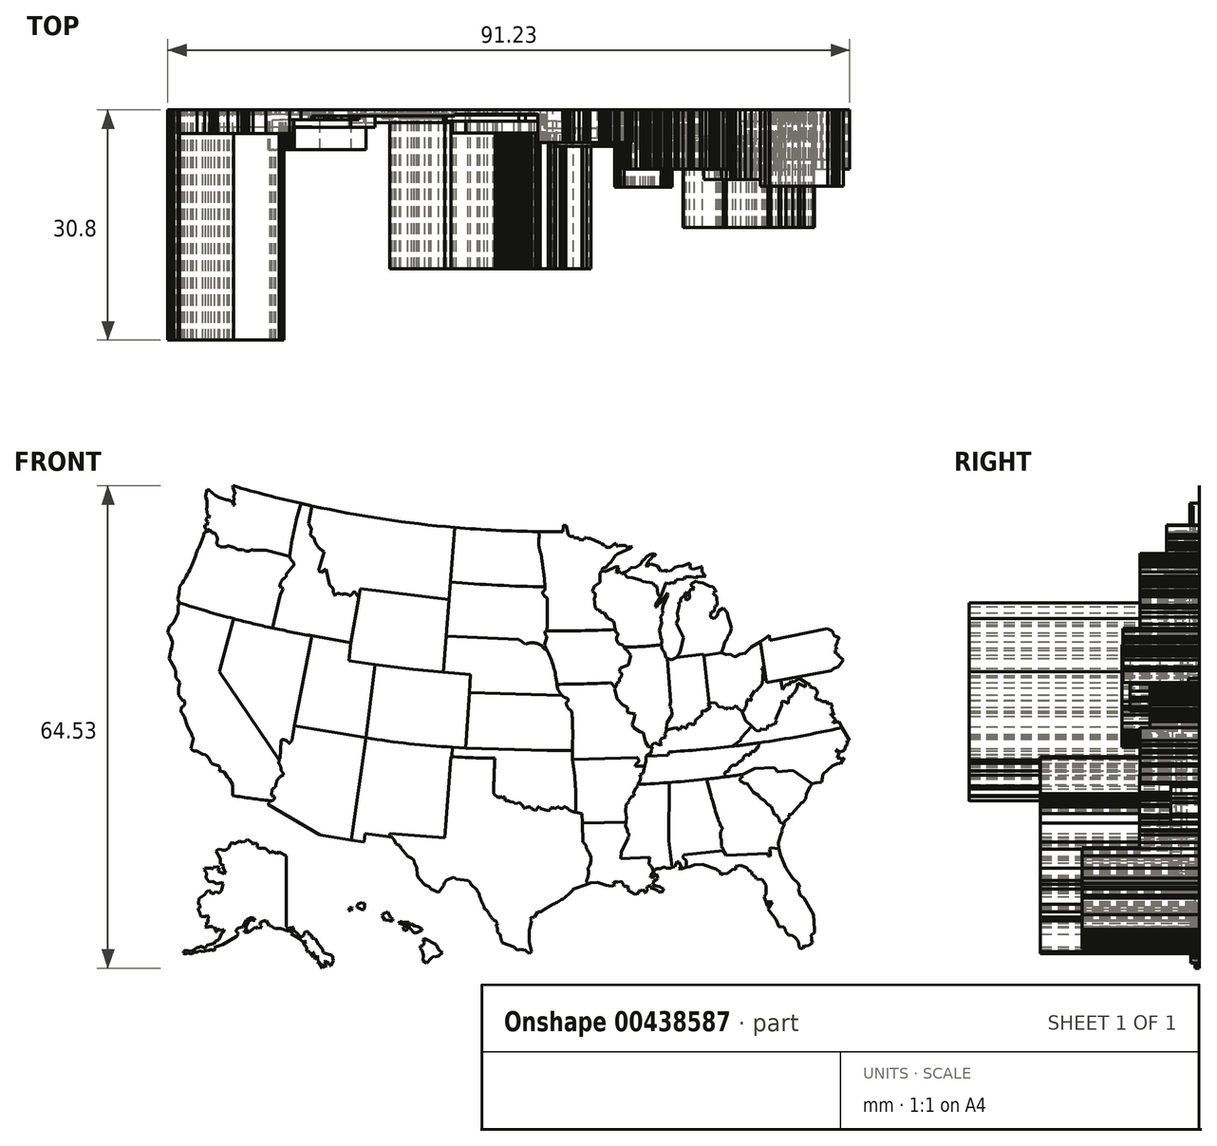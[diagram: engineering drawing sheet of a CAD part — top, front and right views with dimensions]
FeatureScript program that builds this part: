
annotation { "Feature Type Name" : "Feature", "Feature Type Description" : "" }
export const myFeature = defineFeature(function(context is Context, id is Id, definition is map)
    precondition{}
    {
        {
            var Q0;
            Q0=qCreatedBy(makeId("Front.planeOp"),FACE);
            var sketch = newSketch(context, id + "F0", { "sketchPlane" : qUnion([Q0])});
            skLineSegment(sketch, "E0", {"start": v(-20.34, -28.95) * mm, "end": v(-20.54, -28.82) * mm});
            skLineSegment(sketch, "E1", {"start": v(-20.54, -28.82) * mm, "end": v(-20.38, -28.34) * mm});
            skLineSegment(sketch, "E2", {"start": v(-20.62, -28.02) * mm, "end": v(-20.38, -28.34) * mm});
            skLineSegment(sketch, "E3", {"start": v(-20.62, -28.02) * mm, "end": v(-20.94, -27.88) * mm});
            skArc(sketch, "E4", {"start": v(-21.71, -26.67) * mm, "mid": v(-21.36, -27.3) * mm, "end": v(-20.94, -27.88) * mm});
            skArc(sketch, "E5", {"start": v(-22.15, -26.38) * mm, "mid": v(-21.93, -26.53) * mm, "end": v(-21.71, -26.67) * mm});
            skArc(sketch, "E6", {"start": v(-22.15, -26.13) * mm, "mid": v(-22.15, -26.26) * mm, "end": v(-22.15, -26.38) * mm});
            skArc(sketch, "E7", {"start": v(-22.74, -24.8) * mm, "mid": v(-22.46, -25.47) * mm, "end": v(-22.15, -26.13) * mm});
            skArc(sketch, "E8", {"start": v(-22.83, -24.33) * mm, "mid": v(-22.93, -24.22) * mm, "end": v(-23.05, -24.13) * mm});
            skArc(sketch, "E9", {"start": v(-22.83, -24.33) * mm, "mid": v(-22.8, -24.57) * mm, "end": v(-22.74, -24.8) * mm});
            skLineSegment(sketch, "E10", {"start": v(-36.72, 6.23) * mm, "end": v(-37.95, -3.53) * mm});
            skLineSegment(sketch, "E11", {"start": v(-23.98, 4.92) * mm, "end": v(-24.13, 2.5) * mm});
            skLineSegment(sketch, "E12", {"start": v(-45.2, 10.1) * mm, "end": v(-39.98, 9.18) * mm});
            skLineSegment(sketch, "E13", {"start": v(-39.98, 9.18) * mm, "end": v(-40.27, 6.76) * mm});
            skLineSegment(sketch, "E14", {"start": v(-40.27, 6.76) * mm, "end": v(-36.72, 6.23) * mm});
            skLineSegment(sketch, "E15", {"start": v(-47.5, -1.93) * mm, "end": v(-45.2, 10.1) * mm});
            skArc(sketch, "E16", {"start": v(-62.9, 14.51) * mm, "mid": v(-54.12, 12) * mm, "end": v(-45.2, 10.1) * mm});
            skLineSegment(sketch, "E17", {"start": v(-57.58, 5.33) * mm, "end": v(-55.66, 12.39) * mm});
            skLineSegment(sketch, "E18", {"start": v(-57.58, 5.33) * mm, "end": v(-49.6, -6.54) * mm});
            skLineSegment(sketch, "E19", {"start": v(-39.98, 9.18) * mm, "end": v(-38.7, 16.41) * mm});
            skLineSegment(sketch, "E20", {"start": v(-26.84, 14.95) * mm, "end": v(-38.7, 16.41) * mm});
            skLineSegment(sketch, "E21", {"start": v(-39.9, -17.25) * mm, "end": v(-37.95, -3.53) * mm});
            skLineSegment(sketch, "E22", {"start": v(-27.43, -16.92) * mm, "end": v(-26.59, -6.04) * mm});
            skLineSegment(sketch, "E23", {"start": v(-26.59, -6.04) * mm, "end": v(-26.47, -6.05) * mm});
            skLineSegment(sketch, "E24", {"start": v(-26.47, -6.05) * mm, "end": v(-26.38, -4.78) * mm});
            skLineSegment(sketch, "E25", {"start": v(-39.9, -17.25) * mm, "end": v(-38.2, -17.5) * mm});
            skLineSegment(sketch, "E26", {"start": v(-38.2, -17.5) * mm, "end": v(-38.09, -16.35) * mm});
            skLineSegment(sketch, "E27", {"start": v(-38.09, -16.35) * mm, "end": v(-34.78, -16.8) * mm});
            skLineSegment(sketch, "E28", {"start": v(-34.78, -16.8) * mm, "end": v(-34.78, -16.35) * mm});
            skLineSegment(sketch, "E29", {"start": v(-34.78, -16.35) * mm, "end": v(-27.43, -16.92) * mm});
            skLineSegment(sketch, "E30", {"start": v(-51.04, -12.46) * mm, "end": v(-44.1, -16.57) * mm});
            skLineSegment(sketch, "E31", {"start": v(-44.1, -16.57) * mm, "end": v(-39.9, -17.25) * mm});
            skArc(sketch, "E32", {"start": v(-26.47, -6.05) * mm, "mid": v(-23.6, -6.22) * mm, "end": v(-20.7, -6.27) * mm});
            skArc(sketch, "E33", {"start": v(-20.7, -6.27) * mm, "mid": v(-20.81, -8.64) * mm, "end": v(-20.87, -11) * mm});
            skArc(sketch, "E34", {"start": v(-55.68, 30.16) * mm, "mid": v(-33.87, 25.48) * mm, "end": v(-11.6, 24.05) * mm});
            skLineSegment(sketch, "E35", {"start": v(-26.84, 14.95) * mm, "end": v(-26.08, 24.6) * mm});
            skLineSegment(sketch, "E36", {"start": v(-27.22, 10.09) * mm, "end": v(-17.53, 9.6) * mm});
            skLineSegment(sketch, "E37", {"start": v(-24.13, 2.5) * mm, "end": v(-11.72, 2.13) * mm});
            skArc(sketch, "E38", {"start": v(-13.96, 10.74) * mm, "mid": v(-9.3, 10.79) * mm, "end": v(-4.62, 10.94) * mm});
            skArc(sketch, "E39", {"start": v(-12.43, 3.6) * mm, "mid": v(-8.8, 3.68) * mm, "end": v(-5.16, 3.82) * mm});
            skArc(sketch, "E40", {"start": v(-3.38, 8.64) * mm, "mid": v(-0.91, 8.67) * mm, "end": v(1.55, 8.92) * mm});
            skLineSegment(sketch, "E41", {"start": v(3.57, 7.23) * mm, "end": v(7.22, 7.64) * mm});
            skLineSegment(sketch, "E42", {"start": v(7.22, 7.64) * mm, "end": v(7.93, 1.1) * mm});
            skLineSegment(sketch, "E43", {"start": v(7.23, 7.48) * mm, "end": v(9.6, 7.85) * mm});
            skLineSegment(sketch, "E44", {"start": v(16, 10.2) * mm, "end": v(16.07, 9.52) * mm});
            skLineSegment(sketch, "E45", {"start": v(16.07, 9.52) * mm, "end": v(23.83, 11.1) * mm});
            skLineSegment(sketch, "E46", {"start": v(-10.36, -5.27) * mm, "end": v(-10.36, -6.47) * mm});
            skLineSegment(sketch, "E47", {"start": v(-10.36, -6.47) * mm, "end": v(-1.68, -6.17) * mm});
            skArc(sketch, "E48", {"start": v(-10.36, -5.27) * mm, "mid": v(-10.3, -2.61) * mm, "end": v(-10.44, 0.04) * mm});
            skArc(sketch, "E49", {"start": v(-46.68, 27.82) * mm, "mid": v(-47.57, 24.3) * mm, "end": v(-48.17, 20.7) * mm});
            skArc(sketch, "E50", {"start": v(2.53, -5.43) * mm, "mid": v(14.19, -4.28) * mm, "end": v(25.7, -2.2) * mm});
            skLineSegment(sketch, "E51", {"start": v(-0.47, -6.02) * mm, "end": v(2.5, -5.88) * mm});
            skLineSegment(sketch, "E52", {"start": v(2.5, -5.88) * mm, "end": v(2.53, -5.43) * mm});
            skArc(sketch, "E53", {"start": v(-1.64, -9.77) * mm, "mid": v(5.4, -9.3) * mm, "end": v(12.39, -8.45) * mm});
            skLineSegment(sketch, "E54", {"start": v(-9.01, -14.93) * mm, "end": v(-3.14, -14.82) * mm});
            skLineSegment(sketch, "E55", {"start": v(-49.6, -6.54) * mm, "end": v(-49.45, -6.3) * mm});
            skLineSegment(sketch, "E56", {"start": v(-49.45, -6.3) * mm, "end": v(-49.34, -3.91) * mm});
            skArc(sketch, "E57", {"start": v(-48.98, -3.76) * mm, "mid": v(-49.17, -3.8) * mm, "end": v(-49.34, -3.91) * mm});
            skArc(sketch, "E58", {"start": v(-48.71, -3.91) * mm, "mid": v(-48.84, -3.82) * mm, "end": v(-48.98, -3.76) * mm});
            skArc(sketch, "E59", {"start": v(-48.53, -3.91) * mm, "mid": v(-48.62, -3.91) * mm, "end": v(-48.71, -3.91) * mm});
            skArc(sketch, "E60", {"start": v(-47.85, -3.91) * mm, "mid": v(-48.02, -4.06) * mm, "end": v(-48.13, -4.24) * mm});
            skArc(sketch, "E61", {"start": v(-48.37, -4.23) * mm, "mid": v(-48.43, -4.06) * mm, "end": v(-48.53, -3.91) * mm});
            skArc(sketch, "E62", {"start": v(-48.37, -4.23) * mm, "mid": v(-48.25, -4.26) * mm, "end": v(-48.13, -4.24) * mm});
            skLineSegment(sketch, "E63", {"start": v(-47.85, -3.91) * mm, "end": v(-47.5, -1.93) * mm});
            skArc(sketch, "E64", {"start": v(-55.77, -11.27) * mm, "mid": v(-53.27, -11.66) * mm, "end": v(-50.77, -11.97) * mm});
            skArc(sketch, "E65", {"start": v(-50.77, -11.97) * mm, "mid": v(-50.91, -12.21) * mm, "end": v(-51.04, -12.46) * mm});
            skLineSegment(sketch, "E66", {"start": v(-55.82, -9.82) * mm, "end": v(-55.77, -11.27) * mm});
            skLineSegment(sketch, "E67", {"start": v(-55.82, -9.82) * mm, "end": v(-56.25, -9.03) * mm});
            skLineSegment(sketch, "E68", {"start": v(-56.25, -9.03) * mm, "end": v(-56.48, -8.81) * mm});
            skLineSegment(sketch, "E69", {"start": v(-56.48, -8.81) * mm, "end": v(-56.94, -8.11) * mm});
            skLineSegment(sketch, "E70", {"start": v(-56.94, -8.11) * mm, "end": v(-57.6, -8) * mm});
            skLineSegment(sketch, "E71", {"start": v(-57.6, -8) * mm, "end": v(-57.6, -7.87) * mm});
            skLineSegment(sketch, "E72", {"start": v(-57.6, -7.87) * mm, "end": v(-57.5, -7.8) * mm});
            skLineSegment(sketch, "E73", {"start": v(-57.5, -7.8) * mm, "end": v(-57.54, -7.47) * mm});
            skLineSegment(sketch, "E74", {"start": v(-57.54, -7.47) * mm, "end": v(-57.7, -7.24) * mm});
            skLineSegment(sketch, "E75", {"start": v(-57.7, -7.24) * mm, "end": v(-58.23, -7.14) * mm});
            skLineSegment(sketch, "E76", {"start": v(-58.23, -7.14) * mm, "end": v(-58.63, -6.93) * mm});
            skLineSegment(sketch, "E77", {"start": v(-58.63, -6.93) * mm, "end": v(-59.05, -6.18) * mm});
            skLineSegment(sketch, "E78", {"start": v(-59.05, -6.18) * mm, "end": v(-59.4, -5.8) * mm});
            skLineSegment(sketch, "E79", {"start": v(-59.4, -5.8) * mm, "end": v(-59.79, -5.74) * mm});
            skLineSegment(sketch, "E80", {"start": v(-59.79, -5.74) * mm, "end": v(-60.65, -5.32) * mm});
            skLineSegment(sketch, "E81", {"start": v(-60.65, -5.32) * mm, "end": v(-61.08, -5.27) * mm});
            skLineSegment(sketch, "E82", {"start": v(-61.08, -5.27) * mm, "end": v(-61.38, -4.98) * mm});
            skLineSegment(sketch, "E83", {"start": v(-61.38, -4.98) * mm, "end": v(-61.08, -3.74) * mm});
            skLineSegment(sketch, "E84", {"start": v(-61.08, -3.74) * mm, "end": v(-61.08, -3.5) * mm});
            skLineSegment(sketch, "E85", {"start": v(-61.08, -3.5) * mm, "end": v(-61.25, -3.34) * mm});
            skLineSegment(sketch, "E86", {"start": v(-61.25, -3.34) * mm, "end": v(-61.25, -3.08) * mm});
            skLineSegment(sketch, "E87", {"start": v(-61.25, -3.08) * mm, "end": v(-61.83, -2.09) * mm});
            skLineSegment(sketch, "E88", {"start": v(-61.83, -2.09) * mm, "end": v(-62.29, -0.7) * mm});
            skLineSegment(sketch, "E89", {"start": v(-62.29, -0.7) * mm, "end": v(-62.6, -0.23) * mm});
            skLineSegment(sketch, "E90", {"start": v(-62.6, -0.23) * mm, "end": v(-62.7, 0.06) * mm});
            skLineSegment(sketch, "E91", {"start": v(-62.7, 0.06) * mm, "end": v(-62.64, 0.56) * mm});
            skArc(sketch, "E92", {"start": v(-62.64, 0.56) * mm, "mid": v(-62.23, 0.9) * mm, "end": v(-62.26, 1.43) * mm});
            skLineSegment(sketch, "E93", {"start": v(-62.26, 1.43) * mm, "end": v(-62.53, 1.5) * mm});
            skLineSegment(sketch, "E94", {"start": v(-62.53, 1.5) * mm, "end": v(-63.01, 2.17) * mm});
            skLineSegment(sketch, "E95", {"start": v(-63.01, 2.17) * mm, "end": v(-63.01, 3.14) * mm});
            skLineSegment(sketch, "E96", {"start": v(-63.01, 3.14) * mm, "end": v(-62.84, 3.85) * mm});
            skLineSegment(sketch, "E97", {"start": v(-62.84, 3.85) * mm, "end": v(-63.44, 4.55) * mm});
            skLineSegment(sketch, "E98", {"start": v(-63.44, 4.55) * mm, "end": v(-63.44, 4.8) * mm});
            skArc(sketch, "E99", {"start": v(-63.44, 4.8) * mm, "mid": v(-63.42, 5.28) * mm, "end": v(-63.57, 5.73) * mm});
            skLineSegment(sketch, "E100", {"start": v(-64.28, 7.1) * mm, "end": v(-63.57, 5.73) * mm});
            skLineSegment(sketch, "E101", {"start": v(-64.28, 7.1) * mm, "end": v(-64.16, 7.52) * mm});
            skLineSegment(sketch, "E102", {"start": v(-64.16, 7.52) * mm, "end": v(-64.1, 8.17) * mm});
            skLineSegment(sketch, "E103", {"start": v(-64.1, 8.17) * mm, "end": v(-63.9, 8.5) * mm});
            skLineSegment(sketch, "E104", {"start": v(-63.9, 8.5) * mm, "end": v(-63.88, 9.29) * mm});
            skLineSegment(sketch, "E105", {"start": v(-63.88, 9.29) * mm, "end": v(-64.16, 10.12) * mm});
            skLineSegment(sketch, "E106", {"start": v(-64.16, 10.12) * mm, "end": v(-64.47, 10.53) * mm});
            skLineSegment(sketch, "E107", {"start": v(-64.47, 10.53) * mm, "end": v(-64.22, 11.4) * mm});
            skLineSegment(sketch, "E108", {"start": v(-64.22, 11.4) * mm, "end": v(-64.03, 11.46) * mm});
            skLineSegment(sketch, "E109", {"start": v(-64.03, 11.46) * mm, "end": v(-63.99, 11.62) * mm});
            skLineSegment(sketch, "E110", {"start": v(-63.99, 11.62) * mm, "end": v(-63.66, 11.91) * mm});
            skLineSegment(sketch, "E111", {"start": v(-63.66, 11.91) * mm, "end": v(-63.07, 13.2) * mm});
            skLineSegment(sketch, "E112", {"start": v(-63.07, 13.2) * mm, "end": v(-63.07, 14.03) * mm});
            skLineSegment(sketch, "E113", {"start": v(-63.07, 14.03) * mm, "end": v(-62.9, 14.51) * mm});
            skArc(sketch, "E114", {"start": v(-49.29, -7.95) * mm, "mid": v(-49.38, -7.41) * mm, "end": v(-49.65, -6.93) * mm});
            skLineSegment(sketch, "E115", {"start": v(-49.6, -6.54) * mm, "end": v(-49.65, -6.93) * mm});
            skArc(sketch, "E116", {"start": v(-50.77, -11.97) * mm, "mid": v(-50.32, -11.84) * mm, "end": v(-50.21, -11.38) * mm});
            skLineSegment(sketch, "E117", {"start": v(-50.21, -11.38) * mm, "end": v(-50.57, -11.3) * mm});
            skLineSegment(sketch, "E118", {"start": v(-50.57, -11.3) * mm, "end": v(-50.53, -10.41) * mm});
            skArc(sketch, "E119", {"start": v(-50.53, -10.41) * mm, "mid": v(-50.24, -10.25) * mm, "end": v(-50, -10) * mm});
            skArc(sketch, "E120", {"start": v(-48.97, -8.52) * mm, "mid": v(-49.74, -9.08) * mm, "end": v(-50, -10) * mm});
            skArc(sketch, "E121", {"start": v(-48.97, -8.52) * mm, "mid": v(-49.08, -8.2) * mm, "end": v(-49.29, -7.95) * mm});
            skLineSegment(sketch, "E122", {"start": v(-50.47, 11.14) * mm, "end": v(-49.45, 15.52) * mm});
            skLineSegment(sketch, "E123", {"start": v(-49.45, 15.52) * mm, "end": v(-49.06, 16.34) * mm});
            skLineSegment(sketch, "E124", {"start": v(-49.06, 16.34) * mm, "end": v(-49.18, 16.6) * mm});
            skLineSegment(sketch, "E125", {"start": v(-49.18, 16.6) * mm, "end": v(-49.49, 16.67) * mm});
            skLineSegment(sketch, "E126", {"start": v(-48.17, 20.7) * mm, "end": v(-51.36, 21.55) * mm});
            skLineSegment(sketch, "E127", {"start": v(-51.36, 21.55) * mm, "end": v(-53.04, 21.55) * mm});
            skLineSegment(sketch, "E128", {"start": v(-53.04, 21.55) * mm, "end": v(-53.04, 21.67) * mm});
            skLineSegment(sketch, "E129", {"start": v(-53.04, 21.67) * mm, "end": v(-53.6, 21.46) * mm});
            skLineSegment(sketch, "E130", {"start": v(-53.6, 21.46) * mm, "end": v(-54.1, 21.46) * mm});
            skLineSegment(sketch, "E131", {"start": v(-54.1, 21.46) * mm, "end": v(-54.43, 21.7) * mm});
            skLineSegment(sketch, "E132", {"start": v(-54.43, 21.7) * mm, "end": v(-54.57, 21.61) * mm});
            skLineSegment(sketch, "E133", {"start": v(-54.57, 21.61) * mm, "end": v(-55.07, 21.61) * mm});
            skArc(sketch, "E134", {"start": v(-55.07, 21.61) * mm, "mid": v(-55.72, 21.94) * mm, "end": v(-56.43, 22.14) * mm});
            skArc(sketch, "E135", {"start": v(-57.98, 22.44) * mm, "mid": v(-57.26, 21.99) * mm, "end": v(-56.43, 22.14) * mm});
            skArc(sketch, "E136", {"start": v(-57.98, 22.44) * mm, "mid": v(-57.86, 23.17) * mm, "end": v(-58.17, 23.85) * mm});
            skLineSegment(sketch, "E137", {"start": v(-58.17, 23.85) * mm, "end": v(-58.58, 23.85) * mm});
            skLineSegment(sketch, "E138", {"start": v(-58.58, 23.85) * mm, "end": v(-58.58, 24.15) * mm});
            skLineSegment(sketch, "E139", {"start": v(-58.58, 24.15) * mm, "end": v(-58.83, 24.15) * mm});
            skLineSegment(sketch, "E140", {"start": v(-58.83, 24.15) * mm, "end": v(-59.13, 24.38) * mm});
            skLineSegment(sketch, "E141", {"start": v(-59.13, 24.38) * mm, "end": v(-59.31, 24.3) * mm});
            skLineSegment(sketch, "E142", {"start": v(-59.31, 24.3) * mm, "end": v(-59.57, 24.6) * mm});
            skLineSegment(sketch, "E143", {"start": v(-59.57, 24.6) * mm, "end": v(-59.53, 24.93) * mm});
            skLineSegment(sketch, "E144", {"start": v(-59.53, 24.93) * mm, "end": v(-59.25, 24.93) * mm});
            skLineSegment(sketch, "E145", {"start": v(-59.25, 24.93) * mm, "end": v(-59.07, 25.4) * mm});
            skLineSegment(sketch, "E146", {"start": v(-59.07, 25.4) * mm, "end": v(-59.34, 25.55) * mm});
            skLineSegment(sketch, "E147", {"start": v(-59.34, 25.55) * mm, "end": v(-59.3, 25.94) * mm});
            skLineSegment(sketch, "E148", {"start": v(-59.3, 25.94) * mm, "end": v(-58.8, 26) * mm});
            skLineSegment(sketch, "E149", {"start": v(-58.8, 26) * mm, "end": v(-59.16, 26.34) * mm});
            skLineSegment(sketch, "E150", {"start": v(-59.16, 26.34) * mm, "end": v(-59.3, 27.1) * mm});
            skLineSegment(sketch, "E151", {"start": v(-59.3, 27.1) * mm, "end": v(-59.23, 27.36) * mm});
            skLineSegment(sketch, "E152", {"start": v(-59.23, 27.36) * mm, "end": v(-59.23, 28.3) * mm});
            skLineSegment(sketch, "E153", {"start": v(-59.23, 28.3) * mm, "end": v(-59.41, 28.62) * mm});
            skLineSegment(sketch, "E154", {"start": v(-59.41, 28.62) * mm, "end": v(-59.41, 28.8) * mm});
            skLineSegment(sketch, "E155", {"start": v(-59.41, 28.8) * mm, "end": v(-59.2, 29.68) * mm});
            skLineSegment(sketch, "E156", {"start": v(-59.2, 29.68) * mm, "end": v(-58.95, 29.65) * mm});
            skArc(sketch, "E157", {"start": v(-58.95, 29.65) * mm, "mid": v(-57.74, 28.7) * mm, "end": v(-56.25, 28.25) * mm});
            skArc(sketch, "E158", {"start": v(-55.7, 27.58) * mm, "mid": v(-55.87, 28) * mm, "end": v(-56.25, 28.25) * mm});
            skArc(sketch, "E159", {"start": v(-55.58, 28.4) * mm, "mid": v(-55.67, 28.07) * mm, "end": v(-55.51, 27.76) * mm});
            skArc(sketch, "E160", {"start": v(-55.47, 29.18) * mm, "mid": v(-55.64, 28.8) * mm, "end": v(-55.58, 28.4) * mm});
            skLineSegment(sketch, "E161", {"start": v(-55.51, 27.76) * mm, "end": v(-55.51, 27.57) * mm});
            skLineSegment(sketch, "E162", {"start": v(-55.51, 27.57) * mm, "end": v(-55.7, 27.58) * mm});
            skLineSegment(sketch, "E163", {"start": v(-55.47, 29.18) * mm, "end": v(-55.8, 30) * mm});
            skLineSegment(sketch, "E164", {"start": v(-55.8, 30) * mm, "end": v(-55.75, 30.17) * mm});
            skLineSegment(sketch, "E165", {"start": v(-55.75, 30.17) * mm, "end": v(-55.68, 30.16) * mm});
            skArc(sketch, "E166", {"start": v(-48.73, 17.9) * mm, "mid": v(-49.28, 17.39) * mm, "end": v(-49.49, 16.67) * mm});
            skArc(sketch, "E167", {"start": v(-48.73, 17.9) * mm, "mid": v(-48.63, 18.1) * mm, "end": v(-48.6, 18.34) * mm});
            skArc(sketch, "E168", {"start": v(-47.6, 19.56) * mm, "mid": v(-48.13, 18.97) * mm, "end": v(-48.6, 18.34) * mm});
            skArc(sketch, "E169", {"start": v(-48.17, 20.7) * mm, "mid": v(-48, 20.3) * mm, "end": v(-47.67, 20.02) * mm});
            skLineSegment(sketch, "E170", {"start": v(-47.67, 20.02) * mm, "end": v(-47.6, 19.56) * mm});
            skArc(sketch, "E171", {"start": v(16, 10.2) * mm, "mid": v(16.73, 10.91) * mm, "end": v(17.3, 11.76) * mm});
            skArc(sketch, "E172", {"start": v(16.77, 12.86) * mm, "mid": v(16.87, 12.6) * mm, "end": v(16.97, 12.33) * mm});
            skArc(sketch, "E173", {"start": v(17.3, 11.76) * mm, "mid": v(17.23, 12.1) * mm, "end": v(16.97, 12.33) * mm});
            skArc(sketch, "E174", {"start": v(19.11, 13.4) * mm, "mid": v(17.9, 13.32) * mm, "end": v(16.77, 12.86) * mm});
            skArc(sketch, "E175", {"start": v(19.11, 13.4) * mm, "mid": v(19.38, 13.28) * mm, "end": v(19.64, 13.4) * mm});
            skArc(sketch, "E176", {"start": v(20.53, 13.56) * mm, "mid": v(20.07, 13.56) * mm, "end": v(19.64, 13.4) * mm});
            skArc(sketch, "E177", {"start": v(20.53, 13.56) * mm, "mid": v(20.87, 13.94) * mm, "end": v(21.18, 14.34) * mm});
            skArc(sketch, "E178", {"start": v(21.18, 14.34) * mm, "mid": v(21.6, 14.5) * mm, "end": v(21.45, 14.92) * mm});
            skArc(sketch, "E179", {"start": v(21.58, 15.51) * mm, "mid": v(21.47, 15.23) * mm, "end": v(21.45, 14.92) * mm});
            skArc(sketch, "E180", {"start": v(21.38, 16.32) * mm, "mid": v(21.08, 15.82) * mm, "end": v(21.58, 15.51) * mm});
            skArc(sketch, "E181", {"start": v(21.38, 16.32) * mm, "mid": v(21.56, 16.5) * mm, "end": v(21.73, 16.7) * mm});
            skArc(sketch, "E182", {"start": v(23.04, 18.39) * mm, "mid": v(22.3, 17.61) * mm, "end": v(21.73, 16.7) * mm});
            skArc(sketch, "E183", {"start": v(23.83, 11.1) * mm, "mid": v(24.11, 10.88) * mm, "end": v(24.45, 10.78) * mm});
            skArc(sketch, "E184", {"start": v(24.45, 10.78) * mm, "mid": v(24.6, 10.34) * mm, "end": v(24.89, 9.98) * mm});
            skArc(sketch, "E185", {"start": v(25.37, 9.77) * mm, "mid": v(25.17, 9.96) * mm, "end": v(24.89, 9.98) * mm});
            skLineSegment(sketch, "E186", {"start": v(25.37, 9.77) * mm, "end": v(27, 9.26) * mm});
            skLineSegment(sketch, "E187", {"start": v(27, 9.26) * mm, "end": v(27, 8.37) * mm});
            skArc(sketch, "E188", {"start": v(27, 8.37) * mm, "mid": v(28.7, 8.93) * mm, "end": v(30.08, 10.05) * mm});
            skLineSegment(sketch, "E189", {"start": v(30.08, 10.05) * mm, "end": v(29.67, 10.23) * mm});
            skArc(sketch, "E190", {"start": v(28.36, 9.39) * mm, "mid": v(29.08, 9.7) * mm, "end": v(29.67, 10.23) * mm});
            skArc(sketch, "E191", {"start": v(27.92, 9.39) * mm, "mid": v(28.14, 9.35) * mm, "end": v(28.36, 9.39) * mm});
            skLineSegment(sketch, "E192", {"start": v(27.92, 9.39) * mm, "end": v(27.42, 8.95) * mm});
            skLineSegment(sketch, "E193", {"start": v(27.42, 8.95) * mm, "end": v(27.23, 8.9) * mm});
            skLineSegment(sketch, "E194", {"start": v(27.23, 8.9) * mm, "end": v(27.23, 9.05) * mm});
            skLineSegment(sketch, "E195", {"start": v(27.23, 9.05) * mm, "end": v(27.42, 9.26) * mm});
            skLineSegment(sketch, "E196", {"start": v(27.42, 9.26) * mm, "end": v(27.42, 9.44) * mm});
            skLineSegment(sketch, "E197", {"start": v(27.42, 9.44) * mm, "end": v(27.22, 9.63) * mm});
            skLineSegment(sketch, "E198", {"start": v(27.22, 9.63) * mm, "end": v(27.35, 9.77) * mm});
            skLineSegment(sketch, "E199", {"start": v(27.35, 9.77) * mm, "end": v(27.35, 10.79) * mm});
            skLineSegment(sketch, "E200", {"start": v(27.35, 10.79) * mm, "end": v(27.06, 11.96) * mm});
            skLineSegment(sketch, "E201", {"start": v(27.06, 11.96) * mm, "end": v(27.06, 13.72) * mm});
            skLineSegment(sketch, "E202", {"start": v(27.06, 13.72) * mm, "end": v(26.66, 15.58) * mm});
            skArc(sketch, "E203", {"start": v(26.66, 15.58) * mm, "mid": v(26.51, 15.72) * mm, "end": v(26.32, 15.64) * mm});
            skArc(sketch, "E204", {"start": v(24.37, 18.62) * mm, "mid": v(23.7, 18.56) * mm, "end": v(23.04, 18.39) * mm});
            skLineSegment(sketch, "E205", {"start": v(24.37, 18.62) * mm, "end": v(25.7, 18.98) * mm});
            skLineSegment(sketch, "E206", {"start": v(25.7, 18.98) * mm, "end": v(26.12, 17.45) * mm});
            skArc(sketch, "E207", {"start": v(25.98, 16.83) * mm, "mid": v(26.13, 17.12) * mm, "end": v(26.12, 17.45) * mm});
            skLineSegment(sketch, "E208", {"start": v(25.98, 16.83) * mm, "end": v(26.36, 16.1) * mm});
            skLineSegment(sketch, "E209", {"start": v(26.36, 16.1) * mm, "end": v(26.32, 15.64) * mm});
            skLineSegment(sketch, "E210", {"start": v(-62.9, 14.51) * mm, "end": v(-63.14, 15.01) * mm});
            skLineSegment(sketch, "E211", {"start": v(-63.14, 15.01) * mm, "end": v(-62.97, 15.69) * mm});
            skLineSegment(sketch, "E212", {"start": v(-62.97, 15.69) * mm, "end": v(-62.9, 16.65) * mm});
            skArc(sketch, "E213", {"start": v(-62.9, 16.65) * mm, "mid": v(-61.53, 18.95) * mm, "end": v(-60.56, 21.44) * mm});
            skLineSegment(sketch, "E214", {"start": v(-58.83, 24.15) * mm, "end": v(-59.54, 24) * mm});
            skArc(sketch, "E215", {"start": v(-60.56, 21.44) * mm, "mid": v(-60, 22.7) * mm, "end": v(-59.54, 24) * mm});
            skLineSegment(sketch, "E216", {"start": v(-17.53, 9.6) * mm, "end": v(-16.6, 8.98) * mm});
            skArc(sketch, "E217", {"start": v(-14.3, 8.68) * mm, "mid": v(-15.4, 9.16) * mm, "end": v(-16.6, 8.98) * mm});
            skArc(sketch, "E218", {"start": v(-14.3, 8.68) * mm, "mid": v(-14.11, 8.35) * mm, "end": v(-13.74, 8.25) * mm});
            skArc(sketch, "E219", {"start": v(-12.43, 3.6) * mm, "mid": v(-12.86, 6) * mm, "end": v(-13.74, 8.25) * mm});
            skArc(sketch, "E220", {"start": v(-12.43, 3.6) * mm, "mid": v(-12.19, 2.81) * mm, "end": v(-11.72, 2.13) * mm});
            skArc(sketch, "E221", {"start": v(-11.72, 2.13) * mm, "mid": v(-11.4, 1.88) * mm, "end": v(-11, 1.75) * mm});
            skArc(sketch, "E222", {"start": v(-11.16, 1.2) * mm, "mid": v(-10.92, 1.43) * mm, "end": v(-11, 1.75) * mm});
            skArc(sketch, "E223", {"start": v(-11.16, 1.2) * mm, "mid": v(-10.97, 0.52) * mm, "end": v(-10.44, 0.04) * mm});
            skLineSegment(sketch, "E224", {"start": v(-45.17, 27.48) * mm, "end": v(-45.64, 25.13) * mm});
            skLineSegment(sketch, "E225", {"start": v(-45.64, 25.13) * mm, "end": v(-45.28, 24.39) * mm});
            skLineSegment(sketch, "E226", {"start": v(-45.28, 24.39) * mm, "end": v(-45.4, 23.67) * mm});
            skArc(sketch, "E227", {"start": v(-45.4, 23.67) * mm, "mid": v(-45.18, 23.38) * mm, "end": v(-44.88, 23.2) * mm});
            skArc(sketch, "E228", {"start": v(-44.88, 23.2) * mm, "mid": v(-44.45, 22.11) * mm, "end": v(-43.56, 21.37) * mm});
            skLineSegment(sketch, "E229", {"start": v(-44.33, 18.83) * mm, "end": v(-43.56, 21.37) * mm});
            skLineSegment(sketch, "E230", {"start": v(-44, 18.55) * mm, "end": v(-44.33, 18.83) * mm});
            skLineSegment(sketch, "E231", {"start": v(-42.33, 16.4) * mm, "end": v(-42.87, 16.94) * mm});
            skLineSegment(sketch, "E232", {"start": v(-42.87, 16.94) * mm, "end": v(-43.29, 19) * mm});
            skLineSegment(sketch, "E233", {"start": v(-43.29, 19) * mm, "end": v(-44, 18.55) * mm});
            skArc(sketch, "E234", {"start": v(-42.33, 16.4) * mm, "mid": v(-42.3, 15.92) * mm, "end": v(-42.11, 15.49) * mm});
            skArc(sketch, "E235", {"start": v(-41.24, 15.6) * mm, "mid": v(-41.7, 15.77) * mm, "end": v(-42.11, 15.49) * mm});
            skArc(sketch, "E236", {"start": v(-40.14, 15.49) * mm, "mid": v(-40.68, 15.7) * mm, "end": v(-41.24, 15.6) * mm});
            skArc(sketch, "E237", {"start": v(-40.14, 15.49) * mm, "mid": v(-39.86, 15.6) * mm, "end": v(-39.74, 15.9) * mm});
            skArc(sketch, "E238", {"start": v(-39.32, 15.88) * mm, "mid": v(-39.17, 15.53) * mm, "end": v(-38.91, 15.26) * mm});
            skArc(sketch, "E239", {"start": v(-39.32, 15.88) * mm, "mid": v(-39.53, 15.94) * mm, "end": v(-39.74, 15.9) * mm});
            skArc(sketch, "E240", {"start": v(-9.92, -13.52) * mm, "mid": v(-9.92, -9.98) * mm, "end": v(-10.36, -6.47) * mm});
            skLineSegment(sketch, "E241", {"start": v(-9.92, -13.52) * mm, "end": v(-9.07, -13.67) * mm});
            skLineSegment(sketch, "E242", {"start": v(-9.07, -13.67) * mm, "end": v(-9.01, -14.93) * mm});
            skLineSegment(sketch, "E243", {"start": v(-9.01, -14.93) * mm, "end": v(-8.96, -17.48) * mm});
            skLineSegment(sketch, "E244", {"start": v(-20.34, -28.95) * mm, "end": v(-20.34, -29.39) * mm});
            skArc(sketch, "E245", {"start": v(-20.34, -29.39) * mm, "mid": v(-20.25, -29.66) * mm, "end": v(-20.01, -29.82) * mm});
            skArc(sketch, "E246", {"start": v(-20.01, -29.82) * mm, "mid": v(-19.9, -30.4) * mm, "end": v(-19.71, -30.96) * mm});
            skLineSegment(sketch, "E247", {"start": v(-15.8, -32.15) * mm, "end": v(-16.1, -32.38) * mm});
            skLineSegment(sketch, "E248", {"start": v(-16.1, -32.38) * mm, "end": v(-16.63, -31.97) * mm});
            skLineSegment(sketch, "E249", {"start": v(-16.63, -31.97) * mm, "end": v(-17.25, -31.87) * mm});
            skLineSegment(sketch, "E250", {"start": v(-17.25, -31.87) * mm, "end": v(-17.48, -31.94) * mm});
            skLineSegment(sketch, "E251", {"start": v(-17.48, -31.94) * mm, "end": v(-17.68, -31.95) * mm});
            skLineSegment(sketch, "E252", {"start": v(-17.68, -31.95) * mm, "end": v(-18.14, -31.52) * mm});
            skLineSegment(sketch, "E253", {"start": v(-18.14, -31.52) * mm, "end": v(-19.71, -30.96) * mm});
            skLineSegment(sketch, "E254", {"start": v(-0.7, -7.34) * mm, "end": v(-1.95, -7.34) * mm});
            skArc(sketch, "E255", {"start": v(-1.47, -6.76) * mm, "mid": v(-1.76, -7) * mm, "end": v(-1.95, -7.34) * mm});
            skArc(sketch, "E256", {"start": v(-1.47, -6.76) * mm, "mid": v(-1.5, -6.44) * mm, "end": v(-1.68, -6.17) * mm});
            skLineSegment(sketch, "E257", {"start": v(-13.74, 8.25) * mm, "end": v(-14.05, 8.84) * mm});
            skLineSegment(sketch, "E258", {"start": v(-14.05, 8.84) * mm, "end": v(-13.74, 9.96) * mm});
            skArc(sketch, "E259", {"start": v(-13.96, 10.74) * mm, "mid": v(-13.97, 10.32) * mm, "end": v(-13.74, 9.96) * mm});
            skArc(sketch, "E260", {"start": v(-26.65, 17.32) * mm, "mid": v(-20.33, 16.87) * mm, "end": v(-14, 16.64) * mm});
            skArc(sketch, "E261", {"start": v(-13.74, 10.74) * mm, "mid": v(-13.68, 12.95) * mm, "end": v(-13.72, 15.15) * mm});
            skArc(sketch, "E262", {"start": v(-14.34, 16) * mm, "mid": v(-14.04, 16.25) * mm, "end": v(-14, 16.64) * mm});
            skArc(sketch, "E263", {"start": v(-14.34, 16) * mm, "mid": v(-14.13, 15.5) * mm, "end": v(-13.72, 15.15) * mm});
            skArc(sketch, "E264", {"start": v(-14.8, 23.25) * mm, "mid": v(-14.78, 23.67) * mm, "end": v(-14.96, 24.05) * mm});
            skArc(sketch, "E265", {"start": v(-14.8, 23.25) * mm, "mid": v(-14.82, 22.12) * mm, "end": v(-14.52, 21.03) * mm});
            skLineSegment(sketch, "E266", {"start": v(-14.52, 21.03) * mm, "end": v(-14.07, 17.77) * mm});
            skLineSegment(sketch, "E267", {"start": v(-14.07, 17.77) * mm, "end": v(-14, 16.64) * mm});
            skArc(sketch, "E268", {"start": v(-8.45, -18.47) * mm, "mid": v(-8.57, -17.9) * mm, "end": v(-8.96, -17.48) * mm});
            skArc(sketch, "E269", {"start": v(-8.25, -21) * mm, "mid": v(-7.86, -19.7) * mm, "end": v(-8.45, -18.47) * mm});
            skArc(sketch, "E270", {"start": v(-8.45, -22.63) * mm, "mid": v(-8.2, -21.83) * mm, "end": v(-8.25, -21) * mm});
            skLineSegment(sketch, "E271", {"start": v(-8.45, -22.63) * mm, "end": v(-8.35, -23.12) * mm});
            skLineSegment(sketch, "E272", {"start": v(-8.35, -23.12) * mm, "end": v(-10.19, -23.78) * mm});
            skArc(sketch, "E273", {"start": v(-12.92, -25.8) * mm, "mid": v(-11.43, -24.96) * mm, "end": v(-10.19, -23.78) * mm});
            skArc(sketch, "E274", {"start": v(-12.92, -25.8) * mm, "mid": v(-13.78, -26.3) * mm, "end": v(-14.58, -26.86) * mm});
            skArc(sketch, "E275", {"start": v(-15.8, -28) * mm, "mid": v(-16.13, -30.08) * mm, "end": v(-15.8, -32.15) * mm});
            skLineSegment(sketch, "E276", {"start": v(-14.58, -26.86) * mm, "end": v(-14.95, -26.86) * mm});
            skLineSegment(sketch, "E277", {"start": v(-14.95, -26.86) * mm, "end": v(-15.4, -27.54) * mm});
            skLineSegment(sketch, "E278", {"start": v(-15.4, -27.54) * mm, "end": v(-15.85, -27.58) * mm});
            skLineSegment(sketch, "E279", {"start": v(-15.85, -27.58) * mm, "end": v(-15.97, -27.8) * mm});
            skLineSegment(sketch, "E280", {"start": v(-15.97, -27.8) * mm, "end": v(-15.8, -28) * mm});
            skLineSegment(sketch, "E281", {"start": v(-23.05, -24.13) * mm, "end": v(-23.05, -23.97) * mm});
            skLineSegment(sketch, "E282", {"start": v(-23.05, -23.97) * mm, "end": v(-23.96, -23.07) * mm});
            skLineSegment(sketch, "E283", {"start": v(-23.96, -23.07) * mm, "end": v(-23.97, -22.9) * mm});
            skLineSegment(sketch, "E284", {"start": v(-23.97, -22.9) * mm, "end": v(-24.28, -22.66) * mm});
            skLineSegment(sketch, "E285", {"start": v(-24.28, -22.66) * mm, "end": v(-25.9, -22.47) * mm});
            skLineSegment(sketch, "E286", {"start": v(-25.9, -22.47) * mm, "end": v(-26.24, -22.2) * mm});
            skLineSegment(sketch, "E287", {"start": v(-26.24, -22.2) * mm, "end": v(-27.17, -22.56) * mm});
            skLineSegment(sketch, "E288", {"start": v(-27.17, -22.56) * mm, "end": v(-27.5, -22.96) * mm});
            skLineSegment(sketch, "E289", {"start": v(-27.5, -22.96) * mm, "end": v(-27.53, -23.27) * mm});
            skLineSegment(sketch, "E290", {"start": v(-27.53, -23.27) * mm, "end": v(-28.22, -24.21) * mm});
            skLineSegment(sketch, "E291", {"start": v(-28.22, -24.21) * mm, "end": v(-29.26, -23.8) * mm});
            skLineSegment(sketch, "E292", {"start": v(-29.26, -23.8) * mm, "end": v(-29.5, -23.46) * mm});
            skLineSegment(sketch, "E293", {"start": v(-29.5, -23.46) * mm, "end": v(-30.1, -23.2) * mm});
            skLineSegment(sketch, "E294", {"start": v(-30.1, -23.2) * mm, "end": v(-30.85, -22.4) * mm});
            skLineSegment(sketch, "E295", {"start": v(-30.85, -22.4) * mm, "end": v(-31.1, -21.96) * mm});
            skLineSegment(sketch, "E296", {"start": v(-31.1, -21.96) * mm, "end": v(-31.13, -20.93) * mm});
            skLineSegment(sketch, "E297", {"start": v(-31.13, -20.93) * mm, "end": v(-31.47, -20.31) * mm});
            skLineSegment(sketch, "E298", {"start": v(-31.47, -20.31) * mm, "end": v(-31.54, -19.94) * mm});
            skLineSegment(sketch, "E299", {"start": v(-31.54, -19.94) * mm, "end": v(-31.83, -19.65) * mm});
            skLineSegment(sketch, "E300", {"start": v(-31.83, -19.65) * mm, "end": v(-32.35, -19.38) * mm});
            skLineSegment(sketch, "E301", {"start": v(-32.35, -19.38) * mm, "end": v(-33.33, -18.26) * mm});
            skLineSegment(sketch, "E302", {"start": v(-33.33, -18.26) * mm, "end": v(-33.46, -17.94) * mm});
            skLineSegment(sketch, "E303", {"start": v(-33.46, -17.94) * mm, "end": v(-33.93, -17.72) * mm});
            skLineSegment(sketch, "E304", {"start": v(-33.93, -17.72) * mm, "end": v(-34.11, -17.25) * mm});
            skLineSegment(sketch, "E305", {"start": v(-34.11, -17.25) * mm, "end": v(-34.48, -16.88) * mm});
            skLineSegment(sketch, "E306", {"start": v(-34.48, -16.88) * mm, "end": v(-34.78, -16.8) * mm});
            skArc(sketch, "E307", {"start": v(7.64, -9.07) * mm, "mid": v(8.4, -11.92) * mm, "end": v(9.25, -14.75) * mm});
            skLineSegment(sketch, "E308", {"start": v(2.65, -9.53) * mm, "end": v(2.54, -17.3) * mm});
            skLineSegment(sketch, "E309", {"start": v(2.54, -17.3) * mm, "end": v(2.98, -20.86) * mm});
            skLineSegment(sketch, "E310", {"start": v(2.98, -20.86) * mm, "end": v(3.36, -20.82) * mm});
            skLineSegment(sketch, "E311", {"start": v(3.36, -20.82) * mm, "end": v(3.66, -20.08) * mm});
            skLineSegment(sketch, "E312", {"start": v(3.66, -20.08) * mm, "end": v(3.88, -20.17) * mm});
            skLineSegment(sketch, "E313", {"start": v(3.88, -20.17) * mm, "end": v(4.25, -20.85) * mm});
            skLineSegment(sketch, "E314", {"start": v(4.25, -20.85) * mm, "end": v(3.91, -21.07) * mm});
            skLineSegment(sketch, "E315", {"start": v(3.91, -21.07) * mm, "end": v(4.17, -21.13) * mm});
            skLineSegment(sketch, "E316", {"start": v(4.17, -21.13) * mm, "end": v(4.94, -20.84) * mm});
            skLineSegment(sketch, "E317", {"start": v(4.94, -20.84) * mm, "end": v(5.36, -20.77) * mm});
            skLineSegment(sketch, "E318", {"start": v(5.36, -20.77) * mm, "end": v(5.98, -20.57) * mm});
            skLineSegment(sketch, "E319", {"start": v(5.98, -20.57) * mm, "end": v(7.07, -20.46) * mm});
            skLineSegment(sketch, "E320", {"start": v(7.07, -20.46) * mm, "end": v(8.89, -21.1) * mm});
            skLineSegment(sketch, "E321", {"start": v(8.89, -21.1) * mm, "end": v(9.08, -21.33) * mm});
            skLineSegment(sketch, "E322", {"start": v(9.08, -21.33) * mm, "end": v(9.21, -21.33) * mm});
            skLineSegment(sketch, "E323", {"start": v(9.21, -21.33) * mm, "end": v(9.45, -21.52) * mm});
            skLineSegment(sketch, "E324", {"start": v(9.45, -21.52) * mm, "end": v(9.56, -21.9) * mm});
            skLineSegment(sketch, "E325", {"start": v(9.56, -21.9) * mm, "end": v(9.83, -21.73) * mm});
            skLineSegment(sketch, "E326", {"start": v(9.83, -21.73) * mm, "end": v(10.42, -21.7) * mm});
            skLineSegment(sketch, "E327", {"start": v(10.42, -21.7) * mm, "end": v(11.14, -21.1) * mm});
            skLineSegment(sketch, "E328", {"start": v(11.14, -21.1) * mm, "end": v(11.53, -21.16) * mm});
            skLineSegment(sketch, "E329", {"start": v(11.53, -21.16) * mm, "end": v(11.5, -20.72) * mm});
            skLineSegment(sketch, "E330", {"start": v(11.5, -20.72) * mm, "end": v(12.22, -20.61) * mm});
            skLineSegment(sketch, "E331", {"start": v(12.22, -20.61) * mm, "end": v(12.98, -20.9) * mm});
            skLineSegment(sketch, "E332", {"start": v(12.98, -20.9) * mm, "end": v(13.29, -21.3) * mm});
            skLineSegment(sketch, "E333", {"start": v(13.29, -21.3) * mm, "end": v(13.6, -21.45) * mm});
            skLineSegment(sketch, "E334", {"start": v(13.6, -21.45) * mm, "end": v(13.72, -21.9) * mm});
            skLineSegment(sketch, "E335", {"start": v(13.72, -21.9) * mm, "end": v(14.07, -21.99) * mm});
            skLineSegment(sketch, "E336", {"start": v(14.07, -21.99) * mm, "end": v(14.3, -22.42) * mm});
            skLineSegment(sketch, "E337", {"start": v(14.3, -22.42) * mm, "end": v(15.04, -22.5) * mm});
            skLineSegment(sketch, "E338", {"start": v(10.26, -19.28) * mm, "end": v(15.82, -19) * mm});
            skLineSegment(sketch, "E339", {"start": v(4.5, -19.22) * mm, "end": v(9.89, -18.66) * mm});
            skLineSegment(sketch, "E340", {"start": v(9.89, -18.66) * mm, "end": v(10.26, -19.28) * mm});
            skLineSegment(sketch, "E341", {"start": v(4.5, -19.22) * mm, "end": v(4.46, -19.57) * mm});
            skLineSegment(sketch, "E342", {"start": v(4.46, -19.57) * mm, "end": v(4.93, -19.98) * mm});
            skLineSegment(sketch, "E343", {"start": v(4.93, -19.98) * mm, "end": v(4.94, -20.84) * mm});
            skArc(sketch, "E344", {"start": v(9.44, -15.32) * mm, "mid": v(9.42, -15) * mm, "end": v(9.25, -14.75) * mm});
            skArc(sketch, "E345", {"start": v(9.72, -15.71) * mm, "mid": v(9.65, -15.47) * mm, "end": v(9.44, -15.32) * mm});
            skArc(sketch, "E346", {"start": v(9.72, -15.71) * mm, "mid": v(9.47, -16.38) * mm, "end": v(9.57, -17.08) * mm});
            skArc(sketch, "E347", {"start": v(9.57, -18.09) * mm, "mid": v(9.63, -17.58) * mm, "end": v(9.57, -17.08) * mm});
            skArc(sketch, "E348", {"start": v(9.89, -18.66) * mm, "mid": v(9.8, -18.34) * mm, "end": v(9.57, -18.09) * mm});
            skLineSegment(sketch, "E349", {"start": v(0.03, -19.55) * mm, "end": v(-3.86, -19.74) * mm});
            skLineSegment(sketch, "E350", {"start": v(-3.86, -19.74) * mm, "end": v(-3.8, -18.8) * mm});
            skLineSegment(sketch, "E351", {"start": v(-3.8, -18.8) * mm, "end": v(-2.84, -16.95) * mm});
            skLineSegment(sketch, "E352", {"start": v(0.03, -19.55) * mm, "end": v(-0.1, -20.44) * mm});
            skLineSegment(sketch, "E353", {"start": v(-0.1, -20.44) * mm, "end": v(0.29, -20.83) * mm});
            skLineSegment(sketch, "E354", {"start": v(0.29, -20.83) * mm, "end": v(0.53, -21.46) * mm});
            skLineSegment(sketch, "E355", {"start": v(0.53, -21.46) * mm, "end": v(0.96, -21.02) * mm});
            skArc(sketch, "E356", {"start": v(0.96, -21.02) * mm, "mid": v(1.25, -21.07) * mm, "end": v(1.55, -21.02) * mm});
            skArc(sketch, "E357", {"start": v(2.3, -21.02) * mm, "mid": v(1.92, -20.86) * mm, "end": v(1.55, -21.02) * mm});
            skLineSegment(sketch, "E358", {"start": v(2.98, -20.86) * mm, "end": v(2.87, -20.99) * mm});
            skLineSegment(sketch, "E359", {"start": v(2.87, -20.99) * mm, "end": v(2.3, -21.02) * mm});
            skArc(sketch, "E360", {"start": v(-11.19, -12.81) * mm, "mid": v(-10.61, -13.27) * mm, "end": v(-9.92, -13.52) * mm});
            skArc(sketch, "E361", {"start": v(-11.19, -12.81) * mm, "mid": v(-11.43, -12.8) * mm, "end": v(-11.59, -12.98) * mm});
            skArc(sketch, "E362", {"start": v(-12, -12.96) * mm, "mid": v(-12.3, -12.82) * mm, "end": v(-12.54, -13.02) * mm});
            skLineSegment(sketch, "E363", {"start": v(-11.59, -12.98) * mm, "end": v(-12, -12.96) * mm});
            skLineSegment(sketch, "E364", {"start": v(-12.54, -13.02) * mm, "end": v(-12.75, -12.92) * mm});
            skLineSegment(sketch, "E365", {"start": v(-12.75, -12.92) * mm, "end": v(-13.22, -12.93) * mm});
            skLineSegment(sketch, "E366", {"start": v(-13.22, -12.93) * mm, "end": v(-13.29, -13.16) * mm});
            skLineSegment(sketch, "E367", {"start": v(-13.29, -13.16) * mm, "end": v(-13.54, -13.28) * mm});
            skLineSegment(sketch, "E368", {"start": v(-13.54, -13.28) * mm, "end": v(-14.66, -12.96) * mm});
            skLineSegment(sketch, "E369", {"start": v(-14.66, -12.96) * mm, "end": v(-14.8, -12.76) * mm});
            skLineSegment(sketch, "E370", {"start": v(-14.8, -12.76) * mm, "end": v(-14.93, -12.77) * mm});
            skLineSegment(sketch, "E371", {"start": v(-14.93, -12.77) * mm, "end": v(-15.16, -13.2) * mm});
            skLineSegment(sketch, "E372", {"start": v(-15.16, -13.2) * mm, "end": v(-15.31, -13.26) * mm});
            skLineSegment(sketch, "E373", {"start": v(-15.31, -13.26) * mm, "end": v(-15.82, -13.07) * mm});
            skLineSegment(sketch, "E374", {"start": v(-15.82, -13.07) * mm, "end": v(-15.89, -12.81) * mm});
            skLineSegment(sketch, "E375", {"start": v(-15.89, -12.81) * mm, "end": v(-16.24, -12.8) * mm});
            skLineSegment(sketch, "E376", {"start": v(-16.24, -12.8) * mm, "end": v(-16.35, -12.73) * mm});
            skLineSegment(sketch, "E377", {"start": v(-16.35, -12.73) * mm, "end": v(-16.63, -13) * mm});
            skLineSegment(sketch, "E378", {"start": v(-16.63, -13) * mm, "end": v(-16.9, -12.9) * mm});
            skLineSegment(sketch, "E379", {"start": v(-16.9, -12.9) * mm, "end": v(-16.93, -12.67) * mm});
            skLineSegment(sketch, "E380", {"start": v(-16.93, -12.67) * mm, "end": v(-17.29, -12.27) * mm});
            skLineSegment(sketch, "E381", {"start": v(-17.29, -12.27) * mm, "end": v(-17.66, -12.2) * mm});
            skLineSegment(sketch, "E382", {"start": v(-17.66, -12.2) * mm, "end": v(-17.88, -12.4) * mm});
            skLineSegment(sketch, "E383", {"start": v(-17.88, -12.4) * mm, "end": v(-18.23, -12.16) * mm});
            skLineSegment(sketch, "E384", {"start": v(-18.23, -12.16) * mm, "end": v(-18.62, -12.12) * mm});
            skLineSegment(sketch, "E385", {"start": v(-18.62, -12.12) * mm, "end": v(-18.9, -12) * mm});
            skLineSegment(sketch, "E386", {"start": v(-18.9, -12) * mm, "end": v(-19.35, -11.96) * mm});
            skLineSegment(sketch, "E387", {"start": v(-19.35, -11.96) * mm, "end": v(-19.36, -11.53) * mm});
            skLineSegment(sketch, "E388", {"start": v(-19.36, -11.53) * mm, "end": v(-19.6, -11.42) * mm});
            skLineSegment(sketch, "E389", {"start": v(-19.6, -11.42) * mm, "end": v(-19.64, -11.56) * mm});
            skLineSegment(sketch, "E390", {"start": v(-19.64, -11.56) * mm, "end": v(-19.82, -11.57) * mm});
            skLineSegment(sketch, "E391", {"start": v(-19.82, -11.57) * mm, "end": v(-20.01, -11.34) * mm});
            skLineSegment(sketch, "E392", {"start": v(-20.01, -11.34) * mm, "end": v(-20.1, -11.56) * mm});
            skLineSegment(sketch, "E393", {"start": v(-20.1, -11.56) * mm, "end": v(-20.24, -11.57) * mm});
            skLineSegment(sketch, "E394", {"start": v(-20.24, -11.57) * mm, "end": v(-20.87, -11) * mm});
            skLineSegment(sketch, "E395", {"start": v(-8.35, -23.12) * mm, "end": v(-7.92, -22.97) * mm});
            skLineSegment(sketch, "E396", {"start": v(-7.92, -22.97) * mm, "end": v(-6.97, -22.9) * mm});
            skLineSegment(sketch, "E397", {"start": v(-6.97, -22.9) * mm, "end": v(-5.83, -23.3) * mm});
            skLineSegment(sketch, "E398", {"start": v(-5.83, -23.3) * mm, "end": v(-5.15, -23.42) * mm});
            skLineSegment(sketch, "E399", {"start": v(-5.15, -23.42) * mm, "end": v(-4.63, -23.18) * mm});
            skLineSegment(sketch, "E400", {"start": v(-4.63, -23.18) * mm, "end": v(-4.86, -23.05) * mm});
            skLineSegment(sketch, "E401", {"start": v(-4.86, -23.05) * mm, "end": v(-4.8, -22.87) * mm});
            skLineSegment(sketch, "E402", {"start": v(-4.8, -22.87) * mm, "end": v(-4.46, -22.75) * mm});
            skLineSegment(sketch, "E403", {"start": v(-4.46, -22.75) * mm, "end": v(-4.26, -22.9) * mm});
            skLineSegment(sketch, "E404", {"start": v(-4.26, -22.9) * mm, "end": v(-4.03, -22.78) * mm});
            skLineSegment(sketch, "E405", {"start": v(-4.03, -22.78) * mm, "end": v(-3.7, -22.86) * mm});
            skLineSegment(sketch, "E406", {"start": v(-3.7, -22.86) * mm, "end": v(-3.5, -23.18) * mm});
            skLineSegment(sketch, "E407", {"start": v(-3.5, -23.18) * mm, "end": v(-3.5, -23.41) * mm});
            skLineSegment(sketch, "E408", {"start": v(-3.5, -23.41) * mm, "end": v(-3, -23.42) * mm});
            skLineSegment(sketch, "E409", {"start": v(-3, -23.42) * mm, "end": v(-2.8, -23.6) * mm});
            skLineSegment(sketch, "E410", {"start": v(-2.8, -23.6) * mm, "end": v(-2.98, -23.89) * mm});
            skLineSegment(sketch, "E411", {"start": v(-2.98, -23.89) * mm, "end": v(-1.92, -24.48) * mm});
            skLineSegment(sketch, "E412", {"start": v(-1.92, -24.48) * mm, "end": v(-1.5, -24.32) * mm});
            skLineSegment(sketch, "E413", {"start": v(-1.5, -24.32) * mm, "end": v(-1.42, -24.06) * mm});
            skLineSegment(sketch, "E414", {"start": v(-1.42, -24.06) * mm, "end": v(-1.1, -24) * mm});
            skLineSegment(sketch, "E415", {"start": v(-1.1, -24) * mm, "end": v(-0.96, -23.82) * mm});
            skLineSegment(sketch, "E416", {"start": v(-0.96, -23.82) * mm, "end": v(-0.77, -23.94) * mm});
            skLineSegment(sketch, "E417", {"start": v(-0.77, -23.94) * mm, "end": v(-0.7, -24.24) * mm});
            skLineSegment(sketch, "E418", {"start": v(-0.7, -24.24) * mm, "end": v(-0.57, -24.3) * mm});
            skLineSegment(sketch, "E419", {"start": v(-0.57, -24.3) * mm, "end": v(-0.29, -23.92) * mm});
            skLineSegment(sketch, "E420", {"start": v(-0.29, -23.92) * mm, "end": v(-0.29, -23.84) * mm});
            skLineSegment(sketch, "E421", {"start": v(-0.29, -23.84) * mm, "end": v(-0.42, -23.8) * mm});
            skLineSegment(sketch, "E422", {"start": v(-0.42, -23.8) * mm, "end": v(-0.35, -23.68) * mm});
            skLineSegment(sketch, "E423", {"start": v(-0.35, -23.68) * mm, "end": v(-0.31, -23.44) * mm});
            skLineSegment(sketch, "E424", {"start": v(-0.31, -23.44) * mm, "end": v(-0.1, -23.41) * mm});
            skLineSegment(sketch, "E425", {"start": v(-0.1, -23.41) * mm, "end": v(0.03, -23.26) * mm});
            skLineSegment(sketch, "E426", {"start": v(0.03, -23.26) * mm, "end": v(0.13, -23.35) * mm});
            skLineSegment(sketch, "E427", {"start": v(0.13, -23.35) * mm, "end": v(0.1, -23.65) * mm});
            skLineSegment(sketch, "E428", {"start": v(0.1, -23.65) * mm, "end": v(0.46, -23.72) * mm});
            skLineSegment(sketch, "E429", {"start": v(0.46, -23.72) * mm, "end": v(1.08, -24) * mm});
            skLineSegment(sketch, "E430", {"start": v(1.08, -24) * mm, "end": v(1.16, -24.14) * mm});
            skLineSegment(sketch, "E431", {"start": v(1.16, -24.14) * mm, "end": v(1.5, -24.14) * mm});
            skLineSegment(sketch, "E432", {"start": v(1.5, -24.14) * mm, "end": v(1.63, -24.24) * mm});
            skLineSegment(sketch, "E433", {"start": v(1.63, -24.24) * mm, "end": v(1.88, -23.92) * mm});
            skLineSegment(sketch, "E434", {"start": v(1.88, -23.92) * mm, "end": v(1.87, -23.78) * mm});
            skLineSegment(sketch, "E435", {"start": v(1.87, -23.78) * mm, "end": v(1.72, -23.75) * mm});
            skLineSegment(sketch, "E436", {"start": v(1.72, -23.75) * mm, "end": v(1.37, -23.45) * mm});
            skLineSegment(sketch, "E437", {"start": v(1.37, -23.45) * mm, "end": v(0.7, -23.33) * mm});
            skLineSegment(sketch, "E438", {"start": v(0.7, -23.33) * mm, "end": v(0.37, -23.13) * mm});
            skLineSegment(sketch, "E439", {"start": v(0.37, -23.13) * mm, "end": v(0.6, -22.75) * mm});
            skLineSegment(sketch, "E440", {"start": v(0.6, -22.75) * mm, "end": v(0.56, -22.6) * mm});
            skLineSegment(sketch, "E441", {"start": v(0.56, -22.6) * mm, "end": v(0.9, -22.6) * mm});
            skLineSegment(sketch, "E442", {"start": v(0.9, -22.6) * mm, "end": v(1.1, -22.32) * mm});
            skLineSegment(sketch, "E443", {"start": v(1.1, -22.32) * mm, "end": v(0.92, -21.77) * mm});
            skLineSegment(sketch, "E444", {"start": v(0.92, -21.77) * mm, "end": v(0.58, -21.94) * mm});
            skLineSegment(sketch, "E445", {"start": v(0.58, -21.94) * mm, "end": v(0.54, -22.28) * mm});
            skLineSegment(sketch, "E446", {"start": v(0.54, -22.28) * mm, "end": v(0.18, -22.22) * mm});
            skLineSegment(sketch, "E447", {"start": v(0.18, -22.22) * mm, "end": v(0.07, -22) * mm});
            skLineSegment(sketch, "E448", {"start": v(0.07, -22) * mm, "end": v(0.53, -21.46) * mm});
            skLineSegment(sketch, "E449", {"start": v(-2.84, -16.95) * mm, "end": v(-2.93, -16.7) * mm});
            skLineSegment(sketch, "E450", {"start": v(-2.93, -16.7) * mm, "end": v(-2.77, -16.68) * mm});
            skLineSegment(sketch, "E451", {"start": v(-2.77, -16.68) * mm, "end": v(-2.79, -16.37) * mm});
            skLineSegment(sketch, "E452", {"start": v(-2.79, -16.37) * mm, "end": v(-2.97, -16.2) * mm});
            skLineSegment(sketch, "E453", {"start": v(-2.97, -16.2) * mm, "end": v(-2.98, -15.9) * mm});
            skLineSegment(sketch, "E454", {"start": v(-2.98, -15.9) * mm, "end": v(-3.19, -15.36) * mm});
            skLineSegment(sketch, "E455", {"start": v(-3.19, -15.36) * mm, "end": v(-3.14, -14.82) * mm});
            skLineSegment(sketch, "E456", {"start": v(-3.14, -14.82) * mm, "end": v(-3.1, -14.19) * mm});
            skLineSegment(sketch, "E457", {"start": v(-3.1, -14.19) * mm, "end": v(-3.24, -13.4) * mm});
            skLineSegment(sketch, "E458", {"start": v(-3.24, -13.4) * mm, "end": v(-3.17, -12.49) * mm});
            skLineSegment(sketch, "E459", {"start": v(-3.17, -12.49) * mm, "end": v(-2.77, -12.18) * mm});
            skLineSegment(sketch, "E460", {"start": v(-2.77, -12.18) * mm, "end": v(-2.81, -11.98) * mm});
            skLineSegment(sketch, "E461", {"start": v(-2.81, -11.98) * mm, "end": v(-2.48, -11.43) * mm});
            skLineSegment(sketch, "E462", {"start": v(-2.48, -11.43) * mm, "end": v(-2.1, -11.3) * mm});
            skLineSegment(sketch, "E463", {"start": v(-2.1, -11.3) * mm, "end": v(-2.17, -10.8) * mm});
            skLineSegment(sketch, "E464", {"start": v(-2.17, -10.8) * mm, "end": v(-1.85, -10.23) * mm});
            skLineSegment(sketch, "E465", {"start": v(-1.85, -10.23) * mm, "end": v(-1.7, -10.15) * mm});
            skLineSegment(sketch, "E466", {"start": v(-1.7, -10.15) * mm, "end": v(-1.58, -9.98) * mm});
            skLineSegment(sketch, "E467", {"start": v(-1.58, -9.98) * mm, "end": v(-1.64, -9.77) * mm});
            skLineSegment(sketch, "E468", {"start": v(-1.64, -9.77) * mm, "end": v(-1.3, -9.38) * mm});
            skLineSegment(sketch, "E469", {"start": v(-1.3, -9.38) * mm, "end": v(-1.2, -8.88) * mm});
            skLineSegment(sketch, "E470", {"start": v(-1.2, -8.88) * mm, "end": v(-1.33, -8.5) * mm});
            skLineSegment(sketch, "E471", {"start": v(-1.33, -8.5) * mm, "end": v(-0.88, -8.3) * mm});
            skLineSegment(sketch, "E472", {"start": v(-0.88, -8.3) * mm, "end": v(-0.7, -7.34) * mm});
            skLineSegment(sketch, "E473", {"start": v(-0.47, -6.02) * mm, "end": v(-0.47, -6.7) * mm});
            skLineSegment(sketch, "E474", {"start": v(-0.47, -6.7) * mm, "end": v(-0.7, -7.34) * mm});
            skLineSegment(sketch, "E475", {"start": v(-0.47, -6.02) * mm, "end": v(0.2, -5.56) * mm});
            skLineSegment(sketch, "E476", {"start": v(0.2, -5.56) * mm, "end": v(0.24, -5.16) * mm});
            skLineSegment(sketch, "E477", {"start": v(0.24, -5.16) * mm, "end": v(0.32, -4.98) * mm});
            skLineSegment(sketch, "E478", {"start": v(0.32, -4.98) * mm, "end": v(0.31, -4.82) * mm});
            skLineSegment(sketch, "E479", {"start": v(0.31, -4.82) * mm, "end": v(0.14, -4.77) * mm});
            skLineSegment(sketch, "E480", {"start": v(0.14, -4.77) * mm, "end": v(-0.15, -4.76) * mm});
            skLineSegment(sketch, "E481", {"start": v(-0.15, -4.76) * mm, "end": v(-0.54, -4.1) * mm});
            skLineSegment(sketch, "E482", {"start": v(-0.54, -4.1) * mm, "end": v(-0.86, -2.83) * mm});
            skLineSegment(sketch, "E483", {"start": v(-0.86, -2.83) * mm, "end": v(-1.27, -2.79) * mm});
            skLineSegment(sketch, "E484", {"start": v(-1.27, -2.79) * mm, "end": v(-2.14, -2.16) * mm});
            skLineSegment(sketch, "E485", {"start": v(-2.14, -2.16) * mm, "end": v(-2.32, -1.76) * mm});
            skLineSegment(sketch, "E486", {"start": v(-2.32, -1.76) * mm, "end": v(-2.08, -0.98) * mm});
            skLineSegment(sketch, "E487", {"start": v(-2.08, -0.98) * mm, "end": v(-1.93, -0.37) * mm});
            skLineSegment(sketch, "E488", {"start": v(-1.93, -0.37) * mm, "end": v(-2.94, -0.13) * mm});
            skLineSegment(sketch, "E489", {"start": v(-2.94, -0.13) * mm, "end": v(-2.97, 0.53) * mm});
            skLineSegment(sketch, "E490", {"start": v(-2.97, 0.53) * mm, "end": v(-3.57, 0.87) * mm});
            skLineSegment(sketch, "E491", {"start": v(-3.57, 0.87) * mm, "end": v(-4.37, 1.7) * mm});
            skLineSegment(sketch, "E492", {"start": v(-4.37, 1.7) * mm, "end": v(-4.69, 3.02) * mm});
            skLineSegment(sketch, "E493", {"start": v(-4.69, 3.02) * mm, "end": v(-4.6, 3.23) * mm});
            skLineSegment(sketch, "E494", {"start": v(-4.6, 3.23) * mm, "end": v(-4.44, 3.42) * mm});
            skLineSegment(sketch, "E495", {"start": v(-4.44, 3.42) * mm, "end": v(-4.45, 3.79) * mm});
            skLineSegment(sketch, "E496", {"start": v(-4.45, 3.79) * mm, "end": v(-4.05, 4) * mm});
            skLineSegment(sketch, "E497", {"start": v(-5.16, 3.82) * mm, "end": v(-4.6, 3.23) * mm});
            skLineSegment(sketch, "E498", {"start": v(-4.05, 4) * mm, "end": v(-4.05, 4.4) * mm});
            skLineSegment(sketch, "E499", {"start": v(-4.05, 4.4) * mm, "end": v(-3.78, 4.59) * mm});
            skLineSegment(sketch, "E500", {"start": v(-3.78, 4.59) * mm, "end": v(-3.71, 5.07) * mm});
            skLineSegment(sketch, "E501", {"start": v(-3.71, 5.07) * mm, "end": v(-4.03, 5.32) * mm});
            skLineSegment(sketch, "E502", {"start": v(-4.03, 5.32) * mm, "end": v(-3.9, 5.8) * mm});
            skLineSegment(sketch, "E503", {"start": v(-3.9, 5.8) * mm, "end": v(-2.85, 6.22) * mm});
            skLineSegment(sketch, "E504", {"start": v(-2.85, 6.22) * mm, "end": v(-2.51, 7.51) * mm});
            skLineSegment(sketch, "E505", {"start": v(-2.51, 7.51) * mm, "end": v(-2.97, 8.03) * mm});
            skLineSegment(sketch, "E506", {"start": v(-2.97, 8.03) * mm, "end": v(-3, 8.2) * mm});
            skLineSegment(sketch, "E507", {"start": v(-3, 8.2) * mm, "end": v(-3.4, 8.42) * mm});
            skLineSegment(sketch, "E508", {"start": v(-3.4, 8.42) * mm, "end": v(-3.38, 8.64) * mm});
            skLineSegment(sketch, "E509", {"start": v(-3.52, 8.87) * mm, "end": v(-4.14, 9.08) * mm});
            skLineSegment(sketch, "E510", {"start": v(-3.52, 8.87) * mm, "end": v(-3.38, 8.64) * mm});
            skLineSegment(sketch, "E511", {"start": v(-4.14, 9.08) * mm, "end": v(-4.4, 9.53) * mm});
            skLineSegment(sketch, "E512", {"start": v(-4.4, 9.53) * mm, "end": v(-4.42, 9.87) * mm});
            skLineSegment(sketch, "E513", {"start": v(-4.42, 9.87) * mm, "end": v(-4.22, 10.23) * mm});
            skLineSegment(sketch, "E514", {"start": v(-4.22, 10.23) * mm, "end": v(-4.23, 10.4) * mm});
            skLineSegment(sketch, "E515", {"start": v(-4.23, 10.4) * mm, "end": v(-4.5, 10.58) * mm});
            skLineSegment(sketch, "E516", {"start": v(-4.5, 10.58) * mm, "end": v(-4.62, 10.94) * mm});
            skLineSegment(sketch, "E517", {"start": v(2.82, 1.31) * mm, "end": v(2.34, 7.08) * mm});
            skLineSegment(sketch, "E518", {"start": v(2.34, 7.08) * mm, "end": v(2.93, 6.89) * mm});
            skLineSegment(sketch, "E519", {"start": v(2.93, 6.89) * mm, "end": v(3.57, 7.23) * mm});
            skLineSegment(sketch, "E520", {"start": v(1.55, 8.92) * mm, "end": v(1.7, 8.3) * mm});
            skLineSegment(sketch, "E521", {"start": v(1.7, 8.3) * mm, "end": v(1.98, 7.88) * mm});
            skLineSegment(sketch, "E522", {"start": v(1.98, 7.88) * mm, "end": v(2.19, 7.18) * mm});
            skLineSegment(sketch, "E523", {"start": v(2.19, 7.18) * mm, "end": v(2.34, 7.08) * mm});
            skLineSegment(sketch, "E524", {"start": v(-11.6, 24.05) * mm, "end": v(-11.53, 24.95) * mm});
            skLineSegment(sketch, "E525", {"start": v(-11.53, 24.95) * mm, "end": v(-11.14, 24.87) * mm});
            skLineSegment(sketch, "E526", {"start": v(-11.14, 24.87) * mm, "end": v(-10.9, 23.64) * mm});
            skLineSegment(sketch, "E527", {"start": v(-10.9, 23.64) * mm, "end": v(-10.66, 23.37) * mm});
            skLineSegment(sketch, "E528", {"start": v(-10.66, 23.37) * mm, "end": v(-10.13, 23.38) * mm});
            skLineSegment(sketch, "E529", {"start": v(-10.13, 23.38) * mm, "end": v(-10.12, 23.23) * mm});
            skLineSegment(sketch, "E530", {"start": v(-10.12, 23.23) * mm, "end": v(-9.44, 23.18) * mm});
            skLineSegment(sketch, "E531", {"start": v(-9.44, 23.18) * mm, "end": v(-9.45, 22.93) * mm});
            skLineSegment(sketch, "E532", {"start": v(-9.45, 22.93) * mm, "end": v(-8.8, 22.95) * mm});
            skLineSegment(sketch, "E533", {"start": v(-8.8, 22.95) * mm, "end": v(-8.68, 23.2) * mm});
            skLineSegment(sketch, "E534", {"start": v(-8.68, 23.2) * mm, "end": v(-8.46, 23.28) * mm});
            skLineSegment(sketch, "E535", {"start": v(-8.46, 23.28) * mm, "end": v(-8.3, 23.17) * mm});
            skLineSegment(sketch, "E536", {"start": v(-8.3, 23.17) * mm, "end": v(-7.99, 23.17) * mm});
            skLineSegment(sketch, "E537", {"start": v(-7.99, 23.17) * mm, "end": v(-6.73, 22.55) * mm});
            skLineSegment(sketch, "E538", {"start": v(-6.73, 22.55) * mm, "end": v(-6.5, 22.6) * mm});
            skLineSegment(sketch, "E539", {"start": v(-6.5, 22.6) * mm, "end": v(-6.47, 22.43) * mm});
            skLineSegment(sketch, "E540", {"start": v(-6.47, 22.43) * mm, "end": v(-6.15, 22.28) * mm});
            skLineSegment(sketch, "E541", {"start": v(-6.15, 22.28) * mm, "end": v(-6.02, 22.27) * mm});
            skLineSegment(sketch, "E542", {"start": v(-6.02, 22.27) * mm, "end": v(-5.98, 22.08) * mm});
            skLineSegment(sketch, "E543", {"start": v(-5.98, 22.08) * mm, "end": v(-5.69, 21.96) * mm});
            skLineSegment(sketch, "E544", {"start": v(-5.69, 21.96) * mm, "end": v(-5.44, 21.92) * mm});
            skLineSegment(sketch, "E545", {"start": v(-5.44, 21.92) * mm, "end": v(-5.23, 21.97) * mm});
            skLineSegment(sketch, "E546", {"start": v(-5.23, 21.97) * mm, "end": v(-4.7, 22.42) * mm});
            skLineSegment(sketch, "E547", {"start": v(-4.7, 22.42) * mm, "end": v(-4.51, 22.43) * mm});
            skLineSegment(sketch, "E548", {"start": v(-4.51, 22.43) * mm, "end": v(-4.4, 22.15) * mm});
            skLineSegment(sketch, "E549", {"start": v(-4.4, 22.15) * mm, "end": v(-4.24, 22.08) * mm});
            skLineSegment(sketch, "E550", {"start": v(-4.24, 22.08) * mm, "end": v(-4.1, 22.2) * mm});
            skLineSegment(sketch, "E551", {"start": v(-4.1, 22.2) * mm, "end": v(-3.2, 22.21) * mm});
            skLineSegment(sketch, "E552", {"start": v(-3.2, 22.21) * mm, "end": v(-3, 21.93) * mm});
            skLineSegment(sketch, "E553", {"start": v(-3, 21.93) * mm, "end": v(-2.83, 21.9) * mm});
            skLineSegment(sketch, "E554", {"start": v(-2.83, 21.9) * mm, "end": v(-2.74, 22) * mm});
            skLineSegment(sketch, "E555", {"start": v(-2.74, 22) * mm, "end": v(-2.33, 22.04) * mm});
            skLineSegment(sketch, "E556", {"start": v(-2.33, 22.04) * mm, "end": v(-2.55, 21.8) * mm});
            skLineSegment(sketch, "E557", {"start": v(-2.55, 21.8) * mm, "end": v(-3.02, 21.62) * mm});
            skLineSegment(sketch, "E558", {"start": v(-3.02, 21.62) * mm, "end": v(-4.26, 21.05) * mm});
            skLineSegment(sketch, "E559", {"start": v(-4.26, 21.05) * mm, "end": v(-4.63, 20.8) * mm});
            skLineSegment(sketch, "E560", {"start": v(-4.63, 20.8) * mm, "end": v(-4.87, 20.44) * mm});
            skLineSegment(sketch, "E561", {"start": v(-4.87, 20.44) * mm, "end": v(-5.24, 19.86) * mm});
            skLineSegment(sketch, "E562", {"start": v(-5.24, 19.86) * mm, "end": v(-5.4, 19.82) * mm});
            skLineSegment(sketch, "E563", {"start": v(-5.4, 19.82) * mm, "end": v(-5.9, 19.2) * mm});
            skLineSegment(sketch, "E564", {"start": v(-5.9, 19.2) * mm, "end": v(-6.22, 19.22) * mm});
            skLineSegment(sketch, "E565", {"start": v(-6.22, 19.22) * mm, "end": v(-6.47, 18.92) * mm});
            skLineSegment(sketch, "E566", {"start": v(-6.47, 18.92) * mm, "end": v(-6.4, 18.77) * mm});
            skLineSegment(sketch, "E567", {"start": v(-6.4, 18.77) * mm, "end": v(-5.94, 18.73) * mm});
            skLineSegment(sketch, "E568", {"start": v(-5.94, 18.73) * mm, "end": v(-4.34, 19.42) * mm});
            skLineSegment(sketch, "E569", {"start": v(-4.34, 19.42) * mm, "end": v(-4.12, 19.25) * mm});
            skLineSegment(sketch, "E570", {"start": v(-4.12, 19.25) * mm, "end": v(-4.48, 18.67) * mm});
            skLineSegment(sketch, "E571", {"start": v(-4.48, 18.67) * mm, "end": v(-4.44, 18.48) * mm});
            skLineSegment(sketch, "E572", {"start": v(-4.44, 18.48) * mm, "end": v(-4.17, 18.63) * mm});
            skLineSegment(sketch, "E573", {"start": v(-4.17, 18.63) * mm, "end": v(-3.84, 18.63) * mm});
            skLineSegment(sketch, "E574", {"start": v(-3.84, 18.63) * mm, "end": v(-3.7, 18.39) * mm});
            skLineSegment(sketch, "E575", {"start": v(-3.7, 18.39) * mm, "end": v(-3.63, 18.39) * mm});
            skLineSegment(sketch, "E576", {"start": v(-3.63, 18.39) * mm, "end": v(-3.45, 18.6) * mm});
            skLineSegment(sketch, "E577", {"start": v(-3.45, 18.6) * mm, "end": v(-3.11, 18.73) * mm});
            skLineSegment(sketch, "E578", {"start": v(-3.11, 18.73) * mm, "end": v(-2.62, 19) * mm});
            skLineSegment(sketch, "E579", {"start": v(-2.62, 19) * mm, "end": v(-2.65, 19.1) * mm});
            skLineSegment(sketch, "E580", {"start": v(-2.65, 19.1) * mm, "end": v(-2.55, 19.2) * mm});
            skLineSegment(sketch, "E581", {"start": v(-2.55, 19.2) * mm, "end": v(-1.85, 19.3) * mm});
            skLineSegment(sketch, "E582", {"start": v(-1.85, 19.3) * mm, "end": v(-1.2, 19.73) * mm});
            skLineSegment(sketch, "E583", {"start": v(-1.2, 19.73) * mm, "end": v(-0.93, 20.22) * mm});
            skLineSegment(sketch, "E584", {"start": v(-0.93, 20.22) * mm, "end": v(-0.73, 20.28) * mm});
            skLineSegment(sketch, "E585", {"start": v(-0.73, 20.28) * mm, "end": v(-0.35, 20.74) * mm});
            skLineSegment(sketch, "E586", {"start": v(-0.35, 20.74) * mm, "end": v(0.07, 21.01) * mm});
            skLineSegment(sketch, "E587", {"start": v(0.07, 21.01) * mm, "end": v(0.61, 21.09) * mm});
            skLineSegment(sketch, "E588", {"start": v(0.61, 21.09) * mm, "end": v(0.8, 20.97) * mm});
            skLineSegment(sketch, "E589", {"start": v(0.8, 20.97) * mm, "end": v(0.76, 20.84) * mm});
            skLineSegment(sketch, "E590", {"start": v(0.76, 20.84) * mm, "end": v(0.37, 20.74) * mm});
            skLineSegment(sketch, "E591", {"start": v(0.37, 20.74) * mm, "end": v(0.17, 20.38) * mm});
            skLineSegment(sketch, "E592", {"start": v(0.17, 20.38) * mm, "end": v(-0.07, 20.25) * mm});
            skLineSegment(sketch, "E593", {"start": v(-0.07, 20.25) * mm, "end": v(-0.11, 20.08) * mm});
            skLineSegment(sketch, "E594", {"start": v(-0.11, 20.08) * mm, "end": v(-0.42, 19.63) * mm});
            skLineSegment(sketch, "E595", {"start": v(-0.42, 19.63) * mm, "end": v(-0.4, 19.37) * mm});
            skLineSegment(sketch, "E596", {"start": v(-0.4, 19.37) * mm, "end": v(-0.33, 19.31) * mm});
            skLineSegment(sketch, "E597", {"start": v(-0.33, 19.31) * mm, "end": v(0.17, 19.78) * mm});
            skLineSegment(sketch, "E598", {"start": v(0.17, 19.78) * mm, "end": v(0.31, 19.63) * mm});
            skLineSegment(sketch, "E599", {"start": v(0.31, 19.63) * mm, "end": v(1.04, 19.46) * mm});
            skLineSegment(sketch, "E600", {"start": v(1.04, 19.46) * mm, "end": v(1.5, 18.8) * mm});
            skLineSegment(sketch, "E601", {"start": v(1.5, 18.8) * mm, "end": v(2, 18.8) * mm});
            skLineSegment(sketch, "E602", {"start": v(16, 10.2) * mm, "end": v(15.46, 9.72) * mm});
            skLineSegment(sketch, "E603", {"start": v(15.46, 9.72) * mm, "end": v(14.8, 9.28) * mm});
            skLineSegment(sketch, "E604", {"start": v(14.8, 9.28) * mm, "end": v(15.65, 3.84) * mm});
            skLineSegment(sketch, "E605", {"start": v(15.65, 3.84) * mm, "end": v(24.25, 5.44) * mm});
            skLineSegment(sketch, "E606", {"start": v(24.25, 5.44) * mm, "end": v(25.1, 2.45) * mm});
            skLineSegment(sketch, "E607", {"start": v(25.1, 2.45) * mm, "end": v(26.28, 2.67) * mm});
            skLineSegment(sketch, "E608", {"start": v(30.42, 11.06) * mm, "end": v(30.1, 12.57) * mm});
            skLineSegment(sketch, "E609", {"start": v(30.1, 12.57) * mm, "end": v(30.75, 12.75) * mm});
            skLineSegment(sketch, "E610", {"start": v(30.75, 12.75) * mm, "end": v(31.56, 11.72) * mm});
            skLineSegment(sketch, "E611", {"start": v(31.56, 11.72) * mm, "end": v(31.1, 11.43) * mm});
            skLineSegment(sketch, "E612", {"start": v(31.1, 11.43) * mm, "end": v(31, 11.26) * mm});
            skLineSegment(sketch, "E613", {"start": v(31, 11.26) * mm, "end": v(30.42, 11.06) * mm});
            skLineSegment(sketch, "E614", {"start": v(30.42, 11.06) * mm, "end": v(30.35, 10.91) * mm});
            skLineSegment(sketch, "E615", {"start": v(30.35, 10.91) * mm, "end": v(28.66, 10.3) * mm});
            skLineSegment(sketch, "E616", {"start": v(28.66, 10.3) * mm, "end": v(28.6, 10.36) * mm});
            skLineSegment(sketch, "E617", {"start": v(28.6, 10.36) * mm, "end": v(28, 9.79) * mm});
            skLineSegment(sketch, "E618", {"start": v(28, 9.79) * mm, "end": v(27.42, 9.44) * mm});
            skLineSegment(sketch, "E619", {"start": v(30.1, 12.57) * mm, "end": v(27.06, 11.96) * mm});
            skLineSegment(sketch, "E620", {"start": v(27.06, 13.72) * mm, "end": v(30.57, 14.55) * mm});
            skLineSegment(sketch, "E621", {"start": v(30.57, 14.55) * mm, "end": v(30.82, 14.9) * mm});
            skLineSegment(sketch, "E622", {"start": v(30.82, 14.9) * mm, "end": v(31.22, 15.05) * mm});
            skLineSegment(sketch, "E623", {"start": v(31.22, 15.05) * mm, "end": v(31.5, 14.62) * mm});
            skLineSegment(sketch, "E624", {"start": v(31.5, 14.62) * mm, "end": v(31.26, 13.9) * mm});
            skLineSegment(sketch, "E625", {"start": v(31.26, 13.9) * mm, "end": v(31.46, 13.6) * mm});
            skLineSegment(sketch, "E626", {"start": v(31.46, 13.6) * mm, "end": v(31.57, 13.68) * mm});
            skLineSegment(sketch, "E627", {"start": v(31.57, 13.68) * mm, "end": v(31.8, 13.63) * mm});
            skLineSegment(sketch, "E628", {"start": v(31.8, 13.63) * mm, "end": v(32.42, 12.72) * mm});
            skLineSegment(sketch, "E629", {"start": v(32.42, 12.72) * mm, "end": v(32.89, 12.67) * mm});
            skLineSegment(sketch, "E630", {"start": v(32.89, 12.67) * mm, "end": v(33.14, 12.8) * mm});
            skLineSegment(sketch, "E631", {"start": v(33.14, 12.8) * mm, "end": v(33.26, 12.93) * mm});
            skLineSegment(sketch, "E632", {"start": v(31.56, 11.72) * mm, "end": v(31.87, 11.84) * mm});
            skLineSegment(sketch, "E633", {"start": v(31.87, 11.84) * mm, "end": v(31.84, 12.11) * mm});
            skLineSegment(sketch, "E634", {"start": v(31.84, 12.11) * mm, "end": v(32.24, 12.39) * mm});
            skLineSegment(sketch, "E635", {"start": v(32.24, 12.39) * mm, "end": v(32.36, 11.91) * mm});
            skLineSegment(sketch, "E636", {"start": v(32.36, 11.91) * mm, "end": v(32.6, 12.19) * mm});
            skLineSegment(sketch, "E637", {"start": v(32.6, 12.19) * mm, "end": v(32.93, 12.39) * mm});
            skLineSegment(sketch, "E638", {"start": v(32.93, 12.39) * mm, "end": v(33.31, 12.53) * mm});
            skLineSegment(sketch, "E639", {"start": v(33.31, 12.53) * mm, "end": v(33.54, 12.6) * mm});
            skLineSegment(sketch, "E640", {"start": v(33.54, 12.6) * mm, "end": v(33.5, 13) * mm});
            skLineSegment(sketch, "E641", {"start": v(33.5, 13) * mm, "end": v(33.31, 13.25) * mm});
            skLineSegment(sketch, "E642", {"start": v(33.26, 12.93) * mm, "end": v(33.31, 13.25) * mm});
            skLineSegment(sketch, "E643", {"start": v(25.7, 18.98) * mm, "end": v(28.63, 19.8) * mm});
            skLineSegment(sketch, "E644", {"start": v(28.63, 19.8) * mm, "end": v(28.76, 19.52) * mm});
            skLineSegment(sketch, "E645", {"start": v(28.76, 19.52) * mm, "end": v(28.66, 19.11) * mm});
            skLineSegment(sketch, "E646", {"start": v(28.66, 19.11) * mm, "end": v(28.93, 18.8) * mm});
            skLineSegment(sketch, "E647", {"start": v(28.93, 18.8) * mm, "end": v(28.87, 18.71) * mm});
            skLineSegment(sketch, "E648", {"start": v(28.87, 18.71) * mm, "end": v(28.94, 18.56) * mm});
            skLineSegment(sketch, "E649", {"start": v(28.94, 18.56) * mm, "end": v(28.47, 18.03) * mm});
            skLineSegment(sketch, "E650", {"start": v(28.47, 18.03) * mm, "end": v(28.22, 17.92) * mm});
            skLineSegment(sketch, "E651", {"start": v(28.22, 17.92) * mm, "end": v(28.22, 17.72) * mm});
            skLineSegment(sketch, "E652", {"start": v(28.22, 17.72) * mm, "end": v(28.33, 17.6) * mm});
            skLineSegment(sketch, "E653", {"start": v(28.33, 17.6) * mm, "end": v(28.22, 15.03) * mm});
            skLineSegment(sketch, "E654", {"start": v(28.22, 15.03) * mm, "end": v(28.33, 14.99) * mm});
            skLineSegment(sketch, "E655", {"start": v(28.33, 14.99) * mm, "end": v(28.31, 14.46) * mm});
            skLineSegment(sketch, "E656", {"start": v(28.31, 14.46) * mm, "end": v(28.31, 14.23) * mm});
            skLineSegment(sketch, "E657", {"start": v(28.31, 14.23) * mm, "end": v(28.5, 14.06) * mm});
            skLineSegment(sketch, "E658", {"start": v(0.14, -4.77) * mm, "end": v(0.38, -4.41) * mm});
            skLineSegment(sketch, "E659", {"start": v(0.38, -4.41) * mm, "end": v(0.68, -4.22) * mm});
            skLineSegment(sketch, "E660", {"start": v(0.68, -4.22) * mm, "end": v(1.5, -4.52) * mm});
            skLineSegment(sketch, "E661", {"start": v(1.5, -4.52) * mm, "end": v(1.6, -4.35) * mm});
            skLineSegment(sketch, "E662", {"start": v(1.6, -4.35) * mm, "end": v(1.44, -4.1) * mm});
            skLineSegment(sketch, "E663", {"start": v(1.44, -4.1) * mm, "end": v(1.48, -3.72) * mm});
            skLineSegment(sketch, "E664", {"start": v(1.48, -3.72) * mm, "end": v(1.86, -3.53) * mm});
            skLineSegment(sketch, "E665", {"start": v(1.86, -3.53) * mm, "end": v(2.17, -3.37) * mm});
            skLineSegment(sketch, "E666", {"start": v(2.17, -3.37) * mm, "end": v(1.96, -3) * mm});
            skLineSegment(sketch, "E667", {"start": v(1.96, -3) * mm, "end": v(2.17, -2.8) * mm});
            skLineSegment(sketch, "E668", {"start": v(2.17, -2.8) * mm, "end": v(2.24, -2.52) * mm});
            skLineSegment(sketch, "E669", {"start": v(2.24, -2.52) * mm, "end": v(2.3, -1.55) * mm});
            skLineSegment(sketch, "E670", {"start": v(2.3, -1.55) * mm, "end": v(3, -0.48) * mm});
            skLineSegment(sketch, "E671", {"start": v(3, -0.48) * mm, "end": v(2.95, 0.27) * mm});
            skLineSegment(sketch, "E672", {"start": v(2.95, 0.27) * mm, "end": v(2.7, 0.65) * mm});
            skLineSegment(sketch, "E673", {"start": v(2.7, 0.65) * mm, "end": v(2.82, 1.31) * mm});
            skLineSegment(sketch, "E674", {"start": v(2.24, -2.52) * mm, "end": v(3.54, -2.2) * mm});
            skLineSegment(sketch, "E675", {"start": v(3.54, -2.2) * mm, "end": v(3.99, -2.54) * mm});
            skLineSegment(sketch, "E676", {"start": v(3.99, -2.54) * mm, "end": v(4.13, -2.17) * mm});
            skLineSegment(sketch, "E677", {"start": v(4.13, -2.17) * mm, "end": v(4.5, -2) * mm});
            skLineSegment(sketch, "E678", {"start": v(4.5, -2) * mm, "end": v(4.81, -2.27) * mm});
            skLineSegment(sketch, "E679", {"start": v(4.81, -2.27) * mm, "end": v(4.98, -2.24) * mm});
            skLineSegment(sketch, "E680", {"start": v(4.98, -2.24) * mm, "end": v(5.05, -1.82) * mm});
            skLineSegment(sketch, "E681", {"start": v(5.05, -1.82) * mm, "end": v(5.43, -1.57) * mm});
            skLineSegment(sketch, "E682", {"start": v(5.43, -1.57) * mm, "end": v(5.57, -1.74) * mm});
            skLineSegment(sketch, "E683", {"start": v(5.57, -1.74) * mm, "end": v(6.07, -1.77) * mm});
            skLineSegment(sketch, "E684", {"start": v(6.07, -1.77) * mm, "end": v(6.11, -1.2) * mm});
            skLineSegment(sketch, "E685", {"start": v(6.11, -1.2) * mm, "end": v(7, -0.45) * mm});
            skLineSegment(sketch, "E686", {"start": v(7, -0.45) * mm, "end": v(7, 0.08) * mm});
            skLineSegment(sketch, "E687", {"start": v(7, 0.08) * mm, "end": v(7.37, 0.06) * mm});
            skLineSegment(sketch, "E688", {"start": v(7.37, 0.06) * mm, "end": v(8.07, 0.47) * mm});
            skLineSegment(sketch, "E689", {"start": v(8.07, 0.47) * mm, "end": v(8.06, 0.7) * mm});
            skLineSegment(sketch, "E690", {"start": v(8.06, 0.7) * mm, "end": v(7.8, 0.9) * mm});
            skLineSegment(sketch, "E691", {"start": v(7.8, 0.9) * mm, "end": v(7.93, 1.1) * mm});
            skLineSegment(sketch, "E692", {"start": v(10.12, -8.77) * mm, "end": v(10.05, -8.16) * mm});
            skLineSegment(sketch, "E693", {"start": v(10.05, -8.16) * mm, "end": v(10.62, -7.98) * mm});
            skLineSegment(sketch, "E694", {"start": v(10.62, -7.98) * mm, "end": v(10.6, -7.65) * mm});
            skLineSegment(sketch, "E695", {"start": v(10.6, -7.65) * mm, "end": v(11.1, -7.23) * mm});
            skLineSegment(sketch, "E696", {"start": v(11.1, -7.23) * mm, "end": v(11.6, -7.2) * mm});
            skLineSegment(sketch, "E697", {"start": v(11.6, -7.2) * mm, "end": v(11.97, -6.75) * mm});
            skLineSegment(sketch, "E698", {"start": v(11.97, -6.75) * mm, "end": v(12.52, -6.48) * mm});
            skLineSegment(sketch, "E699", {"start": v(12.52, -6.48) * mm, "end": v(12.55, -6.14) * mm});
            skLineSegment(sketch, "E700", {"start": v(12.55, -6.14) * mm, "end": v(13.06, -5.7) * mm});
            skLineSegment(sketch, "E701", {"start": v(13.06, -5.7) * mm, "end": v(13.17, -5.86) * mm});
            skLineSegment(sketch, "E702", {"start": v(13.17, -5.86) * mm, "end": v(13.4, -5.89) * mm});
            skLineSegment(sketch, "E703", {"start": v(13.4, -5.89) * mm, "end": v(13.61, -5.39) * mm});
            skLineSegment(sketch, "E704", {"start": v(13.61, -5.39) * mm, "end": v(14.09, -5.39) * mm});
            skLineSegment(sketch, "E705", {"start": v(14.09, -5.39) * mm, "end": v(14.26, -5) * mm});
            skLineSegment(sketch, "E706", {"start": v(14.26, -5) * mm, "end": v(14.6, -4.77) * mm});
            skLineSegment(sketch, "E707", {"start": v(14.6, -4.77) * mm, "end": v(14.63, -4.22) * mm});
            skLineSegment(sketch, "E708", {"start": v(11.04, -4.69) * mm, "end": v(12.23, -3.87) * mm});
            skLineSegment(sketch, "E709", {"start": v(12.23, -3.87) * mm, "end": v(12.2, -3.6) * mm});
            skLineSegment(sketch, "E710", {"start": v(12.2, -3.6) * mm, "end": v(13.7, -2.01) * mm});
            skLineSegment(sketch, "E711", {"start": v(13.7, -2.01) * mm, "end": v(12.76, -1.18) * mm});
            skLineSegment(sketch, "E712", {"start": v(12.76, -1.18) * mm, "end": v(12.7, -0.9) * mm});
            skLineSegment(sketch, "E713", {"start": v(12.7, -0.9) * mm, "end": v(12.37, 0.02) * mm});
            skLineSegment(sketch, "E714", {"start": v(12.37, 0.02) * mm, "end": v(11.76, 0.4) * mm});
            skLineSegment(sketch, "E715", {"start": v(11.76, 0.4) * mm, "end": v(11.6, 0.77) * mm});
            skLineSegment(sketch, "E716", {"start": v(11.6, 0.77) * mm, "end": v(10.98, 0.28) * mm});
            skLineSegment(sketch, "E717", {"start": v(10.98, 0.28) * mm, "end": v(10.83, 0.44) * mm});
            skLineSegment(sketch, "E718", {"start": v(10.83, 0.44) * mm, "end": v(10.51, 0.5) * mm});
            skLineSegment(sketch, "E719", {"start": v(10.51, 0.5) * mm, "end": v(10.15, 0.28) * mm});
            skLineSegment(sketch, "E720", {"start": v(10.15, 0.28) * mm, "end": v(9.86, 0.56) * mm});
            skLineSegment(sketch, "E721", {"start": v(9.86, 0.56) * mm, "end": v(9.23, 0.58) * mm});
            skLineSegment(sketch, "E722", {"start": v(9.23, 0.58) * mm, "end": v(8.93, 1.07) * mm});
            skLineSegment(sketch, "E723", {"start": v(8.93, 1.07) * mm, "end": v(8.7, 1.19) * mm});
            skLineSegment(sketch, "E724", {"start": v(8.7, 1.19) * mm, "end": v(7.93, 1.1) * mm});
            skLineSegment(sketch, "E725", {"start": v(24.25, 5.44) * mm, "end": v(24.68, 5.73) * mm});
            skLineSegment(sketch, "E726", {"start": v(24.68, 5.73) * mm, "end": v(25.24, 5.95) * mm});
            skLineSegment(sketch, "E727", {"start": v(25.24, 5.95) * mm, "end": v(25.92, 6.88) * mm});
            skLineSegment(sketch, "E728", {"start": v(25.92, 6.88) * mm, "end": v(25.3, 7.41) * mm});
            skLineSegment(sketch, "E729", {"start": v(25.3, 7.41) * mm, "end": v(25.17, 7.73) * mm});
            skLineSegment(sketch, "E730", {"start": v(25.17, 7.73) * mm, "end": v(24.9, 7.7) * mm});
            skLineSegment(sketch, "E731", {"start": v(24.9, 7.7) * mm, "end": v(24.78, 8.18) * mm});
            skLineSegment(sketch, "E732", {"start": v(24.78, 8.18) * mm, "end": v(25.02, 8.27) * mm});
            skLineSegment(sketch, "E733", {"start": v(25.02, 8.27) * mm, "end": v(25, 8.54) * mm});
            skLineSegment(sketch, "E734", {"start": v(25, 8.54) * mm, "end": v(24.82, 8.67) * mm});
            skLineSegment(sketch, "E735", {"start": v(24.82, 8.67) * mm, "end": v(25.1, 9.16) * mm});
            skLineSegment(sketch, "E736", {"start": v(25.1, 9.16) * mm, "end": v(25.16, 9.55) * mm});
            skLineSegment(sketch, "E737", {"start": v(25.16, 9.55) * mm, "end": v(25.37, 9.77) * mm});
            skLineSegment(sketch, "E738", {"start": v(24.88, 5.81) * mm, "end": v(24.8, 5.23) * mm});
            skLineSegment(sketch, "E739", {"start": v(24.8, 5.23) * mm, "end": v(25.11, 4.85) * mm});
            skLineSegment(sketch, "E740", {"start": v(25.11, 4.85) * mm, "end": v(25.76, 4.5) * mm});
            skLineSegment(sketch, "E741", {"start": v(25.76, 4.5) * mm, "end": v(26.24, 4.44) * mm});
            skLineSegment(sketch, "E742", {"start": v(26.24, 4.44) * mm, "end": v(26.23, 4.23) * mm});
            skLineSegment(sketch, "E743", {"start": v(26.23, 4.23) * mm, "end": v(26.16, 4.17) * mm});
            skLineSegment(sketch, "E744", {"start": v(26.16, 4.17) * mm, "end": v(26.17, 3.85) * mm});
            skLineSegment(sketch, "E745", {"start": v(26.17, 3.85) * mm, "end": v(26.5, 4.09) * mm});
            skLineSegment(sketch, "E746", {"start": v(26.5, 4.09) * mm, "end": v(26.59, 4.58) * mm});
            skLineSegment(sketch, "E747", {"start": v(26.59, 4.58) * mm, "end": v(27.01, 5.29) * mm});
            skLineSegment(sketch, "E748", {"start": v(27.01, 5.29) * mm, "end": v(27.32, 6.03) * mm});
            skLineSegment(sketch, "E749", {"start": v(27.32, 6.03) * mm, "end": v(27.28, 6.6) * mm});
            skLineSegment(sketch, "E750", {"start": v(27.28, 6.6) * mm, "end": v(27.28, 7.67) * mm});
            skLineSegment(sketch, "E751", {"start": v(27.28, 7.67) * mm, "end": v(27.11, 7.96) * mm});
            skLineSegment(sketch, "E752", {"start": v(27.11, 7.96) * mm, "end": v(26.71, 7.83) * mm});
            skLineSegment(sketch, "E753", {"start": v(26.71, 7.83) * mm, "end": v(26.64, 7.93) * mm});
            skLineSegment(sketch, "E754", {"start": v(26.64, 7.93) * mm, "end": v(26.96, 8.19) * mm});
            skLineSegment(sketch, "E755", {"start": v(26.96, 8.19) * mm, "end": v(27, 8.37) * mm});
            skLineSegment(sketch, "E756", {"start": v(12.37, 0.02) * mm, "end": v(12.7, 0.15) * mm});
            skLineSegment(sketch, "E757", {"start": v(12.7, 0.15) * mm, "end": v(12.78, 0.52) * mm});
            skLineSegment(sketch, "E758", {"start": v(12.78, 0.52) * mm, "end": v(12.93, 0.58) * mm});
            skLineSegment(sketch, "E759", {"start": v(12.93, 0.58) * mm, "end": v(13.02, 1.57) * mm});
            skLineSegment(sketch, "E760", {"start": v(13.02, 1.57) * mm, "end": v(13.24, 1.62) * mm});
            skLineSegment(sketch, "E761", {"start": v(13.24, 1.62) * mm, "end": v(13.42, 1.37) * mm});
            skLineSegment(sketch, "E762", {"start": v(13.42, 1.37) * mm, "end": v(13.62, 1.47) * mm});
            skLineSegment(sketch, "E763", {"start": v(13.62, 1.47) * mm, "end": v(13.63, 1.61) * mm});
            skLineSegment(sketch, "E764", {"start": v(13.63, 1.61) * mm, "end": v(13.46, 1.89) * mm});
            skLineSegment(sketch, "E765", {"start": v(13.46, 1.89) * mm, "end": v(14.06, 2.77) * mm});
            skLineSegment(sketch, "E766", {"start": v(14.06, 2.77) * mm, "end": v(14.23, 2.69) * mm});
            skLineSegment(sketch, "E767", {"start": v(14.23, 2.69) * mm, "end": v(15.1, 3.62) * mm});
            skLineSegment(sketch, "E768", {"start": v(15.1, 3.62) * mm, "end": v(15.18, 5.37) * mm});
            skLineSegment(sketch, "E769", {"start": v(15.18, 5.37) * mm, "end": v(15.02, 5.8) * mm});
            skLineSegment(sketch, "E770", {"start": v(15.02, 5.8) * mm, "end": v(15.32, 5.97) * mm});
            skLineSegment(sketch, "E771", {"start": v(9.6, 7.85) * mm, "end": v(10.25, 7.6) * mm});
            skLineSegment(sketch, "E772", {"start": v(10.25, 7.6) * mm, "end": v(10.84, 7.63) * mm});
            skLineSegment(sketch, "E773", {"start": v(10.84, 7.63) * mm, "end": v(11.26, 7.3) * mm});
            skLineSegment(sketch, "E774", {"start": v(11.26, 7.3) * mm, "end": v(11.49, 7.36) * mm});
            skLineSegment(sketch, "E775", {"start": v(11.49, 7.36) * mm, "end": v(12.1, 7.64) * mm});
            skLineSegment(sketch, "E776", {"start": v(12.1, 7.64) * mm, "end": v(12.8, 7.75) * mm});
            skLineSegment(sketch, "E777", {"start": v(12.8, 7.75) * mm, "end": v(13.6, 8.59) * mm});
            skLineSegment(sketch, "E778", {"start": v(13.6, 8.59) * mm, "end": v(14.8, 9.28) * mm});
            skLineSegment(sketch, "E779", {"start": v(-4.62, 10.94) * mm, "end": v(-4.75, 11.77) * mm});
            skLineSegment(sketch, "E780", {"start": v(-4.75, 11.77) * mm, "end": v(-4.88, 12.07) * mm});
            skLineSegment(sketch, "E781", {"start": v(-4.88, 12.07) * mm, "end": v(-5.65, 12.47) * mm});
            skLineSegment(sketch, "E782", {"start": v(-5.65, 12.47) * mm, "end": v(-6.08, 13.16) * mm});
            skLineSegment(sketch, "E783", {"start": v(-6.08, 13.16) * mm, "end": v(-6.6, 13.21) * mm});
            skLineSegment(sketch, "E784", {"start": v(-6.6, 13.21) * mm, "end": v(-6.73, 13.6) * mm});
            skLineSegment(sketch, "E785", {"start": v(-6.73, 13.6) * mm, "end": v(-7, 13.58) * mm});
            skLineSegment(sketch, "E786", {"start": v(-7, 13.58) * mm, "end": v(-7.3, 13.85) * mm});
            skLineSegment(sketch, "E787", {"start": v(-7.3, 13.85) * mm, "end": v(-7.43, 15.1) * mm});
            skLineSegment(sketch, "E788", {"start": v(-7.43, 15.1) * mm, "end": v(-7.26, 15.36) * mm});
            skLineSegment(sketch, "E789", {"start": v(-7.26, 15.36) * mm, "end": v(-7.3, 15.79) * mm});
            skLineSegment(sketch, "E790", {"start": v(-7.3, 15.79) * mm, "end": v(-7.66, 16) * mm});
            skLineSegment(sketch, "E791", {"start": v(-7.66, 16) * mm, "end": v(-7.4, 16.72) * mm});
            skLineSegment(sketch, "E792", {"start": v(-7.4, 16.72) * mm, "end": v(-6.68, 17.24) * mm});
            skLineSegment(sketch, "E793", {"start": v(-6.68, 17.24) * mm, "end": v(-6.68, 18.53) * mm});
            skLineSegment(sketch, "E794", {"start": v(-6.68, 18.53) * mm, "end": v(-6.4, 18.77) * mm});
            skLineSegment(sketch, "E795", {"start": v(-3.45, 18.6) * mm, "end": v(-3.04, 17.94) * mm});
            skLineSegment(sketch, "E796", {"start": v(-3.04, 17.94) * mm, "end": v(-2.34, 17.87) * mm});
            skLineSegment(sketch, "E797", {"start": v(-2.34, 17.87) * mm, "end": v(-1.19, 17.57) * mm});
            skLineSegment(sketch, "E798", {"start": v(-1.19, 17.57) * mm, "end": v(-0.92, 17.39) * mm});
            skLineSegment(sketch, "E799", {"start": v(-0.92, 17.39) * mm, "end": v(0.5, 17.15) * mm});
            skLineSegment(sketch, "E800", {"start": v(0.5, 17.15) * mm, "end": v(0.58, 16.87) * mm});
            skLineSegment(sketch, "E801", {"start": v(0.58, 16.87) * mm, "end": v(1, 16.75) * mm});
            skLineSegment(sketch, "E802", {"start": v(1, 16.75) * mm, "end": v(1.12, 15.67) * mm});
            skLineSegment(sketch, "E803", {"start": v(1.12, 15.67) * mm, "end": v(1.47, 15.34) * mm});
            skLineSegment(sketch, "E804", {"start": v(2, 18.8) * mm, "end": v(2.13, 18.9) * mm});
            skLineSegment(sketch, "E805", {"start": v(2.13, 18.9) * mm, "end": v(2.42, 18.68) * mm});
            skLineSegment(sketch, "E806", {"start": v(2.42, 18.68) * mm, "end": v(2.65, 18.83) * mm});
            skLineSegment(sketch, "E807", {"start": v(2.65, 18.83) * mm, "end": v(2.8, 18.76) * mm});
            skLineSegment(sketch, "E808", {"start": v(2.8, 18.76) * mm, "end": v(3.42, 19.3) * mm});
            skLineSegment(sketch, "E809", {"start": v(3.42, 19.3) * mm, "end": v(3.83, 19.41) * mm});
            skLineSegment(sketch, "E810", {"start": v(3.83, 19.41) * mm, "end": v(4.45, 19.46) * mm});
            skLineSegment(sketch, "E811", {"start": v(4.45, 19.46) * mm, "end": v(5.24, 19.79) * mm});
            skLineSegment(sketch, "E812", {"start": v(5.24, 19.79) * mm, "end": v(5.43, 19.75) * mm});
            skLineSegment(sketch, "E813", {"start": v(5.43, 19.75) * mm, "end": v(5.4, 19.17) * mm});
            skLineSegment(sketch, "E814", {"start": v(5.4, 19.17) * mm, "end": v(5.86, 19.03) * mm});
            skLineSegment(sketch, "E815", {"start": v(5.86, 19.03) * mm, "end": v(6.73, 19.28) * mm});
            skLineSegment(sketch, "E816", {"start": v(6.73, 19.28) * mm, "end": v(6.82, 19.4) * mm});
            skLineSegment(sketch, "E817", {"start": v(6.82, 19.4) * mm, "end": v(6.98, 19.34) * mm});
            skLineSegment(sketch, "E818", {"start": v(6.98, 19.34) * mm, "end": v(6.98, 18.62) * mm});
            skLineSegment(sketch, "E819", {"start": v(6.98, 18.62) * mm, "end": v(7.51, 18.06) * mm});
            skLineSegment(sketch, "E820", {"start": v(7.51, 18.06) * mm, "end": v(7.05, 18.08) * mm});
            skLineSegment(sketch, "E821", {"start": v(7.05, 18.08) * mm, "end": v(6.85, 18) * mm});
            skLineSegment(sketch, "E822", {"start": v(6.85, 18) * mm, "end": v(6.51, 18.04) * mm});
            skLineSegment(sketch, "E823", {"start": v(6.51, 18.04) * mm, "end": v(6.2, 17.86) * mm});
            skLineSegment(sketch, "E824", {"start": v(6.2, 17.86) * mm, "end": v(5.48, 17.99) * mm});
            skLineSegment(sketch, "E825", {"start": v(5.48, 17.99) * mm, "end": v(4.77, 17.99) * mm});
            skLineSegment(sketch, "E826", {"start": v(4.77, 17.99) * mm, "end": v(4.58, 17.7) * mm});
            skLineSegment(sketch, "E827", {"start": v(4.58, 17.7) * mm, "end": v(3.55, 17.6) * mm});
            skLineSegment(sketch, "E828", {"start": v(3.55, 17.6) * mm, "end": v(3.34, 17.16) * mm});
            skLineSegment(sketch, "E829", {"start": v(3.34, 17.16) * mm, "end": v(3.25, 17.1) * mm});
            skLineSegment(sketch, "E830", {"start": v(3.25, 17.1) * mm, "end": v(2.99, 17.27) * mm});
            skLineSegment(sketch, "E831", {"start": v(2.99, 17.27) * mm, "end": v(2.48, 17.03) * mm});
            skLineSegment(sketch, "E832", {"start": v(2.48, 17.03) * mm, "end": v(2.26, 17.2) * mm});
            skLineSegment(sketch, "E833", {"start": v(2.26, 17.2) * mm, "end": v(2.2, 17.2) * mm});
            skLineSegment(sketch, "E834", {"start": v(2.2, 17.2) * mm, "end": v(1.47, 15.34) * mm});
            skLineSegment(sketch, "E835", {"start": v(1.47, 15.34) * mm, "end": v(0.77, 14.22) * mm});
            skLineSegment(sketch, "E836", {"start": v(0.77, 14.22) * mm, "end": v(0.8, 13.98) * mm});
            skLineSegment(sketch, "E837", {"start": v(0.8, 13.98) * mm, "end": v(0.99, 13.92) * mm});
            skLineSegment(sketch, "E838", {"start": v(0.99, 13.92) * mm, "end": v(1.05, 14.2) * mm});
            skLineSegment(sketch, "E839", {"start": v(1.05, 14.2) * mm, "end": v(1.56, 14.62) * mm});
            skLineSegment(sketch, "E840", {"start": v(1.56, 14.62) * mm, "end": v(2.37, 15.84) * mm});
            skLineSegment(sketch, "E841", {"start": v(2.37, 15.84) * mm, "end": v(2.46, 15.54) * mm});
            skLineSegment(sketch, "E842", {"start": v(2.46, 15.54) * mm, "end": v(1.79, 14.16) * mm});
            skLineSegment(sketch, "E843", {"start": v(1.79, 14.16) * mm, "end": v(1.67, 13.5) * mm});
            skLineSegment(sketch, "E844", {"start": v(1.67, 13.5) * mm, "end": v(1.76, 13.4) * mm});
            skLineSegment(sketch, "E845", {"start": v(1.76, 13.4) * mm, "end": v(1.8, 13.14) * mm});
            skLineSegment(sketch, "E846", {"start": v(1.8, 13.14) * mm, "end": v(1.47, 12.69) * mm});
            skLineSegment(sketch, "E847", {"start": v(1.47, 12.69) * mm, "end": v(1.63, 11.8) * mm});
            skLineSegment(sketch, "E848", {"start": v(1.63, 11.8) * mm, "end": v(1.28, 10.84) * mm});
            skLineSegment(sketch, "E849", {"start": v(1.28, 10.84) * mm, "end": v(1.41, 10.44) * mm});
            skLineSegment(sketch, "E850", {"start": v(1.41, 10.44) * mm, "end": v(1.46, 9.85) * mm});
            skLineSegment(sketch, "E851", {"start": v(1.46, 9.85) * mm, "end": v(1.66, 9.42) * mm});
            skLineSegment(sketch, "E852", {"start": v(1.66, 9.42) * mm, "end": v(1.55, 8.92) * mm});
            skLineSegment(sketch, "E853", {"start": v(31.22, 15.05) * mm, "end": v(31.38, 15.61) * mm});
            skLineSegment(sketch, "E854", {"start": v(31.38, 15.61) * mm, "end": v(31.08, 15.73) * mm});
            skLineSegment(sketch, "E855", {"start": v(31.08, 15.73) * mm, "end": v(31.07, 16.07) * mm});
            skLineSegment(sketch, "E856", {"start": v(31.07, 16.07) * mm, "end": v(30.67, 16.18) * mm});
            skLineSegment(sketch, "E857", {"start": v(30.67, 16.18) * mm, "end": v(29.22, 20.64) * mm});
            skLineSegment(sketch, "E858", {"start": v(29.22, 20.64) * mm, "end": v(29.16, 20.4) * mm});
            skLineSegment(sketch, "E859", {"start": v(29.16, 20.4) * mm, "end": v(28.96, 20.56) * mm});
            skLineSegment(sketch, "E860", {"start": v(28.96, 20.56) * mm, "end": v(28.84, 20.52) * mm});
            skLineSegment(sketch, "E861", {"start": v(28.84, 20.52) * mm, "end": v(28.63, 19.8) * mm});
            skLineSegment(sketch, "E862", {"start": v(29.22, 20.64) * mm, "end": v(29.37, 20.7) * mm});
            skLineSegment(sketch, "E863", {"start": v(29.37, 20.7) * mm, "end": v(29.74, 20.63) * mm});
            skLineSegment(sketch, "E864", {"start": v(29.74, 20.63) * mm, "end": v(29.83, 21.58) * mm});
            skLineSegment(sketch, "E865", {"start": v(29.83, 21.58) * mm, "end": v(30.28, 22.6) * mm});
            skLineSegment(sketch, "E866", {"start": v(30.28, 22.6) * mm, "end": v(30.06, 22.84) * mm});
            skLineSegment(sketch, "E867", {"start": v(30.06, 22.84) * mm, "end": v(30.06, 23.5) * mm});
            skLineSegment(sketch, "E868", {"start": v(30.06, 23.5) * mm, "end": v(30.25, 23.82) * mm});
            skLineSegment(sketch, "E869", {"start": v(30.25, 23.82) * mm, "end": v(30.25, 24.68) * mm});
            skLineSegment(sketch, "E870", {"start": v(30.25, 24.68) * mm, "end": v(30.91, 26.51) * mm});
            skLineSegment(sketch, "E871", {"start": v(30.91, 26.51) * mm, "end": v(31.08, 26.53) * mm});
            skLineSegment(sketch, "E872", {"start": v(31.08, 26.53) * mm, "end": v(31.29, 26.12) * mm});
            skLineSegment(sketch, "E873", {"start": v(31.29, 26.12) * mm, "end": v(31.64, 26.05) * mm});
            skLineSegment(sketch, "E874", {"start": v(31.64, 26.05) * mm, "end": v(31.79, 26.18) * mm});
            skLineSegment(sketch, "E875", {"start": v(31.79, 26.18) * mm, "end": v(31.76, 26.35) * mm});
            skLineSegment(sketch, "E876", {"start": v(31.76, 26.35) * mm, "end": v(32.39, 26.78) * mm});
            skLineSegment(sketch, "E877", {"start": v(32.39, 26.78) * mm, "end": v(33.34, 26.44) * mm});
            skLineSegment(sketch, "E878", {"start": v(33.34, 26.44) * mm, "end": v(34.35, 23.1) * mm});
            skLineSegment(sketch, "E879", {"start": v(34.35, 23.1) * mm, "end": v(34.96, 23.1) * mm});
            skLineSegment(sketch, "E880", {"start": v(34.96, 23.1) * mm, "end": v(35.08, 22.98) * mm});
            skLineSegment(sketch, "E881", {"start": v(35.08, 22.98) * mm, "end": v(35.05, 22.39) * mm});
            skLineSegment(sketch, "E882", {"start": v(35.05, 22.39) * mm, "end": v(35.4, 22.1) * mm});
            skLineSegment(sketch, "E883", {"start": v(35.4, 22.1) * mm, "end": v(35.6, 22.08) * mm});
            skLineSegment(sketch, "E884", {"start": v(35.6, 22.08) * mm, "end": v(35.63, 22.27) * mm});
            skLineSegment(sketch, "E885", {"start": v(35.63, 22.27) * mm, "end": v(35.89, 22.3) * mm});
            skLineSegment(sketch, "E886", {"start": v(35.89, 22.3) * mm, "end": v(36.34, 21.64) * mm});
            skLineSegment(sketch, "E887", {"start": v(36.34, 21.64) * mm, "end": v(36.08, 20.94) * mm});
            skLineSegment(sketch, "E888", {"start": v(36.08, 20.94) * mm, "end": v(35.9, 20.94) * mm});
            skLineSegment(sketch, "E889", {"start": v(35.9, 20.94) * mm, "end": v(34.95, 19.9) * mm});
            skLineSegment(sketch, "E890", {"start": v(34.95, 19.9) * mm, "end": v(34.78, 20.02) * mm});
            skLineSegment(sketch, "E891", {"start": v(34.78, 20.02) * mm, "end": v(34.7, 20.18) * mm});
            skLineSegment(sketch, "E892", {"start": v(34.7, 20.18) * mm, "end": v(34.46, 20.17) * mm});
            skLineSegment(sketch, "E893", {"start": v(34.46, 20.17) * mm, "end": v(34.4, 20) * mm});
            skLineSegment(sketch, "E894", {"start": v(34.4, 20) * mm, "end": v(34.1, 19.67) * mm});
            skLineSegment(sketch, "E895", {"start": v(34.1, 19.67) * mm, "end": v(34.15, 19.5) * mm});
            skLineSegment(sketch, "E896", {"start": v(34.15, 19.5) * mm, "end": v(34.14, 19.16) * mm});
            skLineSegment(sketch, "E897", {"start": v(34.14, 19.16) * mm, "end": v(33.93, 19.18) * mm});
            skLineSegment(sketch, "E898", {"start": v(33.93, 19.18) * mm, "end": v(33.87, 19.43) * mm});
            skLineSegment(sketch, "E899", {"start": v(33.68, 19.44) * mm, "end": v(33.47, 19.79) * mm});
            skLineSegment(sketch, "E900", {"start": v(33.47, 19.79) * mm, "end": v(33.28, 19.69) * mm});
            skLineSegment(sketch, "E901", {"start": v(33.28, 19.69) * mm, "end": v(33.4, 19.5) * mm});
            skLineSegment(sketch, "E902", {"start": v(33.4, 19.5) * mm, "end": v(33.36, 19.06) * mm});
            skLineSegment(sketch, "E903", {"start": v(33.36, 19.06) * mm, "end": v(33.38, 18.73) * mm});
            skLineSegment(sketch, "E904", {"start": v(33.38, 18.73) * mm, "end": v(33.21, 18.44) * mm});
            skLineSegment(sketch, "E905", {"start": v(33.21, 18.44) * mm, "end": v(33, 18.42) * mm});
            skLineSegment(sketch, "E906", {"start": v(33, 18.42) * mm, "end": v(32.9, 18.4) * mm});
            skLineSegment(sketch, "E907", {"start": v(32.9, 18.4) * mm, "end": v(32.9, 18.08) * mm});
            skLineSegment(sketch, "E908", {"start": v(32.9, 18.08) * mm, "end": v(32.14, 17.68) * mm});
            skLineSegment(sketch, "E909", {"start": v(32.14, 17.68) * mm, "end": v(31.91, 17.8) * mm});
            skLineSegment(sketch, "E910", {"start": v(31.91, 17.8) * mm, "end": v(31.6, 17.44) * mm});
            skLineSegment(sketch, "E911", {"start": v(31.6, 17.44) * mm, "end": v(31.7, 17.06) * mm});
            skLineSegment(sketch, "E912", {"start": v(31.7, 17.06) * mm, "end": v(31.58, 16.96) * mm});
            skLineSegment(sketch, "E913", {"start": v(31.58, 16.96) * mm, "end": v(31.38, 15.61) * mm});
            skLineSegment(sketch, "E914", {"start": v(33.68, 19.44) * mm, "end": v(33.87, 19.43) * mm});
            skLineSegment(sketch, "E915", {"start": v(17.54, 4.19) * mm, "end": v(17.78, 2.91) * mm});
            skLineSegment(sketch, "E916", {"start": v(17.78, 2.91) * mm, "end": v(18.3, 3.62) * mm});
            skLineSegment(sketch, "E917", {"start": v(18.3, 3.62) * mm, "end": v(18.64, 3.55) * mm});
            skLineSegment(sketch, "E918", {"start": v(18.64, 3.55) * mm, "end": v(18.97, 4.02) * mm});
            skLineSegment(sketch, "E919", {"start": v(18.97, 4.02) * mm, "end": v(19.2, 3.94) * mm});
            skLineSegment(sketch, "E920", {"start": v(19.2, 3.94) * mm, "end": v(19.4, 4) * mm});
            skLineSegment(sketch, "E921", {"start": v(9.6, 7.85) * mm, "end": v(9.95, 8.72) * mm});
            skLineSegment(sketch, "E922", {"start": v(9.95, 8.72) * mm, "end": v(10.03, 9.32) * mm});
            skLineSegment(sketch, "E923", {"start": v(10.03, 9.32) * mm, "end": v(10.34, 9.62) * mm});
            skLineSegment(sketch, "E924", {"start": v(10.34, 9.62) * mm, "end": v(10.46, 10.03) * mm});
            skLineSegment(sketch, "E925", {"start": v(10.46, 10.03) * mm, "end": v(10.76, 10.45) * mm});
            skLineSegment(sketch, "E926", {"start": v(10.76, 10.45) * mm, "end": v(10.92, 11.08) * mm});
            skLineSegment(sketch, "E927", {"start": v(10.92, 11.08) * mm, "end": v(10.82, 11.67) * mm});
            skLineSegment(sketch, "E928", {"start": v(10.82, 11.67) * mm, "end": v(10.52, 12.6) * mm});
            skLineSegment(sketch, "E929", {"start": v(10.52, 12.6) * mm, "end": v(10.36, 13.25) * mm});
            skLineSegment(sketch, "E930", {"start": v(10.36, 13.25) * mm, "end": v(9.85, 13.79) * mm});
            skLineSegment(sketch, "E931", {"start": v(9.85, 13.79) * mm, "end": v(9.26, 13.45) * mm});
            skLineSegment(sketch, "E932", {"start": v(9.26, 13.45) * mm, "end": v(9.04, 12.8) * mm});
            skLineSegment(sketch, "E933", {"start": v(9.04, 12.8) * mm, "end": v(8.66, 12.42) * mm});
            skLineSegment(sketch, "E934", {"start": v(8.66, 12.42) * mm, "end": v(8.13, 12.62) * mm});
            skLineSegment(sketch, "E935", {"start": v(8.13, 12.62) * mm, "end": v(8.23, 13.27) * mm});
            skLineSegment(sketch, "E936", {"start": v(8.23, 13.27) * mm, "end": v(8.64, 13.4) * mm});
            skLineSegment(sketch, "E937", {"start": v(8.64, 13.4) * mm, "end": v(8.72, 14.06) * mm});
            skLineSegment(sketch, "E938", {"start": v(8.72, 14.06) * mm, "end": v(9.02, 14.2) * mm});
            skLineSegment(sketch, "E939", {"start": v(9.02, 14.2) * mm, "end": v(8.98, 15.3) * mm});
            skLineSegment(sketch, "E940", {"start": v(8.98, 15.3) * mm, "end": v(8.59, 15.68) * mm});
            skLineSegment(sketch, "E941", {"start": v(8.59, 15.68) * mm, "end": v(8.55, 15.86) * mm});
            skLineSegment(sketch, "E942", {"start": v(8.55, 15.86) * mm, "end": v(8.64, 16.04) * mm});
            skLineSegment(sketch, "E943", {"start": v(8.64, 16.04) * mm, "end": v(8.82, 16) * mm});
            skLineSegment(sketch, "E944", {"start": v(8.82, 16) * mm, "end": v(8.86, 16.14) * mm});
            skLineSegment(sketch, "E945", {"start": v(8.86, 16.14) * mm, "end": v(8.45, 16.7) * mm});
            skLineSegment(sketch, "E946", {"start": v(8.45, 16.7) * mm, "end": v(8, 16.73) * mm});
            skLineSegment(sketch, "E947", {"start": v(8, 16.73) * mm, "end": v(7.12, 17.2) * mm});
            skLineSegment(sketch, "E948", {"start": v(7.12, 17.2) * mm, "end": v(6.77, 17.25) * mm});
            skLineSegment(sketch, "E949", {"start": v(6.77, 17.25) * mm, "end": v(6.6, 17.15) * mm});
            skLineSegment(sketch, "E950", {"start": v(6.6, 17.15) * mm, "end": v(6.25, 17.44) * mm});
            skLineSegment(sketch, "E951", {"start": v(6.25, 17.44) * mm, "end": v(5.56, 17.07) * mm});
            skLineSegment(sketch, "E952", {"start": v(5.56, 17.07) * mm, "end": v(5.6, 16.65) * mm});
            skLineSegment(sketch, "E953", {"start": v(5.6, 16.65) * mm, "end": v(5.86, 16.6) * mm});
            skLineSegment(sketch, "E954", {"start": v(5.86, 16.6) * mm, "end": v(6.02, 16.42) * mm});
            skLineSegment(sketch, "E955", {"start": v(6.02, 16.42) * mm, "end": v(5.76, 16.3) * mm});
            skLineSegment(sketch, "E956", {"start": v(5.76, 16.3) * mm, "end": v(5.54, 16.34) * mm});
            skLineSegment(sketch, "E957", {"start": v(5.54, 16.34) * mm, "end": v(5.3, 16.06) * mm});
            skLineSegment(sketch, "E958", {"start": v(5.3, 16.06) * mm, "end": v(5.36, 15.13) * mm});
            skLineSegment(sketch, "E959", {"start": v(5.36, 15.13) * mm, "end": v(4.89, 14.81) * mm});
            skLineSegment(sketch, "E960", {"start": v(4.89, 14.81) * mm, "end": v(4.8, 15.3) * mm});
            skLineSegment(sketch, "E961", {"start": v(4.8, 15.3) * mm, "end": v(5.09, 15.82) * mm});
            skLineSegment(sketch, "E962", {"start": v(5.09, 15.82) * mm, "end": v(4.97, 15.94) * mm});
            skLineSegment(sketch, "E963", {"start": v(4.97, 15.94) * mm, "end": v(4.75, 15.86) * mm});
            skLineSegment(sketch, "E964", {"start": v(4.75, 15.86) * mm, "end": v(4.63, 15.47) * mm});
            skLineSegment(sketch, "E965", {"start": v(4.63, 15.47) * mm, "end": v(4.16, 15.1) * mm});
            skLineSegment(sketch, "E966", {"start": v(4.16, 15.1) * mm, "end": v(4.18, 14.93) * mm});
            skLineSegment(sketch, "E967", {"start": v(4.18, 14.93) * mm, "end": v(4.16, 14.6) * mm});
            skLineSegment(sketch, "E968", {"start": v(4.16, 14.6) * mm, "end": v(3.88, 14.58) * mm});
            skLineSegment(sketch, "E969", {"start": v(3.88, 14.58) * mm, "end": v(3.98, 14.12) * mm});
            skLineSegment(sketch, "E970", {"start": v(3.98, 14.12) * mm, "end": v(3.68, 13.12) * mm});
            skLineSegment(sketch, "E971", {"start": v(3.68, 13.12) * mm, "end": v(3.8, 12.34) * mm});
            skLineSegment(sketch, "E972", {"start": v(3.8, 12.34) * mm, "end": v(3.57, 11.77) * mm});
            skLineSegment(sketch, "E973", {"start": v(3.57, 11.77) * mm, "end": v(4.51, 9.87) * mm});
            skLineSegment(sketch, "E974", {"start": v(4.51, 9.87) * mm, "end": v(4.14, 8.2) * mm});
            skLineSegment(sketch, "E975", {"start": v(4.14, 8.2) * mm, "end": v(3.98, 7.72) * mm});
            skLineSegment(sketch, "E976", {"start": v(3.98, 7.72) * mm, "end": v(3.57, 7.23) * mm});
            skLineSegment(sketch, "E977", {"start": v(19.4, 4) * mm, "end": v(20, 4.44) * mm});
            skLineSegment(sketch, "E978", {"start": v(20, 4.44) * mm, "end": v(20.94, 3.85) * mm});
            skLineSegment(sketch, "E979", {"start": v(20.94, 3.85) * mm, "end": v(20.88, 3.28) * mm});
            skLineSegment(sketch, "E980", {"start": v(20.88, 3.28) * mm, "end": v(19.82, 3.76) * mm});
            skLineSegment(sketch, "E981", {"start": v(19.82, 3.76) * mm, "end": v(19.72, 3.1) * mm});
            skLineSegment(sketch, "E982", {"start": v(19.72, 3.1) * mm, "end": v(19.38, 2.48) * mm});
            skLineSegment(sketch, "E983", {"start": v(19.38, 2.48) * mm, "end": v(19.08, 2.25) * mm});
            skLineSegment(sketch, "E984", {"start": v(19.08, 2.25) * mm, "end": v(19.05, 2) * mm});
            skLineSegment(sketch, "E985", {"start": v(19.05, 2) * mm, "end": v(18.63, 1.91) * mm});
            skLineSegment(sketch, "E986", {"start": v(18.63, 1.91) * mm, "end": v(18.55, 1.03) * mm});
            skLineSegment(sketch, "E987", {"start": v(18.55, 1.03) * mm, "end": v(17.9, 1.34) * mm});
            skLineSegment(sketch, "E988", {"start": v(17.9, 1.34) * mm, "end": v(17.67, 1.33) * mm});
            skLineSegment(sketch, "E989", {"start": v(13.7, -2.01) * mm, "end": v(14.26, -2.54) * mm});
            skLineSegment(sketch, "E990", {"start": v(14.26, -2.54) * mm, "end": v(14.7, -2.64) * mm});
            skLineSegment(sketch, "E991", {"start": v(14.7, -2.64) * mm, "end": v(14.98, -2.28) * mm});
            skLineSegment(sketch, "E992", {"start": v(14.98, -2.28) * mm, "end": v(15.1, -2.47) * mm});
            skLineSegment(sketch, "E993", {"start": v(15.1, -2.47) * mm, "end": v(15.72, -2.38) * mm});
            skLineSegment(sketch, "E994", {"start": v(15.72, -2.38) * mm, "end": v(15.86, -1.84) * mm});
            skLineSegment(sketch, "E995", {"start": v(15.86, -1.84) * mm, "end": v(16.2, -1.91) * mm});
            skLineSegment(sketch, "E996", {"start": v(16.2, -1.91) * mm, "end": v(16.54, -1.69) * mm});
            skLineSegment(sketch, "E997", {"start": v(16.54, -1.69) * mm, "end": v(16.76, -1.72) * mm});
            skLineSegment(sketch, "E998", {"start": v(16.76, -1.72) * mm, "end": v(16.97, -1.25) * mm});
            skLineSegment(sketch, "E999", {"start": v(16.97, -1.25) * mm, "end": v(16.82, -1.08) * mm});
            skLineSegment(sketch, "E1000", {"start": v(16.82, -1.08) * mm, "end": v(17.68, 0.81) * mm});
            skLineSegment(sketch, "E1001", {"start": v(17.68, 0.81) * mm, "end": v(17.67, 1.33) * mm});
            skLineSegment(sketch, "E1002", {"start": v(24.8, 5.23) * mm, "end": v(24.67, 5.3) * mm});
            skLineSegment(sketch, "E1003", {"start": v(24.67, 5.3) * mm, "end": v(24.62, 5.12) * mm});
            skLineSegment(sketch, "E1004", {"start": v(24.62, 5.12) * mm, "end": v(24.9, 4.74) * mm});
            skLineSegment(sketch, "E1005", {"start": v(24.9, 4.74) * mm, "end": v(25.11, 4.66) * mm});
            skLineSegment(sketch, "E1006", {"start": v(25.11, 4.66) * mm, "end": v(25.54, 3.72) * mm});
            skLineSegment(sketch, "E1007", {"start": v(25.54, 3.72) * mm, "end": v(25.93, 3.44) * mm});
            skLineSegment(sketch, "E1008", {"start": v(25.93, 3.44) * mm, "end": v(26.06, 3.5) * mm});
            skLineSegment(sketch, "E1009", {"start": v(26.06, 3.5) * mm, "end": v(26.27, 2.74) * mm});
            skLineSegment(sketch, "E1010", {"start": v(26.27, 2.74) * mm, "end": v(26.28, 2.05) * mm});
            skLineSegment(sketch, "E1011", {"start": v(26.28, 2.05) * mm, "end": v(26.04, 1.22) * mm});
            skLineSegment(sketch, "E1012", {"start": v(26.04, 1.22) * mm, "end": v(25.72, 0.77) * mm});
            skLineSegment(sketch, "E1013", {"start": v(25.72, 0.77) * mm, "end": v(25.7, -0.11) * mm});
            skLineSegment(sketch, "E1014", {"start": v(25.7, -0.11) * mm, "end": v(25.42, -0.88) * mm});
            skLineSegment(sketch, "E1015", {"start": v(25.42, -0.88) * mm, "end": v(25.26, -0.88) * mm});
            skLineSegment(sketch, "E1016", {"start": v(25.26, -0.88) * mm, "end": v(25.12, -0.61) * mm});
            skLineSegment(sketch, "E1017", {"start": v(25.12, -0.61) * mm, "end": v(25.1, 0.24) * mm});
            skLineSegment(sketch, "E1018", {"start": v(25.1, 0.24) * mm, "end": v(25.4, 0.75) * mm});
            skLineSegment(sketch, "E1019", {"start": v(25.4, 0.75) * mm, "end": v(25.41, 1.27) * mm});
            skLineSegment(sketch, "E1020", {"start": v(25.41, 1.27) * mm, "end": v(25.21, 1.24) * mm});
            skLineSegment(sketch, "E1021", {"start": v(25.21, 1.24) * mm, "end": v(24.84, 1.9) * mm});
            skLineSegment(sketch, "E1022", {"start": v(24.84, 1.9) * mm, "end": v(24.75, 1.79) * mm});
            skLineSegment(sketch, "E1023", {"start": v(24.75, 1.79) * mm, "end": v(24.17, 1.8) * mm});
            skLineSegment(sketch, "E1024", {"start": v(24.17, 1.8) * mm, "end": v(23.97, 2.17) * mm});
            skLineSegment(sketch, "E1025", {"start": v(23.97, 2.17) * mm, "end": v(23.93, 2.54) * mm});
            skLineSegment(sketch, "E1026", {"start": v(23.93, 2.54) * mm, "end": v(24.17, 2.68) * mm});
            skLineSegment(sketch, "E1027", {"start": v(24.17, 2.68) * mm, "end": v(23.96, 2.96) * mm});
            skLineSegment(sketch, "E1028", {"start": v(23.96, 2.96) * mm, "end": v(23.82, 2.73) * mm});
            skLineSegment(sketch, "E1029", {"start": v(23.82, 2.73) * mm, "end": v(23.75, 3.06) * mm});
            skLineSegment(sketch, "E1030", {"start": v(23.75, 3.06) * mm, "end": v(24.01, 3.26) * mm});
            skLineSegment(sketch, "E1031", {"start": v(24.01, 3.26) * mm, "end": v(23.97, 3.8) * mm});
            skLineSegment(sketch, "E1032", {"start": v(23.97, 3.8) * mm, "end": v(23.73, 3.79) * mm});
            skLineSegment(sketch, "E1033", {"start": v(23.73, 3.79) * mm, "end": v(23.78, 4.18) * mm});
            skLineSegment(sketch, "E1034", {"start": v(23.78, 4.18) * mm, "end": v(24.08, 4.5) * mm});
            skLineSegment(sketch, "E1035", {"start": v(24.08, 4.5) * mm, "end": v(23.96, 4.67) * mm});
            skLineSegment(sketch, "E1036", {"start": v(23.96, 4.67) * mm, "end": v(23.57, 4.33) * mm});
            skLineSegment(sketch, "E1037", {"start": v(23.57, 4.33) * mm, "end": v(23.31, 3.83) * mm});
            skLineSegment(sketch, "E1038", {"start": v(23.31, 3.83) * mm, "end": v(23.54, 3.48) * mm});
            skLineSegment(sketch, "E1039", {"start": v(23.54, 3.48) * mm, "end": v(23.36, 2.92) * mm});
            skLineSegment(sketch, "E1040", {"start": v(23.36, 2.92) * mm, "end": v(23.6, 2.26) * mm});
            skLineSegment(sketch, "E1041", {"start": v(23.6, 2.26) * mm, "end": v(23.83, 2.07) * mm});
            skLineSegment(sketch, "E1042", {"start": v(23.83, 2.07) * mm, "end": v(23.8, 1.89) * mm});
            skLineSegment(sketch, "E1043", {"start": v(23.8, 1.89) * mm, "end": v(23.94, 1.44) * mm});
            skLineSegment(sketch, "E1044", {"start": v(23.94, 1.44) * mm, "end": v(23.34, 1.5) * mm});
            skLineSegment(sketch, "E1045", {"start": v(23.34, 1.5) * mm, "end": v(22.88, 1.52) * mm});
            skLineSegment(sketch, "E1046", {"start": v(22.88, 1.52) * mm, "end": v(22.28, 1.63) * mm});
            skLineSegment(sketch, "E1047", {"start": v(22.28, 1.63) * mm, "end": v(22.2, 2.07) * mm});
            skLineSegment(sketch, "E1048", {"start": v(22.2, 2.07) * mm, "end": v(22.4, 2.33) * mm});
            skLineSegment(sketch, "E1049", {"start": v(22.4, 2.33) * mm, "end": v(22.43, 2.68) * mm});
            skLineSegment(sketch, "E1050", {"start": v(22.43, 2.68) * mm, "end": v(22.1, 3.1) * mm});
            skLineSegment(sketch, "E1051", {"start": v(22.1, 3.1) * mm, "end": v(21.43, 3.27) * mm});
            skLineSegment(sketch, "E1052", {"start": v(21.43, 3.27) * mm, "end": v(21.46, 3.6) * mm});
            skLineSegment(sketch, "E1053", {"start": v(21.46, 3.6) * mm, "end": v(20.94, 3.85) * mm});
            skLineSegment(sketch, "E1054", {"start": v(22.88, 1.52) * mm, "end": v(23.06, 1.33) * mm});
            skLineSegment(sketch, "E1055", {"start": v(23.06, 1.33) * mm, "end": v(23.7, 1.28) * mm});
            skLineSegment(sketch, "E1056", {"start": v(23.7, 1.28) * mm, "end": v(23.9, 1.01) * mm});
            skLineSegment(sketch, "E1057", {"start": v(23.9, 1.01) * mm, "end": v(24.26, 1.03) * mm});
            skLineSegment(sketch, "E1058", {"start": v(24.26, 1.03) * mm, "end": v(24.4, 0.85) * mm});
            skLineSegment(sketch, "E1059", {"start": v(24.4, 0.85) * mm, "end": v(24.37, 0.33) * mm});
            skLineSegment(sketch, "E1060", {"start": v(24.37, 0.33) * mm, "end": v(24.47, 0.27) * mm});
            skLineSegment(sketch, "E1061", {"start": v(24.47, 0.27) * mm, "end": v(24.47, -0.01) * mm});
            skLineSegment(sketch, "E1062", {"start": v(24.47, -0.01) * mm, "end": v(24.67, -0.27) * mm});
            skLineSegment(sketch, "E1063", {"start": v(24.67, -0.27) * mm, "end": v(24.65, -0.45) * mm});
            skLineSegment(sketch, "E1064", {"start": v(24.65, -0.45) * mm, "end": v(24.24, -0.32) * mm});
            skLineSegment(sketch, "E1065", {"start": v(24.24, -0.32) * mm, "end": v(24.24, -0.42) * mm});
            skLineSegment(sketch, "E1066", {"start": v(24.24, -0.42) * mm, "end": v(24.46, -0.58) * mm});
            skLineSegment(sketch, "E1067", {"start": v(24.46, -0.58) * mm, "end": v(24.46, -0.7) * mm});
            skLineSegment(sketch, "E1068", {"start": v(24.46, -0.7) * mm, "end": v(24.77, -0.97) * mm});
            skLineSegment(sketch, "E1069", {"start": v(24.77, -0.97) * mm, "end": v(24.83, -1.33) * mm});
            skLineSegment(sketch, "E1070", {"start": v(24.83, -1.33) * mm, "end": v(24.54, -1.44) * mm});
            skLineSegment(sketch, "E1071", {"start": v(24.54, -1.44) * mm, "end": v(24.54, -1.55) * mm});
            skLineSegment(sketch, "E1072", {"start": v(24.54, -1.55) * mm, "end": v(25.36, -1.37) * mm});
            skLineSegment(sketch, "E1073", {"start": v(25.36, -1.37) * mm, "end": v(25.7, -2.2) * mm});
            skLineSegment(sketch, "E1074", {"start": v(25.7, -2.2) * mm, "end": v(26.76, -3.9) * mm});
            skLineSegment(sketch, "E1075", {"start": v(26.76, -3.9) * mm, "end": v(26.36, -3.9) * mm});
            skLineSegment(sketch, "E1076", {"start": v(12.39, -8.45) * mm, "end": v(14.07, -7.68) * mm});
            skLineSegment(sketch, "E1077", {"start": v(14.07, -7.68) * mm, "end": v(16.67, -7.52) * mm});
            skLineSegment(sketch, "E1078", {"start": v(16.67, -7.52) * mm, "end": v(16.96, -7.84) * mm});
            skLineSegment(sketch, "E1079", {"start": v(16.96, -7.84) * mm, "end": v(17.04, -8.1) * mm});
            skLineSegment(sketch, "E1080", {"start": v(17.04, -8.1) * mm, "end": v(19.18, -7.92) * mm});
            skLineSegment(sketch, "E1081", {"start": v(19.18, -7.92) * mm, "end": v(21.75, -9.69) * mm});
            skLineSegment(sketch, "E1082", {"start": v(21.75, -9.69) * mm, "end": v(22.32, -9.53) * mm});
            skLineSegment(sketch, "E1083", {"start": v(22.32, -9.53) * mm, "end": v(23.04, -9.47) * mm});
            skLineSegment(sketch, "E1084", {"start": v(23.04, -9.47) * mm, "end": v(23.23, -8.43) * mm});
            skLineSegment(sketch, "E1085", {"start": v(23.23, -8.43) * mm, "end": v(24.4, -7.3) * mm});
            skLineSegment(sketch, "E1086", {"start": v(24.4, -7.3) * mm, "end": v(25.23, -6.96) * mm});
            skLineSegment(sketch, "E1087", {"start": v(25.23, -6.96) * mm, "end": v(25.53, -7.04) * mm});
            skLineSegment(sketch, "E1088", {"start": v(25.53, -7.04) * mm, "end": v(26.04, -6.2) * mm});
            skLineSegment(sketch, "E1089", {"start": v(26.04, -6.2) * mm, "end": v(25.69, -6.42) * mm});
            skLineSegment(sketch, "E1090", {"start": v(25.69, -6.42) * mm, "end": v(25.55, -6.23) * mm});
            skLineSegment(sketch, "E1091", {"start": v(25.55, -6.23) * mm, "end": v(25.1, -6.26) * mm});
            skLineSegment(sketch, "E1092", {"start": v(25.1, -6.26) * mm, "end": v(25.37, -5.54) * mm});
            skLineSegment(sketch, "E1093", {"start": v(25.37, -5.54) * mm, "end": v(25.07, -5.43) * mm});
            skLineSegment(sketch, "E1094", {"start": v(25.07, -5.43) * mm, "end": v(24.94, -5.14) * mm});
            skLineSegment(sketch, "E1095", {"start": v(24.94, -5.14) * mm, "end": v(25.5, -5.4) * mm});
            skLineSegment(sketch, "E1096", {"start": v(25.5, -5.4) * mm, "end": v(26.04, -5.24) * mm});
            skLineSegment(sketch, "E1097", {"start": v(26.04, -5.24) * mm, "end": v(26.25, -4.58) * mm});
            skLineSegment(sketch, "E1098", {"start": v(26.25, -4.58) * mm, "end": v(26.52, -4.44) * mm});
            skLineSegment(sketch, "E1099", {"start": v(26.52, -4.44) * mm, "end": v(26.36, -3.9) * mm});
            skLineSegment(sketch, "E1100", {"start": v(12.39, -8.45) * mm, "end": v(12.5, -8.7) * mm});
            skLineSegment(sketch, "E1101", {"start": v(12.5, -8.7) * mm, "end": v(12.18, -8.88) * mm});
            skLineSegment(sketch, "E1102", {"start": v(12.18, -8.88) * mm, "end": v(12.09, -9.27) * mm});
            skLineSegment(sketch, "E1103", {"start": v(12.09, -9.27) * mm, "end": v(12.77, -9.68) * mm});
            skLineSegment(sketch, "E1104", {"start": v(12.77, -9.68) * mm, "end": v(13.07, -9.62) * mm});
            skLineSegment(sketch, "E1105", {"start": v(13.07, -9.62) * mm, "end": v(13.84, -10.83) * mm});
            skLineSegment(sketch, "E1106", {"start": v(13.84, -10.83) * mm, "end": v(14.6, -11.27) * mm});
            skLineSegment(sketch, "E1107", {"start": v(14.6, -11.27) * mm, "end": v(14.75, -11.56) * mm});
            skLineSegment(sketch, "E1108", {"start": v(14.75, -11.56) * mm, "end": v(15.34, -11.89) * mm});
            skLineSegment(sketch, "E1109", {"start": v(15.34, -11.89) * mm, "end": v(15.8, -12.47) * mm});
            skLineSegment(sketch, "E1110", {"start": v(15.8, -12.47) * mm, "end": v(16.26, -12.7) * mm});
            skLineSegment(sketch, "E1111", {"start": v(16.26, -12.7) * mm, "end": v(16.73, -13.9) * mm});
            skLineSegment(sketch, "E1112", {"start": v(16.73, -13.9) * mm, "end": v(16.96, -13.9) * mm});
            skLineSegment(sketch, "E1113", {"start": v(16.96, -13.9) * mm, "end": v(17.32, -14.34) * mm});
            skLineSegment(sketch, "E1114", {"start": v(17.32, -14.34) * mm, "end": v(17.43, -14.8) * mm});
            skLineSegment(sketch, "E1115", {"start": v(17.43, -14.8) * mm, "end": v(18.03, -15.06) * mm});
            skLineSegment(sketch, "E1116", {"start": v(18.03, -15.06) * mm, "end": v(17.97, -14.83) * mm});
            skLineSegment(sketch, "E1117", {"start": v(17.97, -14.83) * mm, "end": v(18.75, -14.15) * mm});
            skLineSegment(sketch, "E1118", {"start": v(18.75, -14.15) * mm, "end": v(18.58, -13.79) * mm});
            skLineSegment(sketch, "E1119", {"start": v(18.58, -13.79) * mm, "end": v(19, -13.77) * mm});
            skLineSegment(sketch, "E1120", {"start": v(19, -13.77) * mm, "end": v(20.32, -12.25) * mm});
            skLineSegment(sketch, "E1121", {"start": v(20.32, -12.25) * mm, "end": v(20.52, -12.16) * mm});
            skLineSegment(sketch, "E1122", {"start": v(20.52, -12.16) * mm, "end": v(20.94, -11.68) * mm});
            skLineSegment(sketch, "E1123", {"start": v(20.94, -11.68) * mm, "end": v(20.97, -11.01) * mm});
            skLineSegment(sketch, "E1124", {"start": v(20.97, -11.01) * mm, "end": v(21.47, -10.09) * mm});
            skLineSegment(sketch, "E1125", {"start": v(21.47, -10.09) * mm, "end": v(21.75, -9.69) * mm});
            skLineSegment(sketch, "E1126", {"start": v(18.03, -15.06) * mm, "end": v(17.69, -15.85) * mm});
            skLineSegment(sketch, "E1127", {"start": v(17.69, -15.85) * mm, "end": v(17.7, -16.03) * mm});
            skLineSegment(sketch, "E1128", {"start": v(17.7, -16.03) * mm, "end": v(17.56, -16.53) * mm});
            skLineSegment(sketch, "E1129", {"start": v(17.56, -16.53) * mm, "end": v(17.23, -17.55) * mm});
            skLineSegment(sketch, "E1130", {"start": v(17.23, -17.55) * mm, "end": v(17.3, -18.37) * mm});
            skLineSegment(sketch, "E1131", {"start": v(17.3, -18.37) * mm, "end": v(16.2, -18.28) * mm});
            skLineSegment(sketch, "E1132", {"start": v(16.2, -18.28) * mm, "end": v(16.04, -18.47) * mm});
            skLineSegment(sketch, "E1133", {"start": v(16.04, -18.47) * mm, "end": v(16.12, -18.87) * mm});
            skLineSegment(sketch, "E1134", {"start": v(16.12, -18.87) * mm, "end": v(16.17, -19.37) * mm});
            skLineSegment(sketch, "E1135", {"start": v(16.17, -19.37) * mm, "end": v(15.85, -19.35) * mm});
            skLineSegment(sketch, "E1136", {"start": v(15.85, -19.35) * mm, "end": v(15.81, -18.97) * mm});
            skLineSegment(sketch, "E1137", {"start": v(15.04, -22.5) * mm, "end": v(15.6, -23.3) * mm});
            skLineSegment(sketch, "E1138", {"start": v(15.6, -23.3) * mm, "end": v(15.58, -24.48) * mm});
            skLineSegment(sketch, "E1139", {"start": v(15.58, -24.48) * mm, "end": v(15.35, -24.8) * mm});
            skLineSegment(sketch, "E1140", {"start": v(15.35, -24.8) * mm, "end": v(15.78, -26.06) * mm});
            skLineSegment(sketch, "E1141", {"start": v(15.78, -26.06) * mm, "end": v(15.98, -25.72) * mm});
            skLineSegment(sketch, "E1142", {"start": v(15.98, -25.72) * mm, "end": v(15.64, -25.44) * mm});
            skLineSegment(sketch, "E1143", {"start": v(15.64, -25.44) * mm, "end": v(16.43, -25.47) * mm});
            skLineSegment(sketch, "E1144", {"start": v(16.43, -25.47) * mm, "end": v(15.8, -26.43) * mm});
            skLineSegment(sketch, "E1145", {"start": v(15.8, -26.43) * mm, "end": v(16.46, -27.25) * mm});
            skLineSegment(sketch, "E1146", {"start": v(16.46, -27.25) * mm, "end": v(16.9, -27.87) * mm});
            skLineSegment(sketch, "E1147", {"start": v(16.9, -27.87) * mm, "end": v(17.27, -28.8) * mm});
            skLineSegment(sketch, "E1148", {"start": v(17.27, -28.8) * mm, "end": v(17.5, -28.94) * mm});
            skLineSegment(sketch, "E1149", {"start": v(17.5, -28.94) * mm, "end": v(17.73, -28.74) * mm});
            skLineSegment(sketch, "E1150", {"start": v(17.73, -28.74) * mm, "end": v(18.12, -29.05) * mm});
            skLineSegment(sketch, "E1151", {"start": v(18.12, -29.05) * mm, "end": v(18.2, -29.42) * mm});
            skLineSegment(sketch, "E1152", {"start": v(18.2, -29.42) * mm, "end": v(18.54, -29.96) * mm});
            skLineSegment(sketch, "E1153", {"start": v(18.54, -29.96) * mm, "end": v(18.74, -29.93) * mm});
            skLineSegment(sketch, "E1154", {"start": v(18.74, -29.93) * mm, "end": v(19.1, -29.99) * mm});
            skLineSegment(sketch, "E1155", {"start": v(19.1, -29.99) * mm, "end": v(19.53, -30.32) * mm});
            skLineSegment(sketch, "E1156", {"start": v(19.53, -30.32) * mm, "end": v(19.87, -30.78) * mm});
            skLineSegment(sketch, "E1157", {"start": v(19.87, -30.78) * mm, "end": v(20.04, -31.6) * mm});
            skLineSegment(sketch, "E1158", {"start": v(20.04, -31.6) * mm, "end": v(20.24, -31.76) * mm});
            skLineSegment(sketch, "E1159", {"start": v(20.24, -31.76) * mm, "end": v(20.55, -31.65) * mm});
            skLineSegment(sketch, "E1160", {"start": v(20.55, -31.65) * mm, "end": v(20.72, -31.31) * mm});
            skLineSegment(sketch, "E1161", {"start": v(20.72, -31.31) * mm, "end": v(20.94, -31.37) * mm});
            skLineSegment(sketch, "E1162", {"start": v(20.94, -31.37) * mm, "end": v(21.3, -31.31) * mm});
            skLineSegment(sketch, "E1163", {"start": v(21.3, -31.31) * mm, "end": v(21.79, -30.97) * mm});
            skLineSegment(sketch, "E1164", {"start": v(21.79, -30.97) * mm, "end": v(21.7, -30.55) * mm});
            skLineSegment(sketch, "E1165", {"start": v(21.7, -30.55) * mm, "end": v(21.7, -30.3) * mm});
            skLineSegment(sketch, "E1166", {"start": v(21.7, -30.3) * mm, "end": v(21.62, -29.93) * mm});
            skLineSegment(sketch, "E1167", {"start": v(21.62, -29.93) * mm, "end": v(22.04, -29.62) * mm});
            skLineSegment(sketch, "E1168", {"start": v(22.04, -29.62) * mm, "end": v(22.04, -29.17) * mm});
            skLineSegment(sketch, "E1169", {"start": v(22.04, -29.17) * mm, "end": v(21.9, -27.22) * mm});
            skLineSegment(sketch, "E1170", {"start": v(21.9, -27.22) * mm, "end": v(20.69, -24.96) * mm});
            skLineSegment(sketch, "E1171", {"start": v(20.69, -24.96) * mm, "end": v(20.15, -24.6) * mm});
            skLineSegment(sketch, "E1172", {"start": v(20.15, -24.6) * mm, "end": v(19.93, -23.8) * mm});
            skLineSegment(sketch, "E1173", {"start": v(19.93, -23.8) * mm, "end": v(20.1, -23.52) * mm});
            skLineSegment(sketch, "E1174", {"start": v(20.1, -23.52) * mm, "end": v(19.9, -23.04) * mm});
            skLineSegment(sketch, "E1175", {"start": v(19.9, -23.04) * mm, "end": v(19.16, -22.34) * mm});
            skLineSegment(sketch, "E1176", {"start": v(19.16, -22.34) * mm, "end": v(18.26, -20.95) * mm});
            skLineSegment(sketch, "E1177", {"start": v(18.26, -20.95) * mm, "end": v(17.56, -19.32) * mm});
            skLineSegment(sketch, "E1178", {"start": v(17.56, -19.32) * mm, "end": v(17.3, -18.37) * mm});
            skLineSegment(sketch, "E1179", {"start": v(-48.6, -19.32) * mm, "end": v(-49.57, -18.83) * mm});
            skLineSegment(sketch, "E1180", {"start": v(-49.57, -18.83) * mm, "end": v(-49.92, -19) * mm});
            skLineSegment(sketch, "E1181", {"start": v(-49.92, -19) * mm, "end": v(-50.62, -18.7) * mm});
            skLineSegment(sketch, "E1182", {"start": v(-50.62, -18.7) * mm, "end": v(-50.7, -19) * mm});
            skLineSegment(sketch, "E1183", {"start": v(-50.7, -19) * mm, "end": v(-51.4, -18.34) * mm});
            skLineSegment(sketch, "E1184", {"start": v(-51.4, -18.34) * mm, "end": v(-52.24, -18.3) * mm});
            skLineSegment(sketch, "E1185", {"start": v(-52.24, -18.3) * mm, "end": v(-52.49, -18.17) * mm});
            skLineSegment(sketch, "E1186", {"start": v(-52.49, -18.17) * mm, "end": v(-52.5, -17.69) * mm});
            skLineSegment(sketch, "E1187", {"start": v(-52.5, -17.69) * mm, "end": v(-52.91, -17.64) * mm});
            skLineSegment(sketch, "E1188", {"start": v(-52.91, -17.64) * mm, "end": v(-53.05, -17.9) * mm});
            skLineSegment(sketch, "E1189", {"start": v(-53.05, -17.9) * mm, "end": v(-53.11, -17.6) * mm});
            skLineSegment(sketch, "E1190", {"start": v(-53.11, -17.6) * mm, "end": v(-53.83, -17.1) * mm});
            skLineSegment(sketch, "E1191", {"start": v(-53.83, -17.1) * mm, "end": v(-54.15, -17.43) * mm});
            skLineSegment(sketch, "E1192", {"start": v(-54.15, -17.43) * mm, "end": v(-54.62, -17.47) * mm});
            skLineSegment(sketch, "E1193", {"start": v(-54.62, -17.47) * mm, "end": v(-54.82, -17.37) * mm});
            skLineSegment(sketch, "E1194", {"start": v(-54.82, -17.37) * mm, "end": v(-55.6, -17.72) * mm});
            skLineSegment(sketch, "E1195", {"start": v(-55.6, -17.72) * mm, "end": v(-55.85, -17.52) * mm});
            skLineSegment(sketch, "E1196", {"start": v(-55.85, -17.52) * mm, "end": v(-56.16, -17.85) * mm});
            skLineSegment(sketch, "E1197", {"start": v(-56.16, -17.85) * mm, "end": v(-56.27, -18.17) * mm});
            skLineSegment(sketch, "E1198", {"start": v(-56.27, -18.17) * mm, "end": v(-56.7, -18.55) * mm});
            skLineSegment(sketch, "E1199", {"start": v(-56.7, -18.55) * mm, "end": v(-57.16, -18.55) * mm});
            skLineSegment(sketch, "E1200", {"start": v(-57.16, -18.55) * mm, "end": v(-57.24, -18.54) * mm});
            skLineSegment(sketch, "E1201", {"start": v(-57.24, -18.54) * mm, "end": v(-57.7, -18.45) * mm});
            skLineSegment(sketch, "E1202", {"start": v(-57.7, -18.45) * mm, "end": v(-58.03, -18.7) * mm});
            skLineSegment(sketch, "E1203", {"start": v(-58.03, -18.7) * mm, "end": v(-57.44, -19.73) * mm});
            skLineSegment(sketch, "E1204", {"start": v(-57.44, -19.73) * mm, "end": v(-57.44, -20.43) * mm});
            skLineSegment(sketch, "E1205", {"start": v(-57.44, -20.43) * mm, "end": v(-56.94, -20.66) * mm});
            skLineSegment(sketch, "E1206", {"start": v(-56.94, -20.66) * mm, "end": v(-57.12, -20.76) * mm});
            skLineSegment(sketch, "E1207", {"start": v(-57.12, -20.76) * mm, "end": v(-56.77, -21.6) * mm});
            skLineSegment(sketch, "E1208", {"start": v(-56.77, -21.6) * mm, "end": v(-56.95, -21.76) * mm});
            skLineSegment(sketch, "E1209", {"start": v(-56.95, -21.76) * mm, "end": v(-57.79, -21.39) * mm});
            skLineSegment(sketch, "E1210", {"start": v(-57.79, -21.39) * mm, "end": v(-57.6, -20.95) * mm});
            skLineSegment(sketch, "E1211", {"start": v(-57.6, -20.95) * mm, "end": v(-57.8, -20.78) * mm});
            skLineSegment(sketch, "E1212", {"start": v(-57.8, -20.78) * mm, "end": v(-58.41, -20.84) * mm});
            skLineSegment(sketch, "E1213", {"start": v(-58.41, -20.84) * mm, "end": v(-58.41, -21.04) * mm});
            skLineSegment(sketch, "E1214", {"start": v(-58.41, -21.04) * mm, "end": v(-58.54, -21.05) * mm});
            skLineSegment(sketch, "E1215", {"start": v(-58.54, -21.05) * mm, "end": v(-58.63, -20.96) * mm});
            skLineSegment(sketch, "E1216", {"start": v(-58.63, -20.96) * mm, "end": v(-59.54, -20.98) * mm});
            skLineSegment(sketch, "E1217", {"start": v(-59.54, -20.98) * mm, "end": v(-59.63, -21.16) * mm});
            skLineSegment(sketch, "E1218", {"start": v(-59.63, -21.16) * mm, "end": v(-59.27, -21.65) * mm});
            skLineSegment(sketch, "E1219", {"start": v(-59.27, -21.65) * mm, "end": v(-59.36, -22.33) * mm});
            skLineSegment(sketch, "E1220", {"start": v(-59.36, -22.33) * mm, "end": v(-58.93, -22.82) * mm});
            skLineSegment(sketch, "E1221", {"start": v(-58.93, -22.82) * mm, "end": v(-58.44, -22.8) * mm});
            skLineSegment(sketch, "E1222", {"start": v(-58.44, -22.8) * mm, "end": v(-57.87, -23.05) * mm});
            skLineSegment(sketch, "E1223", {"start": v(-57.87, -23.05) * mm, "end": v(-57.2, -22.9) * mm});
            skLineSegment(sketch, "E1224", {"start": v(-57.2, -22.9) * mm, "end": v(-57.07, -23.1) * mm});
            skLineSegment(sketch, "E1225", {"start": v(-57.07, -23.1) * mm, "end": v(-57.33, -24.06) * mm});
            skLineSegment(sketch, "E1226", {"start": v(-48.6, -19.32) * mm, "end": v(-48.6, -28.8) * mm});
            skLineSegment(sketch, "E1227", {"start": v(-48.6, -28.8) * mm, "end": v(-48.45, -29.07) * mm});
            skLineSegment(sketch, "E1228", {"start": v(-48.45, -29.07) * mm, "end": v(-48.19, -29) * mm});
            skLineSegment(sketch, "E1229", {"start": v(-48.19, -29) * mm, "end": v(-48.05, -29) * mm});
            skLineSegment(sketch, "E1230", {"start": v(-48.05, -29) * mm, "end": v(-47.85, -28.87) * mm});
            skLineSegment(sketch, "E1231", {"start": v(-47.85, -28.87) * mm, "end": v(-47.69, -28.92) * mm});
            skLineSegment(sketch, "E1232", {"start": v(-47.69, -28.92) * mm, "end": v(-47.67, -29.23) * mm});
            skLineSegment(sketch, "E1233", {"start": v(-47.67, -29.23) * mm, "end": v(-46.96, -29.88) * mm});
            skLineSegment(sketch, "E1234", {"start": v(-46.96, -29.88) * mm, "end": v(-46.8, -30.27) * mm});
            skLineSegment(sketch, "E1235", {"start": v(-46.8, -30.27) * mm, "end": v(-46.26, -30) * mm});
            skLineSegment(sketch, "E1236", {"start": v(-46.26, -30) * mm, "end": v(-46.24, -29.6) * mm});
            skLineSegment(sketch, "E1237", {"start": v(-46.24, -29.6) * mm, "end": v(-45.97, -29.45) * mm});
            skLineSegment(sketch, "E1238", {"start": v(-45.62, -29.55) * mm, "end": v(-45.47, -29.94) * mm});
            skLineSegment(sketch, "E1239", {"start": v(-45.47, -29.94) * mm, "end": v(-45.2, -29.94) * mm});
            skLineSegment(sketch, "E1240", {"start": v(-45.2, -29.94) * mm, "end": v(-45.17, -30.38) * mm});
            skLineSegment(sketch, "E1241", {"start": v(-45.97, -29.45) * mm, "end": v(-45.62, -29.55) * mm});
            skLineSegment(sketch, "E1242", {"start": v(-45.17, -30.38) * mm, "end": v(-44.76, -30.38) * mm});
            skLineSegment(sketch, "E1243", {"start": v(-44.76, -30.38) * mm, "end": v(-44.32, -31.23) * mm});
            skLineSegment(sketch, "E1244", {"start": v(-44.32, -31.23) * mm, "end": v(-43.8, -31.8) * mm});
            skLineSegment(sketch, "E1245", {"start": v(-43.8, -31.8) * mm, "end": v(-43.66, -32.28) * mm});
            skLineSegment(sketch, "E1246", {"start": v(-43.66, -32.28) * mm, "end": v(-42.49, -32.65) * mm});
            skLineSegment(sketch, "E1247", {"start": v(-42.49, -32.65) * mm, "end": v(-42.36, -33.4) * mm});
            skLineSegment(sketch, "E1248", {"start": v(-42.36, -33.4) * mm, "end": v(-42.63, -34.08) * mm});
            skLineSegment(sketch, "E1249", {"start": v(-42.63, -34.08) * mm, "end": v(-42.77, -34) * mm});
            skLineSegment(sketch, "E1250", {"start": v(-42.77, -34) * mm, "end": v(-42.88, -33.71) * mm});
            skLineSegment(sketch, "E1251", {"start": v(-42.88, -33.71) * mm, "end": v(-43.38, -33.4) * mm});
            skLineSegment(sketch, "E1252", {"start": v(-43.38, -33.4) * mm, "end": v(-43.52, -33.46) * mm});
            skLineSegment(sketch, "E1253", {"start": v(-43.52, -33.46) * mm, "end": v(-43.37, -33.69) * mm});
            skLineSegment(sketch, "E1254", {"start": v(-43.37, -33.69) * mm, "end": v(-43.37, -34.26) * mm});
            skLineSegment(sketch, "E1255", {"start": v(-43.37, -34.26) * mm, "end": v(-43.66, -34.02) * mm});
            skLineSegment(sketch, "E1256", {"start": v(-43.66, -34.02) * mm, "end": v(-43.95, -33.8) * mm});
            skLineSegment(sketch, "E1257", {"start": v(-43.95, -33.8) * mm, "end": v(-43.72, -34.23) * mm});
            skLineSegment(sketch, "E1258", {"start": v(-43.72, -34.23) * mm, "end": v(-43.82, -34.36) * mm});
            skLineSegment(sketch, "E1259", {"start": v(-43.82, -34.36) * mm, "end": v(-44.26, -33.6) * mm});
            skLineSegment(sketch, "E1260", {"start": v(-44.26, -33.6) * mm, "end": v(-44.37, -33.72) * mm});
            skLineSegment(sketch, "E1261", {"start": v(-44.29, -33.36) * mm, "end": v(-44.44, -33.23) * mm});
            skLineSegment(sketch, "E1262", {"start": v(-44.44, -33.23) * mm, "end": v(-44.44, -32.66) * mm});
            skLineSegment(sketch, "E1263", {"start": v(-44.44, -32.66) * mm, "end": v(-44.64, -33.03) * mm});
            skLineSegment(sketch, "E1264", {"start": v(-44.64, -33.03) * mm, "end": v(-44.82, -33.16) * mm});
            skLineSegment(sketch, "E1265", {"start": v(-44.82, -33.16) * mm, "end": v(-44.93, -32.28) * mm});
            skLineSegment(sketch, "E1266", {"start": v(-44.93, -32.28) * mm, "end": v(-45.06, -32.2) * mm});
            skLineSegment(sketch, "E1267", {"start": v(-45.06, -32.2) * mm, "end": v(-45.06, -32.88) * mm});
            skLineSegment(sketch, "E1268", {"start": v(-45.06, -32.88) * mm, "end": v(-45.54, -32.17) * mm});
            skLineSegment(sketch, "E1269", {"start": v(-45.54, -32.17) * mm, "end": v(-45.86, -32.11) * mm});
            skLineSegment(sketch, "E1270", {"start": v(-45.86, -32.11) * mm, "end": v(-45.87, -31.71) * mm});
            skLineSegment(sketch, "E1271", {"start": v(-45.87, -31.71) * mm, "end": v(-46.04, -31.38) * mm});
            skLineSegment(sketch, "E1272", {"start": v(-46.04, -31.38) * mm, "end": v(-46.29, -31.2) * mm});
            skLineSegment(sketch, "E1273", {"start": v(-46.29, -31.2) * mm, "end": v(-46.29, -31) * mm});
            skLineSegment(sketch, "E1274", {"start": v(-46.29, -31) * mm, "end": v(-45.97, -30.84) * mm});
            skLineSegment(sketch, "E1275", {"start": v(-45.97, -30.84) * mm, "end": v(-46.08, -30.76) * mm});
            skLineSegment(sketch, "E1276", {"start": v(-46.08, -30.76) * mm, "end": v(-46.31, -30.9) * mm});
            skLineSegment(sketch, "E1277", {"start": v(-46.31, -30.9) * mm, "end": v(-46.8, -30.54) * mm});
            skLineSegment(sketch, "E1278", {"start": v(-46.8, -30.54) * mm, "end": v(-46.92, -30.37) * mm});
            skLineSegment(sketch, "E1279", {"start": v(-46.92, -30.37) * mm, "end": v(-48, -29.75) * mm});
            skLineSegment(sketch, "E1280", {"start": v(-48, -29.75) * mm, "end": v(-47.82, -29.43) * mm});
            skLineSegment(sketch, "E1281", {"start": v(-47.82, -29.43) * mm, "end": v(-47.8, -29.1) * mm});
            skLineSegment(sketch, "E1282", {"start": v(-47.8, -29.1) * mm, "end": v(-48.28, -29.45) * mm});
            skLineSegment(sketch, "E1283", {"start": v(-48.28, -29.45) * mm, "end": v(-49.36, -29.07) * mm});
            skLineSegment(sketch, "E1284", {"start": v(-49.36, -29.07) * mm, "end": v(-49.98, -29.05) * mm});
            skLineSegment(sketch, "E1285", {"start": v(-49.98, -29.05) * mm, "end": v(-50.06, -29.13) * mm});
            skLineSegment(sketch, "E1286", {"start": v(-50.06, -29.13) * mm, "end": v(-50.72, -28.7) * mm});
            skLineSegment(sketch, "E1287", {"start": v(-50.72, -28.7) * mm, "end": v(-50.93, -28.68) * mm});
            skLineSegment(sketch, "E1288", {"start": v(-50.93, -28.68) * mm, "end": v(-51.28, -28.04) * mm});
            skLineSegment(sketch, "E1289", {"start": v(-51.28, -28.04) * mm, "end": v(-51.6, -28.03) * mm});
            skLineSegment(sketch, "E1290", {"start": v(-51.6, -28.03) * mm, "end": v(-52.1, -28.22) * mm});
            skLineSegment(sketch, "E1291", {"start": v(-52.1, -28.22) * mm, "end": v(-52.09, -28.63) * mm});
            skLineSegment(sketch, "E1292", {"start": v(-52.09, -28.63) * mm, "end": v(-51.92, -28.66) * mm});
            skLineSegment(sketch, "E1293", {"start": v(-51.92, -28.66) * mm, "end": v(-51.97, -28.9) * mm});
            skLineSegment(sketch, "E1294", {"start": v(-51.97, -28.9) * mm, "end": v(-52.14, -29.07) * mm});
            skLineSegment(sketch, "E1295", {"start": v(-52.14, -29.07) * mm, "end": v(-52.31, -28.93) * mm});
            skLineSegment(sketch, "E1296", {"start": v(-52.31, -28.93) * mm, "end": v(-52.46, -29.06) * mm});
            skLineSegment(sketch, "E1297", {"start": v(-52.46, -29.06) * mm, "end": v(-52.72, -28.85) * mm});
            skLineSegment(sketch, "E1298", {"start": v(-52.72, -28.85) * mm, "end": v(-53.1, -29.1) * mm});
            skLineSegment(sketch, "E1299", {"start": v(-53.1, -29.1) * mm, "end": v(-53.62, -29.55) * mm});
            skLineSegment(sketch, "E1300", {"start": v(-53.62, -29.55) * mm, "end": v(-54.23, -29.55) * mm});
            skLineSegment(sketch, "E1301", {"start": v(-54.23, -29.55) * mm, "end": v(-54.26, -29.33) * mm});
            skLineSegment(sketch, "E1302", {"start": v(-54.26, -29.33) * mm, "end": v(-53.86, -29.27) * mm});
            skLineSegment(sketch, "E1303", {"start": v(-53.86, -29.27) * mm, "end": v(-53.83, -29.1) * mm});
            skLineSegment(sketch, "E1304", {"start": v(-53.83, -29.1) * mm, "end": v(-54.14, -29.02) * mm});
            skLineSegment(sketch, "E1305", {"start": v(-54.14, -29.02) * mm, "end": v(-53.59, -27.98) * mm});
            skLineSegment(sketch, "E1306", {"start": v(-53.59, -27.98) * mm, "end": v(-53.25, -27.8) * mm});
            skLineSegment(sketch, "E1307", {"start": v(-53.25, -27.8) * mm, "end": v(-53.11, -27.95) * mm});
            skLineSegment(sketch, "E1308", {"start": v(-53.11, -27.95) * mm, "end": v(-52.8, -27.96) * mm});
            skLineSegment(sketch, "E1309", {"start": v(-52.8, -27.96) * mm, "end": v(-52.95, -27.64) * mm});
            skLineSegment(sketch, "E1310", {"start": v(-52.95, -27.64) * mm, "end": v(-53.33, -27.56) * mm});
            skLineSegment(sketch, "E1311", {"start": v(-53.33, -27.56) * mm, "end": v(-53.95, -27.9) * mm});
            skLineSegment(sketch, "E1312", {"start": v(-53.95, -27.9) * mm, "end": v(-54.49, -28.83) * mm});
            skLineSegment(sketch, "E1313", {"start": v(-54.49, -28.83) * mm, "end": v(-55.01, -29.01) * mm});
            skLineSegment(sketch, "E1314", {"start": v(-55.01, -29.01) * mm, "end": v(-55.35, -29.31) * mm});
            skLineSegment(sketch, "E1315", {"start": v(-55.35, -29.31) * mm, "end": v(-55.34, -29.44) * mm});
            skLineSegment(sketch, "E1316", {"start": v(-55.34, -29.44) * mm, "end": v(-55.16, -29.58) * mm});
            skLineSegment(sketch, "E1317", {"start": v(-55.16, -29.58) * mm, "end": v(-55.02, -29.8) * mm});
            skLineSegment(sketch, "E1318", {"start": v(-55.02, -29.8) * mm, "end": v(-55.3, -30.12) * mm});
            skLineSegment(sketch, "E1319", {"start": v(-55.3, -30.12) * mm, "end": v(-57.14, -31.2) * mm});
            skLineSegment(sketch, "E1320", {"start": v(-57.14, -31.2) * mm, "end": v(-58.26, -31.58) * mm});
            skLineSegment(sketch, "E1321", {"start": v(-58.26, -31.58) * mm, "end": v(-58.1, -31.75) * mm});
            skLineSegment(sketch, "E1322", {"start": v(-58.1, -31.75) * mm, "end": v(-58.32, -32.02) * mm});
            skLineSegment(sketch, "E1323", {"start": v(-58.32, -32.02) * mm, "end": v(-58.61, -31.92) * mm});
            skLineSegment(sketch, "E1324", {"start": v(-58.61, -31.92) * mm, "end": v(-58.9, -31.91) * mm});
            skLineSegment(sketch, "E1325", {"start": v(-58.9, -31.91) * mm, "end": v(-59.01, -32.09) * mm});
            skLineSegment(sketch, "E1326", {"start": v(-59.01, -32.09) * mm, "end": v(-59.1, -31.94) * mm});
            skLineSegment(sketch, "E1327", {"start": v(-59.1, -31.94) * mm, "end": v(-59.78, -32.17) * mm});
            skLineSegment(sketch, "E1328", {"start": v(-59.78, -32.17) * mm, "end": v(-60.21, -32) * mm});
            skLineSegment(sketch, "E1329", {"start": v(-60.21, -32) * mm, "end": v(-60.5, -32.23) * mm});
            skLineSegment(sketch, "E1330", {"start": v(-60.5, -32.23) * mm, "end": v(-60.87, -32.22) * mm});
            skLineSegment(sketch, "E1331", {"start": v(-60.87, -32.22) * mm, "end": v(-61.24, -32.46) * mm});
            skLineSegment(sketch, "E1332", {"start": v(-61.24, -32.46) * mm, "end": v(-61.8, -32.34) * mm});
            skLineSegment(sketch, "E1333", {"start": v(-61.8, -32.34) * mm, "end": v(-62.16, -32.48) * mm});
            skLineSegment(sketch, "E1334", {"start": v(-62.16, -32.48) * mm, "end": v(-62.39, -32.36) * mm});
            skLineSegment(sketch, "E1335", {"start": v(-62.39, -32.36) * mm, "end": v(-62.36, -32.1) * mm});
            skLineSegment(sketch, "E1336", {"start": v(-62.36, -32.1) * mm, "end": v(-62.1, -31.98) * mm});
            skLineSegment(sketch, "E1337", {"start": v(-62.1, -31.98) * mm, "end": v(-61.39, -32.07) * mm});
            skLineSegment(sketch, "E1338", {"start": v(-61.39, -32.07) * mm, "end": v(-61.08, -31.97) * mm});
            skLineSegment(sketch, "E1339", {"start": v(-61.08, -31.97) * mm, "end": v(-60.93, -31.9) * mm});
            skLineSegment(sketch, "E1340", {"start": v(-60.93, -31.9) * mm, "end": v(-60.58, -31.6) * mm});
            skLineSegment(sketch, "E1341", {"start": v(-60.58, -31.6) * mm, "end": v(-60.36, -31.56) * mm});
            skLineSegment(sketch, "E1342", {"start": v(-60.36, -31.56) * mm, "end": v(-60.07, -31.46) * mm});
            skLineSegment(sketch, "E1343", {"start": v(-60.07, -31.46) * mm, "end": v(-59.84, -31.5) * mm});
            skLineSegment(sketch, "E1344", {"start": v(-59.84, -31.5) * mm, "end": v(-59.7, -31.65) * mm});
            skLineSegment(sketch, "E1345", {"start": v(-59.7, -31.65) * mm, "end": v(-59.48, -31.64) * mm});
            skLineSegment(sketch, "E1346", {"start": v(-59.48, -31.64) * mm, "end": v(-59.18, -31.27) * mm});
            skLineSegment(sketch, "E1347", {"start": v(-59.18, -31.27) * mm, "end": v(-58.39, -31.1) * mm});
            skLineSegment(sketch, "E1348", {"start": v(-58.39, -31.1) * mm, "end": v(-58.28, -31.15) * mm});
            skLineSegment(sketch, "E1349", {"start": v(-58.28, -31.15) * mm, "end": v(-58.13, -30.75) * mm});
            skLineSegment(sketch, "E1350", {"start": v(-58.13, -30.75) * mm, "end": v(-57.64, -30.57) * mm});
            skLineSegment(sketch, "E1351", {"start": v(-57.64, -30.57) * mm, "end": v(-57.23, -29.7) * mm});
            skLineSegment(sketch, "E1352", {"start": v(-57.23, -29.7) * mm, "end": v(-56.98, -29.52) * mm});
            skLineSegment(sketch, "E1353", {"start": v(-56.98, -29.52) * mm, "end": v(-56.93, -29.18) * mm});
            skLineSegment(sketch, "E1354", {"start": v(-56.93, -29.18) * mm, "end": v(-57.37, -29.4) * mm});
            skLineSegment(sketch, "E1355", {"start": v(-57.37, -29.4) * mm, "end": v(-57.6, -29.19) * mm});
            skLineSegment(sketch, "E1356", {"start": v(-57.6, -29.19) * mm, "end": v(-57.72, -29.16) * mm});
            skLineSegment(sketch, "E1357", {"start": v(-57.72, -29.16) * mm, "end": v(-57.91, -29.23) * mm});
            skLineSegment(sketch, "E1358", {"start": v(-57.91, -29.23) * mm, "end": v(-57.93, -29.53) * mm});
            skLineSegment(sketch, "E1359", {"start": v(-57.93, -29.53) * mm, "end": v(-58.03, -29.53) * mm});
            skLineSegment(sketch, "E1360", {"start": v(-58.03, -29.53) * mm, "end": v(-58.16, -28.87) * mm});
            skLineSegment(sketch, "E1361", {"start": v(-58.16, -28.87) * mm, "end": v(-58.31, -29) * mm});
            skLineSegment(sketch, "E1362", {"start": v(-58.31, -29) * mm, "end": v(-58.42, -29) * mm});
            skLineSegment(sketch, "E1363", {"start": v(-58.42, -29) * mm, "end": v(-58.46, -28.79) * mm});
            skLineSegment(sketch, "E1364", {"start": v(-58.46, -28.79) * mm, "end": v(-58.93, -28.8) * mm});
            skLineSegment(sketch, "E1365", {"start": v(-58.93, -28.8) * mm, "end": v(-59.21, -28.93) * mm});
            skLineSegment(sketch, "E1366", {"start": v(-59.21, -28.93) * mm, "end": v(-59.5, -28.9) * mm});
            skLineSegment(sketch, "E1367", {"start": v(-59.5, -28.9) * mm, "end": v(-59.28, -28.63) * mm});
            skLineSegment(sketch, "E1368", {"start": v(-59.28, -28.63) * mm, "end": v(-59.31, -28.2) * mm});
            skLineSegment(sketch, "E1369", {"start": v(-59.31, -28.2) * mm, "end": v(-58.97, -28.13) * mm});
            skLineSegment(sketch, "E1370", {"start": v(-58.97, -28.13) * mm, "end": v(-59.1, -27.96) * mm});
            skLineSegment(sketch, "E1371", {"start": v(-59.1, -27.96) * mm, "end": v(-59.04, -27.45) * mm});
            skLineSegment(sketch, "E1372", {"start": v(-59.04, -27.45) * mm, "end": v(-59.24, -27.28) * mm});
            skLineSegment(sketch, "E1373", {"start": v(-59.24, -27.28) * mm, "end": v(-59.34, -27.46) * mm});
            skLineSegment(sketch, "E1374", {"start": v(-59.34, -27.46) * mm, "end": v(-59.97, -27.44) * mm});
            skLineSegment(sketch, "E1375", {"start": v(-59.97, -27.44) * mm, "end": v(-60.13, -27.31) * mm});
            skLineSegment(sketch, "E1376", {"start": v(-60.13, -27.31) * mm, "end": v(-60.2, -26.94) * mm});
            skLineSegment(sketch, "E1377", {"start": v(-60.2, -26.94) * mm, "end": v(-60.38, -26.55) * mm});
            skLineSegment(sketch, "E1378", {"start": v(-60.38, -26.55) * mm, "end": v(-60.42, -26.34) * mm});
            skLineSegment(sketch, "E1379", {"start": v(-60.42, -26.34) * mm, "end": v(-60.18, -26.29) * mm});
            skLineSegment(sketch, "E1380", {"start": v(-60.18, -26.29) * mm, "end": v(-60.2, -26.07) * mm});
            skLineSegment(sketch, "E1381", {"start": v(-60.2, -26.07) * mm, "end": v(-60.03, -25.97) * mm});
            skLineSegment(sketch, "E1382", {"start": v(-60.03, -25.97) * mm, "end": v(-60.13, -25.91) * mm});
            skLineSegment(sketch, "E1383", {"start": v(-60.13, -25.91) * mm, "end": v(-60.26, -25.93) * mm});
            skLineSegment(sketch, "E1384", {"start": v(-60.26, -25.93) * mm, "end": v(-60.4, -25.65) * mm});
            skLineSegment(sketch, "E1385", {"start": v(-60.4, -25.65) * mm, "end": v(-60.32, -25.04) * mm});
            skLineSegment(sketch, "E1386", {"start": v(-60.32, -25.04) * mm, "end": v(-59.53, -24.54) * mm});
            skLineSegment(sketch, "E1387", {"start": v(-59.53, -24.54) * mm, "end": v(-59.31, -24.15) * mm});
            skLineSegment(sketch, "E1388", {"start": v(-59.31, -24.15) * mm, "end": v(-59.02, -23.98) * mm});
            skLineSegment(sketch, "E1389", {"start": v(-59.02, -23.98) * mm, "end": v(-58.76, -24.05) * mm});
            skLineSegment(sketch, "E1390", {"start": v(-58.76, -24.05) * mm, "end": v(-58.67, -24.4) * mm});
            skLineSegment(sketch, "E1391", {"start": v(-58.67, -24.4) * mm, "end": v(-58.36, -24.33) * mm});
            skLineSegment(sketch, "E1392", {"start": v(-58.36, -24.33) * mm, "end": v(-58.03, -24.12) * mm});
            skLineSegment(sketch, "E1393", {"start": v(-58.03, -24.12) * mm, "end": v(-57.76, -24.26) * mm});
            skLineSegment(sketch, "E1394", {"start": v(-57.76, -24.26) * mm, "end": v(-57.6, -24.26) * mm});
            skLineSegment(sketch, "E1395", {"start": v(-57.6, -24.26) * mm, "end": v(-57.33, -24.06) * mm});
            skLineSegment(sketch, "E1396", {"start": v(-39.78, -26.32) * mm, "end": v(-39.98, -26.63) * mm});
            skLineSegment(sketch, "E1397", {"start": v(-39.98, -26.63) * mm, "end": v(-40.3, -26.64) * mm});
            skLineSegment(sketch, "E1398", {"start": v(-40.3, -26.64) * mm, "end": v(-40.12, -26.27) * mm});
            skLineSegment(sketch, "E1399", {"start": v(-40.12, -26.27) * mm, "end": v(-39.87, -26.22) * mm});
            skLineSegment(sketch, "E1400", {"start": v(-39.87, -26.22) * mm, "end": v(-39.78, -26.32) * mm});
            skLineSegment(sketch, "E1401", {"start": v(-38.54, -26.52) * mm, "end": v(-39.15, -26.22) * mm});
            skLineSegment(sketch, "E1402", {"start": v(-39.15, -26.22) * mm, "end": v(-39.1, -25.8) * mm});
            skLineSegment(sketch, "E1403", {"start": v(-39.1, -25.8) * mm, "end": v(-38.61, -25.61) * mm});
            skLineSegment(sketch, "E1404", {"start": v(-38.61, -25.61) * mm, "end": v(-38.17, -25.67) * mm});
            skLineSegment(sketch, "E1405", {"start": v(-38.17, -25.67) * mm, "end": v(-38.13, -26.07) * mm});
            skLineSegment(sketch, "E1406", {"start": v(-38.13, -26.07) * mm, "end": v(-38.22, -26.49) * mm});
            skLineSegment(sketch, "E1407", {"start": v(-38.22, -26.49) * mm, "end": v(-38.54, -26.52) * mm});
            skLineSegment(sketch, "E1408", {"start": v(-34.3, -27.81) * mm, "end": v(-34.62, -27.66) * mm});
            skLineSegment(sketch, "E1409", {"start": v(-34.62, -27.66) * mm, "end": v(-35.05, -26.83) * mm});
            skLineSegment(sketch, "E1410", {"start": v(-35.05, -26.83) * mm, "end": v(-35.74, -27.14) * mm});
            skLineSegment(sketch, "E1411", {"start": v(-35.74, -27.14) * mm, "end": v(-35.8, -27.34) * mm});
            skLineSegment(sketch, "E1412", {"start": v(-35.8, -27.34) * mm, "end": v(-35.38, -27.97) * mm});
            skLineSegment(sketch, "E1413", {"start": v(-35.38, -27.97) * mm, "end": v(-34.96, -27.88) * mm});
            skLineSegment(sketch, "E1414", {"start": v(-34.96, -27.88) * mm, "end": v(-34.82, -28.02) * mm});
            skLineSegment(sketch, "E1415", {"start": v(-34.82, -28.02) * mm, "end": v(-34.4, -28.01) * mm});
            skLineSegment(sketch, "E1416", {"start": v(-34.4, -28.01) * mm, "end": v(-34.3, -27.81) * mm});
            skLineSegment(sketch, "E1417", {"start": v(-33.41, -28.12) * mm, "end": v(-33.56, -28.33) * mm});
            skLineSegment(sketch, "E1418", {"start": v(-33.56, -28.33) * mm, "end": v(-33.12, -28.49) * mm});
            skLineSegment(sketch, "E1419", {"start": v(-33.12, -28.49) * mm, "end": v(-32.47, -28.57) * mm});
            skLineSegment(sketch, "E1420", {"start": v(-32.47, -28.57) * mm, "end": v(-32.17, -28.4) * mm});
            skLineSegment(sketch, "E1421", {"start": v(-32.17, -28.4) * mm, "end": v(-32.17, -28.22) * mm});
            skLineSegment(sketch, "E1422", {"start": v(-32.17, -28.22) * mm, "end": v(-32.85, -28.2) * mm});
            skLineSegment(sketch, "E1423", {"start": v(-32.85, -28.2) * mm, "end": v(-32.92, -28.3) * mm});
            skLineSegment(sketch, "E1424", {"start": v(-32.92, -28.3) * mm, "end": v(-33.16, -28.16) * mm});
            skLineSegment(sketch, "E1425", {"start": v(-33.16, -28.16) * mm, "end": v(-33.41, -28.12) * mm});
            skLineSegment(sketch, "E1426", {"start": v(-32.51, -28.8) * mm, "end": v(-32.39, -28.95) * mm});
            skLineSegment(sketch, "E1427", {"start": v(-32.39, -28.95) * mm, "end": v(-32.38, -29.17) * mm});
            skLineSegment(sketch, "E1428", {"start": v(-32.38, -29.17) * mm, "end": v(-32.77, -29.35) * mm});
            skLineSegment(sketch, "E1429", {"start": v(-32.77, -29.35) * mm, "end": v(-32.98, -28.84) * mm});
            skLineSegment(sketch, "E1430", {"start": v(-32.98, -28.84) * mm, "end": v(-32.51, -28.8) * mm});
            skLineSegment(sketch, "E1431", {"start": v(-32.21, -28.77) * mm, "end": v(-31.92, -28.43) * mm});
            skLineSegment(sketch, "E1432", {"start": v(-31.92, -28.43) * mm, "end": v(-31.44, -28.7) * mm});
            skLineSegment(sketch, "E1433", {"start": v(-31.44, -28.7) * mm, "end": v(-31.03, -28.82) * mm});
            skLineSegment(sketch, "E1434", {"start": v(-31.03, -28.82) * mm, "end": v(-30.45, -29.13) * mm});
            skLineSegment(sketch, "E1435", {"start": v(-30.45, -29.13) * mm, "end": v(-30.46, -29.33) * mm});
            skLineSegment(sketch, "E1436", {"start": v(-30.46, -29.33) * mm, "end": v(-31.36, -29.68) * mm});
            skLineSegment(sketch, "E1437", {"start": v(-31.36, -29.68) * mm, "end": v(-31.61, -29.53) * mm});
            skLineSegment(sketch, "E1438", {"start": v(-31.61, -29.53) * mm, "end": v(-32.21, -28.77) * mm});
            skLineSegment(sketch, "E1439", {"start": v(-28.82, -32.77) * mm, "end": v(-28.72, -32.84) * mm});
            skLineSegment(sketch, "E1440", {"start": v(-28.72, -32.84) * mm, "end": v(-28.21, -32.73) * mm});
            skLineSegment(sketch, "E1441", {"start": v(-28.21, -32.73) * mm, "end": v(-27.72, -32.27) * mm});
            skLineSegment(sketch, "E1442", {"start": v(-27.72, -32.27) * mm, "end": v(-28.24, -31.92) * mm});
            skLineSegment(sketch, "E1443", {"start": v(-28.24, -31.92) * mm, "end": v(-28.53, -31.22) * mm});
            skLineSegment(sketch, "E1444", {"start": v(-28.53, -31.22) * mm, "end": v(-30.15, -30.4) * mm});
            skLineSegment(sketch, "E1445", {"start": v(-30.15, -30.4) * mm, "end": v(-30.36, -30.5) * mm});
            skLineSegment(sketch, "E1446", {"start": v(-30.36, -30.5) * mm, "end": v(-30.14, -30.92) * mm});
            skLineSegment(sketch, "E1447", {"start": v(-30.14, -30.92) * mm, "end": v(-30.36, -31.3) * mm});
            skLineSegment(sketch, "E1448", {"start": v(-30.36, -31.3) * mm, "end": v(-30.63, -31.4) * mm});
            skLineSegment(sketch, "E1449", {"start": v(-30.63, -31.4) * mm, "end": v(-30.7, -31.73) * mm});
            skLineSegment(sketch, "E1450", {"start": v(-30.7, -31.73) * mm, "end": v(-30.44, -31.96) * mm});
            skLineSegment(sketch, "E1451", {"start": v(-30.44, -31.96) * mm, "end": v(-30.26, -32.62) * mm});
            skLineSegment(sketch, "E1452", {"start": v(-30.26, -32.62) * mm, "end": v(-30.31, -33.34) * mm});
            skLineSegment(sketch, "E1453", {"start": v(-30.31, -33.34) * mm, "end": v(-29.8, -33.7) * mm});
            skLineSegment(sketch, "E1454", {"start": v(-29.8, -33.7) * mm, "end": v(-29.16, -32.97) * mm});
            skLineSegment(sketch, "E1455", {"start": v(-29.16, -32.97) * mm, "end": v(-28.82, -32.77) * mm});
            skLineSegment(sketch, "E1456", {"start": v(12.39, -8.45) * mm, "end": v(12.39, -8.45) * mm});
            skLineSegment(sketch, "E1457", {"start": v(-47.5, -1.93) * mm, "end": v(-37.95, -3.53) * mm});
            skArc(sketch, "E1458", {"start": v(-37.95, -3.53) * mm, "mid": v(-32.18, -4.33) * mm, "end": v(-26.38, -4.78) * mm});
            skLineSegment(sketch, "E1459", {"start": v(-24.6, -4.9) * mm, "end": v(-24.13, 2.5) * mm});
            skLineSegment(sketch, "E1460", {"start": v(-26.38, -4.78) * mm, "end": v(-24.6, -4.9) * mm});
            skLineSegment(sketch, "E1461", {"start": v(-24.6, -4.9) * mm, "end": v(-13.7, -5.25) * mm});
            skLineSegment(sketch, "E1462", {"start": v(-13.7, -5.25) * mm, "end": v(-10.36, -5.27) * mm});
            skLineSegment(sketch, "E1463", {"start": v(-36.72, 6.23) * mm, "end": v(-31.65, 5.6) * mm});
            skLineSegment(sketch, "E1464", {"start": v(-31.65, 5.6) * mm, "end": v(-27.61, 5.23) * mm});
            skLineSegment(sketch, "E1465", {"start": v(-27.61, 5.23) * mm, "end": v(-23.98, 4.92) * mm});
            skLineSegment(sketch, "E1466", {"start": v(-27.22, 10.09) * mm, "end": v(-27.61, 5.23) * mm});
            skLineSegment(sketch, "E1467", {"start": v(-27.22, 10.09) * mm, "end": v(-26.84, 14.95) * mm});
            skLineSegment(sketch, "E1468", {"start": v(-44.29, -33.36) * mm, "end": v(-44.37, -33.72) * mm});
            skSolve(sketch);
        }
        {
            var Q0;
            {var subQ0=sQuery(id+"F0.wireOp",EDGE,"E17");Q0=makeQuery(id+"F0.imprint","IMPRINT",FACE,{"disambiguationData":[TD([[makeQuery(id+"F0.imprint","IMPRINT",EDGE,{"derivedFrom":subQ0}),1.0]])]});}
            extrude(context, id + "F1", {"entities" : qUnion([Q0]), "depth" : 30.8 * mm, "offsetDistance" : 25.4 * mm});
        }
        {
            var Q0;
            {var subQ0=sQuery(id+"F0.wireOp",EDGE,"E122");Q0=makeQuery(id+"F0.imprint","IMPRINT",FACE,{"disambiguationData":[TD([[makeQuery(id+"F0.imprint","IMPRINT",EDGE,{"derivedFrom":subQ0}),1.0]])]});}
            extrude(context, id + "F2", {"entities" : qUnion([Q0]), "operationType" : NewBodyOperationType.ADD, "depth" : 3.16 * mm, "offsetDistance" : 25.4 * mm});
        }
        {
            var Q0;
            {var subQ0=sQuery(id+"F0.wireOp",EDGE,"E49");Q0=makeQuery(id+"F0.imprint","IMPRINT",FACE,{"disambiguationData":[TD([[makeQuery(id+"F0.imprint","IMPRINT",EDGE,{"derivedFrom":subQ0}),-1.0]])]});}
            extrude(context, id + "F3", {"entities" : qUnion([Q0]), "operationType" : NewBodyOperationType.ADD, "depth" : 69714060 / 8029672510.6 * mm, "offsetDistance" : 25.4 * mm});
        }
        {
            var Q0;
            {var subQ0=sQuery(id+"F0.wireOp",EDGE,"E15");Q0=makeQuery(id+"F0.imprint","IMPRINT",FACE,{"disambiguationData":[TD([[makeQuery(id+"F0.imprint","IMPRINT",EDGE,{"derivedFrom":subQ0}),1.0]])]});}
            extrude(context, id + "F4", {"entities" : qUnion([Q0]), "operationType" : NewBodyOperationType.ADD, "depth" : 2.24 * mm, "offsetDistance" : 25.4 * mm});
        }
        {
            var Q0;
            {var subQ1=sQuery(id+"F0.wireOp",EDGE,"E12");Q0=makeQuery(id+"F0.imprint","IMPRINT",FACE,{"disambiguationData":[TD([[makeQuery(id+"F0.imprint","IMPRINT",EDGE,{"derivedFrom":subQ1}),1.0]])]});}
            extrude(context, id + "F5", {"entities" : qUnion([Q0]), "operationType" : NewBodyOperationType.ADD, "depth" : 1.3 * mm, "offsetDistance" : 25.4 * mm});
        }
        {
            var Q0;
            {var subQ5=sQuery(id+"F0.wireOp",EDGE,"E20");Q0=makeQuery(id+"F0.imprint","IMPRINT",FACE,{"disambiguationData":[TD([[makeQuery(id+"F0.imprint","IMPRINT",EDGE,{"derivedFrom":subQ5}),-1.0]])]});}
            extrude(context, id + "F6", {"entities" : qUnion([Q0]), "operationType" : NewBodyOperationType.ADD, "depth" : 0.82 * mm, "offsetDistance" : 25.4 * mm});
        }
        {
            var Q0;
            {var subQ0=sQuery(id+"F0.wireOp",EDGE,"E21");Q0=makeQuery(id+"F0.imprint","IMPRINT",FACE,{"disambiguationData":[TD([[makeQuery(id+"F0.imprint","IMPRINT",EDGE,{"derivedFrom":subQ0}),1.0]])]});}
            extrude(context, id + "F7", {"entities" : qUnion([Q0]), "depth" : 5.32 * mm, "offsetDistance" : 25.4 * mm});
        }
        {
            var Q0;
            {var subQ1=sQuery(id+"F0.wireOp",EDGE,"E13");Q0=makeQuery(id+"F0.imprint","IMPRINT",FACE,{"disambiguationData":[TD([[makeQuery(id+"F0.imprint","IMPRINT",EDGE,{"derivedFrom":subQ1}),1.0]])]});}
            extrude(context, id + "F8", {"entities" : qUnion([Q0]), "operationType" : NewBodyOperationType.ADD, "depth" : 0.47 * mm, "offsetDistance" : 25.4 * mm});
        }
        {
            var Q0;
            {var subQ0=sQuery(id+"F0.wireOp",EDGE,"E36");Q0=makeQuery(id+"F0.imprint","IMPRINT",FACE,{"disambiguationData":[TD([[makeQuery(id+"F0.imprint","IMPRINT",EDGE,{"derivedFrom":subQ0}),-1.0]])]});}
            extrude(context, id + "F9", {"entities" : qUnion([Q0]), "operationType" : NewBodyOperationType.ADD, "depth" : 1.5 * mm, "offsetDistance" : 25.4 * mm});
        }
        {
            var Q0;
            {var subQ4=sQuery(id+"F0.wireOp",EDGE,"E260");Q0=makeQuery(id+"F0.imprint","IMPRINT",FACE,{"disambiguationData":[TD([[makeQuery(id+"F0.imprint","IMPRINT",EDGE,{"derivedFrom":subQ4}),1.0]])]});}
            extrude(context, id + "F10", {"entities" : qUnion([Q0]), "operationType" : NewBodyOperationType.ADD, "depth" : 0.58 * mm, "offsetDistance" : 25.4 * mm});
        }
        {
            var Q0;
            {var subQ1=sQuery(id+"F0.wireOp",EDGE,"E36");Q0=makeQuery(id+"F0.imprint","IMPRINT",FACE,{"disambiguationData":[TD([[makeQuery(id+"F0.imprint","IMPRINT",EDGE,{"derivedFrom":subQ1}),1.0]])]});}
            extrude(context, id + "F11", {"entities" : qUnion([Q0]), "operationType" : NewBodyOperationType.ADD, "depth" : 0.68 * mm, "offsetDistance" : 25.4 * mm});
        }
        {
            var Q0;
            {var subQ1=sQuery(id+"F0.wireOp",EDGE,"E37");Q0=makeQuery(id+"F0.imprint","IMPRINT",FACE,{"disambiguationData":[TD([[makeQuery(id+"F0.imprint","IMPRINT",EDGE,{"derivedFrom":subQ1}),-1.0]])]});}
            extrude(context, id + "F12", {"entities" : qUnion([Q0]), "operationType" : NewBodyOperationType.ADD, "depth" : 28939570 / 8029672510.6 * mm, "offsetDistance" : 25.4 * mm});
        }
        {
            var Q0;
            {var subQ0=sQuery(id+"F0.wireOp",EDGE,"E21");Q0=makeQuery(id+"F0.imprint","IMPRINT",FACE,{"disambiguationData":[TD([[makeQuery(id+"F0.imprint","IMPRINT",EDGE,{"derivedFrom":subQ0}),-1.0]])]});}
            extrude(context, id + "F13", {"entities" : qUnion([Q0]), "operationType" : NewBodyOperationType.ADD, "depth" : 1.68 * mm, "offsetDistance" : 25.4 * mm});
        }
        {
            var Q0;
            {var subQ3=sQuery(id+"F0.wireOp",EDGE,"E24");Q0=makeQuery(id+"F0.imprint","IMPRINT",FACE,{"disambiguationData":[TD([[makeQuery(id+"F0.imprint","IMPRINT",EDGE,{"derivedFrom":subQ3}),-1.0]])]});}
            extrude(context, id + "F14", {"entities" : qUnion([Q0]), "operationType" : NewBodyOperationType.ADD, "depth" : 3.1 * mm, "offsetDistance" : 25.4 * mm});
        }
        {
            var Q0;
            Q0=makeQuery(id+"F0.imprint","IMPRINT",FACE,{"disambiguationData":[TD([[makeQuery(id+"F0.imprint","IMPRINT",EDGE,{"derivedFrom":sQuery(id+"F0.wireOp",EDGE,"E0")}),-1.0]])]});
            extrude(context, id + "F15", {"entities" : qUnion([Q0]), "operationType" : NewBodyOperationType.ADD, "depth" : 21.25 * mm, "offsetDistance" : 25.4 * mm});
        }
        {
            var Q0;
            {var subQ1=sQuery(id+"F0.wireOp",EDGE,"E261");Q0=makeQuery(id+"F0.imprint","IMPRINT",FACE,{"disambiguationData":[TD([[makeQuery(id+"F0.imprint","IMPRINT",EDGE,{"derivedFrom":subQ1}),-1.0]])]});}
            extrude(context, id + "F16", {"entities" : qUnion([Q0]), "operationType" : NewBodyOperationType.ADD, "depth" : 4.36 * mm, "offsetDistance" : 25.4 * mm});
        }
        {
            var Q0;
            Q0=makeQuery(id+"F0.imprint","IMPRINT",FACE,{"disambiguationData":[TD([[makeQuery(id+"F0.imprint","IMPRINT",EDGE,{"derivedFrom":sQuery(id+"F0.wireOp",EDGE,"E39")}),1.0]])]});
            extrude(context, id + "F17", {"entities" : qUnion([Q0]), "operationType" : NewBodyOperationType.ADD, "depth" : 2.48 * mm, "offsetDistance" : 25.4 * mm});
        }
        {
            var Q0;
            Q0=makeQuery(id+"F0.imprint","IMPRINT",FACE,{"disambiguationData":[TD([[makeQuery(id+"F0.imprint","IMPRINT",EDGE,{"derivedFrom":sQuery(id+"F0.wireOp",EDGE,"E39")}),-1.0]])]});
            extrude(context, id + "F18", {"entities" : qUnion([Q0]), "operationType" : NewBodyOperationType.ADD, "depth" : 4.86 * mm, "offsetDistance" : 25.4 * mm});
        }
        {
            var Q0;
            Q0=makeQuery(id+"F0.imprint","IMPRINT",FACE,{"disambiguationData":[TD([[makeQuery(id+"F0.imprint","IMPRINT",EDGE,{"derivedFrom":sQuery(id+"F0.wireOp",EDGE,"E47")}),-1.0]])]});
            extrude(context, id + "F19", {"entities" : qUnion([Q0]), "operationType" : NewBodyOperationType.ADD, "depth" : 2.38 * mm, "offsetDistance" : 25.4 * mm});
        }
        {
            var Q0;
            Q0=makeQuery(id+"F0.imprint","IMPRINT",FACE,{"disambiguationData":[TD([[makeQuery(id+"F0.imprint","IMPRINT",EDGE,{"derivedFrom":sQuery(id+"F0.wireOp",EDGE,"E54")}),-1.0]])]});
            extrude(context, id + "F20", {"entities" : qUnion([Q0]), "operationType" : NewBodyOperationType.ADD, "depth" : 3.72 * mm, "offsetDistance" : 25.4 * mm});
        }
        {
            var Q0;
            Q0=makeQuery(id+"F0.imprint","IMPRINT",FACE,{"disambiguationData":[TD([[makeQuery(id+"F0.imprint","IMPRINT",EDGE,{"derivedFrom":sQuery(id+"F0.wireOp",EDGE,"E40")}),1.0]])]});
            extrude(context, id + "F21", {"entities" : qUnion([Q0]), "operationType" : NewBodyOperationType.ADD, "depth" : 4.61 * mm, "offsetDistance" : 25.4 * mm});
        }
        {
            var Q0;
            Q0=makeQuery(id+"F0.imprint","IMPRINT",FACE,{"disambiguationData":[TD([[makeQuery(id+"F0.imprint","IMPRINT",EDGE,{"derivedFrom":sQuery(id+"F0.wireOp",EDGE,"E40")}),-1.0]])]});
            extrude(context, id + "F22", {"entities" : qUnion([Q0]), "operationType" : NewBodyOperationType.ADD, "depth" : 10.35 * mm, "offsetDistance" : 25.4 * mm});
        }
        {
            var Q0;
            {var subQ0=sQuery(id+"F0.wireOp",EDGE,"E41");Q0=makeQuery(id+"F0.imprint","IMPRINT",FACE,{"disambiguationData":[TD([[makeQuery(id+"F0.imprint","IMPRINT",EDGE,{"derivedFrom":subQ0}),1.0]])]});}
            var Q1;
            Q1=makeQuery(id+"F0.imprint","IMPRINT",FACE,{"disambiguationData":[TD([[makeQuery(id+"F0.imprint","IMPRINT",EDGE,{"derivedFrom":sQuery(id+"F0.wireOp",EDGE,"E577")}),-1.0]])]});
            extrude(context, id + "F23", {"entities" : qUnion([Q0, Q1]), "operationType" : NewBodyOperationType.ADD, "depth" : 7.95 * mm, "offsetDistance" : 25.4 * mm});
        }
        {
            var Q0;
            {var subQ3=sQuery(id+"F0.wireOp",EDGE,"E41");Q0=makeQuery(id+"F0.imprint","IMPRINT",FACE,{"disambiguationData":[TD([[makeQuery(id+"F0.imprint","IMPRINT",EDGE,{"derivedFrom":subQ3}),-1.0]])]});}
            extrude(context, id + "F24", {"entities" : qUnion([Q0]), "operationType" : NewBodyOperationType.ADD, "depth" : 5.28 * mm, "offsetDistance" : 25.4 * mm});
        }
        {
            var Q0;
            Q0=makeQuery(id+"F0.imprint","IMPRINT",FACE,{"disambiguationData":[TD([[makeQuery(id+"F0.imprint","IMPRINT",EDGE,{"derivedFrom":sQuery(id+"F0.wireOp",EDGE,"E51")}),1.0]])]});
            extrude(context, id + "F25", {"entities" : qUnion([Q0]), "depth" : 3.53 * mm, "offsetDistance" : 25.4 * mm});
        }
        {
            var Q0;
            Q0=makeQuery(id+"F0.imprint","IMPRINT",FACE,{"disambiguationData":[TD([[makeQuery(id+"F0.imprint","IMPRINT",EDGE,{"derivedFrom":sQuery(id+"F0.wireOp",EDGE,"E51")}),-1.0]])]});
            extrude(context, id + "F26", {"entities" : qUnion([Q0]), "operationType" : NewBodyOperationType.ADD, "depth" : 5.22 * mm, "offsetDistance" : 25.4 * mm});
        }
        {
            var Q0;
            {var subQ0=sQuery(id+"F0.wireOp",EDGE,"E308");Q0=makeQuery(id+"F0.imprint","IMPRINT",FACE,{"disambiguationData":[TD([[makeQuery(id+"F0.imprint","IMPRINT",EDGE,{"derivedFrom":subQ0}),-1.0]])]});}
            extrude(context, id + "F27", {"entities" : qUnion([Q0]), "depth" : 2.4 * mm, "offsetDistance" : 25.4 * mm});
        }
        {
            var Q0;
            {var subQ0=sQuery(id+"F0.wireOp",EDGE,"E43");Q0=makeQuery(id+"F0.imprint","IMPRINT",FACE,{"disambiguationData":[TD([[makeQuery(id+"F0.imprint","IMPRINT",EDGE,{"derivedFrom":subQ0}),-1.0]])]});}
            extrude(context, id + "F28", {"entities" : qUnion([Q0]), "operationType" : NewBodyOperationType.ADD, "depth" : 9.3 * mm, "offsetDistance" : 25.4 * mm});
        }
        {
            var Q0;
            {var subQ0=sQuery(id+"F0.wireOp",EDGE,"E307");Q0=makeQuery(id+"F0.imprint","IMPRINT",FACE,{"disambiguationData":[TD([[makeQuery(id+"F0.imprint","IMPRINT",EDGE,{"derivedFrom":subQ0}),-1.0]])]});}
            extrude(context, id + "F29", {"entities" : qUnion([Q0]), "operationType" : NewBodyOperationType.ADD, "depth" : 3.88 * mm, "offsetDistance" : 25.4 * mm});
        }
        {
            var Q0;
            Q0=makeQuery(id+"F0.imprint","IMPRINT",FACE,{"disambiguationData":[TD([[makeQuery(id+"F0.imprint","IMPRINT",EDGE,{"derivedFrom":sQuery(id+"F0.wireOp",EDGE,"E317")}),1.0]])]});
            extrude(context, id + "F30", {"entities" : qUnion([Q0]), "operationType" : NewBodyOperationType.ADD, "depth" : 15.71 * mm, "offsetDistance" : 25.4 * mm});
        }
        {
            var Q0;
            Q0=makeQuery(id+"F0.imprint","IMPRINT",FACE,{"disambiguationData":[TD([[makeQuery(id+"F0.imprint","IMPRINT",EDGE,{"derivedFrom":sQuery(id+"F0.wireOp",EDGE,"E1179")}),1.0]])]});
            extrude(context, id + "F31", {"entities" : qUnion([Q0]), "operationType" : NewBodyOperationType.ADD, "depth" : 0.6 * mm, "offsetDistance" : 25.4 * mm});
        }
        {
            var Q0;
            Q0=makeQuery(id+"F0.imprint","IMPRINT",FACE,{"disambiguationData":[TD([[makeQuery(id+"F0.imprint","IMPRINT",EDGE,{"derivedFrom":sQuery(id+"F0.wireOp",EDGE,"E1439")}),1.0]])]});
            var Q1;
            Q1=makeQuery(id+"F0.imprint","IMPRINT",FACE,{"disambiguationData":[TD([[makeQuery(id+"F0.imprint","IMPRINT",EDGE,{"derivedFrom":sQuery(id+"F0.wireOp",EDGE,"E1401")}),-1.0]])]});
            var Q2;
            Q2=makeQuery(id+"F0.imprint","IMPRINT",FACE,{"disambiguationData":[TD([[makeQuery(id+"F0.imprint","IMPRINT",EDGE,{"derivedFrom":sQuery(id+"F0.wireOp",EDGE,"E1408")}),1.0]])]});
            var Q3;
            Q3=makeQuery(id+"F0.imprint","IMPRINT",FACE,{"disambiguationData":[TD([[makeQuery(id+"F0.imprint","IMPRINT",EDGE,{"derivedFrom":sQuery(id+"F0.wireOp",EDGE,"E1431")}),-1.0]])]});
            var Q4;
            Q4=makeQuery(id+"F0.imprint","IMPRINT",FACE,{"disambiguationData":[TD([[makeQuery(id+"F0.imprint","IMPRINT",EDGE,{"derivedFrom":sQuery(id+"F0.wireOp",EDGE,"E1417")}),1.0]])]});
            var Q5;
            Q5=makeQuery(id+"F0.imprint","IMPRINT",FACE,{"disambiguationData":[TD([[makeQuery(id+"F0.imprint","IMPRINT",EDGE,{"derivedFrom":sQuery(id+"F0.wireOp",EDGE,"E1426")}),-1.0]])]});
            var Q6;
            Q6=makeQuery(id+"F0.imprint","IMPRINT",FACE,{"disambiguationData":[TD([[makeQuery(id+"F0.imprint","IMPRINT",EDGE,{"derivedFrom":sQuery(id+"F0.wireOp",EDGE,"E1396")}),-1.0]])]});
            extrude(context, id + "F32", {"entities" : qUnion([Q0, Q1, Q2, Q3, Q4, Q5, Q6]), "depth" : 1.13 * mm, "offsetDistance" : 25.4 * mm});
        }
        {
            var Q0;
            {var subQ4=sQuery(id+"F0.wireOp",EDGE,"E307");Q0=makeQuery(id+"F0.imprint","IMPRINT",FACE,{"disambiguationData":[TD([[makeQuery(id+"F0.imprint","IMPRINT",EDGE,{"derivedFrom":subQ4}),1.0]])]});}
            extrude(context, id + "F33", {"entities" : qUnion([Q0]), "operationType" : NewBodyOperationType.ADD, "depth" : 8.03 * mm, "offsetDistance" : 25.4 * mm});
        }
        {
            var Q0;
            Q0=makeQuery(id+"F0.imprint","IMPRINT",FACE,{"disambiguationData":[TD([[makeQuery(id+"F0.imprint","IMPRINT",EDGE,{"derivedFrom":sQuery(id+"F0.wireOp",EDGE,"E1076")}),-1.0]])]});
            extrude(context, id + "F34", {"entities" : qUnion([Q0]), "operationType" : NewBodyOperationType.ADD, "depth" : 3.84 * mm, "offsetDistance" : 25.4 * mm});
        }
        {
            var Q0;
            {var subQ4=sQuery(id+"F0.wireOp",EDGE,"E692");Q0=makeQuery(id+"F0.imprint","IMPRINT",FACE,{"disambiguationData":[TD([[makeQuery(id+"F0.imprint","IMPRINT",EDGE,{"derivedFrom":subQ4}),-1.0]])]});}
            extrude(context, id + "F35", {"entities" : qUnion([Q0]), "operationType" : NewBodyOperationType.ADD, "depth" : 7.9 * mm, "offsetDistance" : 25.4 * mm});
        }
        {
            var Q0;
            {var subQ0=sQuery(id+"F0.wireOp",EDGE,"E708");Q0=makeQuery(id+"F0.imprint","IMPRINT",FACE,{"disambiguationData":[TD([[makeQuery(id+"F0.imprint","IMPRINT",EDGE,{"derivedFrom":subQ0}),-1.0]])]});}
            extrude(context, id + "F36", {"entities" : qUnion([Q0]), "depth" : 6.64 * mm, "offsetDistance" : 25.4 * mm});
        }
        {
            var Q0;
            Q0=makeQuery(id+"F0.imprint","IMPRINT",FACE,{"disambiguationData":[TD([[makeQuery(id+"F0.imprint","IMPRINT",EDGE,{"derivedFrom":sQuery(id+"F0.wireOp",EDGE,"E711")}),-1.0]])]});
            extrude(context, id + "F37", {"entities" : qUnion([Q0]), "depth" : 1.5 * mm, "offsetDistance" : 25.4 * mm});
        }
        {
            var Q0;
            Q0=makeQuery(id+"F0.imprint","IMPRINT",FACE,{"disambiguationData":[TD([[makeQuery(id+"F0.imprint","IMPRINT",EDGE,{"derivedFrom":sQuery(id+"F0.wireOp",EDGE,"E44")}),-1.0]])]});
            extrude(context, id + "F38", {"entities" : qUnion([Q0]), "operationType" : NewBodyOperationType.ADD, "depth" : 10.23 * mm, "offsetDistance" : 25.4 * mm});
        }
        {
            var Q0;
            Q0=makeQuery(id+"F0.imprint","IMPRINT",FACE,{"disambiguationData":[TD([[makeQuery(id+"F0.imprint","IMPRINT",EDGE,{"derivedFrom":sQuery(id+"F0.wireOp",EDGE,"E10")}),-1.0]])]});
            extrude(context, id + "F39", {"entities" : qUnion([Q0]), "operationType" : NewBodyOperationType.ADD, "depth" : 2.33 * mm, "offsetDistance" : 25.4 * mm});
        }
    });
